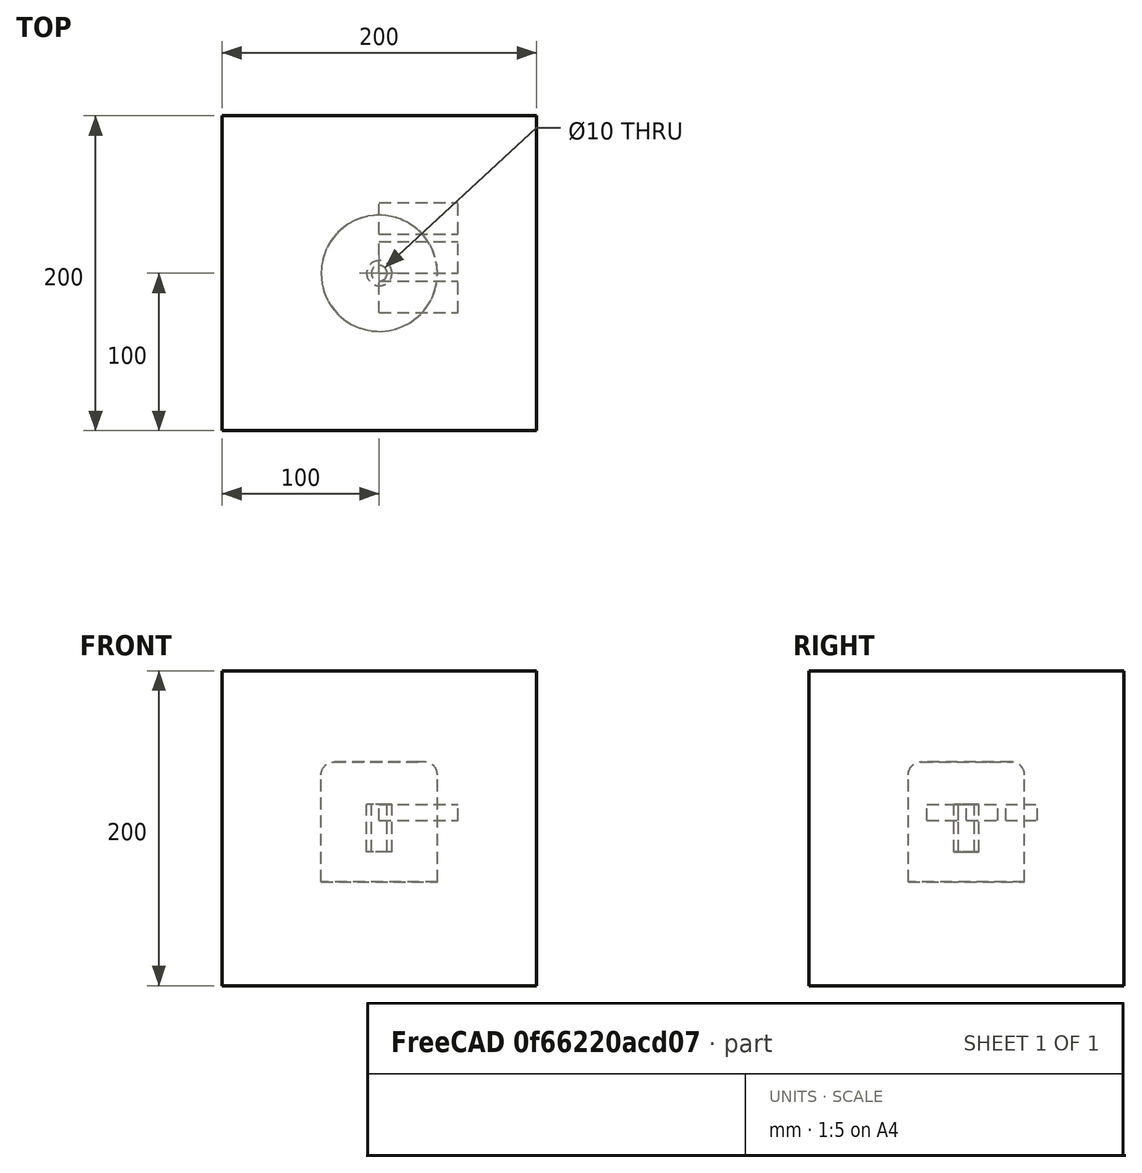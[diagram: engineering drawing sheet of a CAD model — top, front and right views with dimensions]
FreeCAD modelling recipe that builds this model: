
FCSTD DOCUMENT  (FreeCAD 1.0R39109 (Git))
Label: assemblyTest-A
License: All rights reserved
LicenseURL: http://en.wikipedia.org/wiki/All_rights_reserved
objects: App::DocumentObjectGroupPython×1254, Part::FeaturePython×5, App::Part×5, Part::Box×3, Part::Fuse×2
note: 10 computed .brp shape members not serialized (recipe doc carries the construction recipe); baked Part::Feature solids carry a one-line shape summary decoded from their .brp

FEATURE [App::DocumentObjectGroupPython] HALFPI  # scripted group (container) (typed FeaturePython)
  name = HALFPI
  value = pi/2.
FEATURE [App::DocumentObjectGroupPython] PI  # scripted group (container) (typed FeaturePython)
  name = PI
  value = 1.*pi
FEATURE [App::DocumentObjectGroupPython] TWOPI  # scripted group (container) (typed FeaturePython)
  name = TWOPI
  value = 2.*pi
FEATURE [App::DocumentObjectGroupPython] Variables  # scripted group (container) (typed FeaturePython)
FEATURE [App::DocumentObjectGroupPython] Quantities  # scripted group (container) (typed FeaturePython)
FEATURE [App::DocumentObjectGroupPython] Isotopes  # scripted group (container) (typed FeaturePython)
FEATURE [App::DocumentObjectGroupPython] Elements  # scripted group (container) (typed FeaturePython)
FEATURE [App::DocumentObjectGroupPython] G4Isotopes  # scripted group (container) (typed FeaturePython)
FEATURE [App::DocumentObjectGroupPython] H_element  # scripted group (container) (typed FeaturePython)
  Z = 1
  atom_value = 1.008
  formula = H
  name = H_element
FEATURE [App::DocumentObjectGroupPython] He_element  # scripted group (container) (typed FeaturePython)
  Z = 2
  atom_value = 4.0026
  formula = He
  name = He_element
FEATURE [App::DocumentObjectGroupPython] Li_element  # scripted group (container) (typed FeaturePython)
  Z = 3
  atom_value = 6.94
  formula = Li
  name = Li_element
FEATURE [App::DocumentObjectGroupPython] Be_element  # scripted group (container) (typed FeaturePython)
  Z = 4
  atom_value = 9.01218
  formula = Be
  name = Be_element
FEATURE [App::DocumentObjectGroupPython] B_element  # scripted group (container) (typed FeaturePython)
  Z = 5
  atom_value = 10.81
  formula = B
  name = B_element
FEATURE [App::DocumentObjectGroupPython] C_element  # scripted group (container) (typed FeaturePython)
  Z = 6
  atom_value = 12.011
  formula = C
  name = C_element
FEATURE [App::DocumentObjectGroupPython] N_element  # scripted group (container) (typed FeaturePython)
  Z = 7
  atom_value = 14.007
  formula = N
  name = N_element
FEATURE [App::DocumentObjectGroupPython] O_element  # scripted group (container) (typed FeaturePython)
  Z = 8
  atom_value = 15.999
  formula = O
  name = O_element
FEATURE [App::DocumentObjectGroupPython] F_element  # scripted group (container) (typed FeaturePython)
  Z = 9
  atom_value = 18.9984
  formula = F
  name = F_element
FEATURE [App::DocumentObjectGroupPython] Ne_element  # scripted group (container) (typed FeaturePython)
  Z = 10
  atom_value = 20.1797
  formula = Ne
  name = Ne_element
FEATURE [App::DocumentObjectGroupPython] Na_element  # scripted group (container) (typed FeaturePython)
  Z = 11
  atom_value = 22.9898
  formula = Na
  name = Na_element
FEATURE [App::DocumentObjectGroupPython] Mg_element  # scripted group (container) (typed FeaturePython)
  Z = 12
  atom_value = 24.305
  formula = Mg
  name = Mg_element
FEATURE [App::DocumentObjectGroupPython] Al_element  # scripted group (container) (typed FeaturePython)
  Z = 13
  atom_value = 26.9815
  formula = Al
  name = Al_element
FEATURE [App::DocumentObjectGroupPython] Si_element  # scripted group (container) (typed FeaturePython)
  Z = 14
  atom_value = 28.085
  formula = Si
  name = Si_element
FEATURE [App::DocumentObjectGroupPython] P_element  # scripted group (container) (typed FeaturePython)
  Z = 15
  atom_value = 30.9738
  formula = P
  name = P_element
FEATURE [App::DocumentObjectGroupPython] S_element  # scripted group (container) (typed FeaturePython)
  Z = 16
  atom_value = 32.06
  formula = S
  name = S_element
FEATURE [App::DocumentObjectGroupPython] Cl_element  # scripted group (container) (typed FeaturePython)
  Z = 17
  atom_value = 35.45
  formula = Cl
  name = Cl_element
FEATURE [App::DocumentObjectGroupPython] Ar_element  # scripted group (container) (typed FeaturePython)
  Z = 18
  atom_value = 39.95
  formula = Ar
  name = Ar_element
FEATURE [App::DocumentObjectGroupPython] K_element  # scripted group (container) (typed FeaturePython)
  Z = 19
  atom_value = 39.0983
  formula = K
  name = K_element
FEATURE [App::DocumentObjectGroupPython] Ca_element  # scripted group (container) (typed FeaturePython)
  Z = 20
  atom_value = 40.078
  formula = Ca
  name = Ca_element
FEATURE [App::DocumentObjectGroupPython] Sc_element  # scripted group (container) (typed FeaturePython)
  Z = 21
  atom_value = 44.9559
  formula = Sc
  name = Sc_element
FEATURE [App::DocumentObjectGroupPython] Ti_element  # scripted group (container) (typed FeaturePython)
  Z = 22
  atom_value = 47.867
  formula = Ti
  name = Ti_element
FEATURE [App::DocumentObjectGroupPython] V_element  # scripted group (container) (typed FeaturePython)
  Z = 23
  atom_value = 50.9415
  formula = V
  name = V_element
FEATURE [App::DocumentObjectGroupPython] Cr_element  # scripted group (container) (typed FeaturePython)
  Z = 24
  atom_value = 51.9961
  formula = Cr
  name = Cr_element
FEATURE [App::DocumentObjectGroupPython] Mn_element  # scripted group (container) (typed FeaturePython)
  Z = 25
  atom_value = 54.938
  formula = Mn
  name = Mn_element
FEATURE [App::DocumentObjectGroupPython] Fe_element  # scripted group (container) (typed FeaturePython)
  Z = 26
  atom_value = 55.845
  formula = Fe
  name = Fe_element
FEATURE [App::DocumentObjectGroupPython] Co_element  # scripted group (container) (typed FeaturePython)
  Z = 27
  atom_value = 58.9332
  formula = Co
  name = Co_element
FEATURE [App::DocumentObjectGroupPython] Ni_element  # scripted group (container) (typed FeaturePython)
  Z = 28
  atom_value = 58.6934
  formula = Ni
  name = Ni_element
FEATURE [App::DocumentObjectGroupPython] Cu_element  # scripted group (container) (typed FeaturePython)
  Z = 29
  atom_value = 63.546
  formula = Cu
  name = Cu_element
FEATURE [App::DocumentObjectGroupPython] Zn_element  # scripted group (container) (typed FeaturePython)
  Z = 30
  atom_value = 65.38
  formula = Zn
  name = Zn_element
FEATURE [App::DocumentObjectGroupPython] Ga_element  # scripted group (container) (typed FeaturePython)
  Z = 31
  atom_value = 69.723
  formula = Ga
  name = Ga_element
FEATURE [App::DocumentObjectGroupPython] Ge_element  # scripted group (container) (typed FeaturePython)
  Z = 32
  atom_value = 72.63
  formula = Ge
  name = Ge_element
FEATURE [App::DocumentObjectGroupPython] As_element  # scripted group (container) (typed FeaturePython)
  Z = 33
  atom_value = 74.9216
  formula = As
  name = As_element
FEATURE [App::DocumentObjectGroupPython] Se_element  # scripted group (container) (typed FeaturePython)
  Z = 34
  atom_value = 78.971
  formula = Se
  name = Se_element
FEATURE [App::DocumentObjectGroupPython] Br_element  # scripted group (container) (typed FeaturePython)
  Z = 35
  atom_value = 79.904
  formula = Br
  name = Br_element
FEATURE [App::DocumentObjectGroupPython] Kr_element  # scripted group (container) (typed FeaturePython)
  Z = 36
  atom_value = 83.798
  formula = Kr
  name = Kr_element
FEATURE [App::DocumentObjectGroupPython] Rb_element  # scripted group (container) (typed FeaturePython)
  Z = 37
  atom_value = 85.4678
  formula = Rb
  name = Rb_element
FEATURE [App::DocumentObjectGroupPython] Sr_element  # scripted group (container) (typed FeaturePython)
  Z = 38
  atom_value = 87.62
  formula = Sr
  name = Sr_element
FEATURE [App::DocumentObjectGroupPython] Y_element  # scripted group (container) (typed FeaturePython)
  Z = 39
  atom_value = 88.9058
  formula = Y
  name = Y_element
FEATURE [App::DocumentObjectGroupPython] Zr_element  # scripted group (container) (typed FeaturePython)
  Z = 40
  atom_value = 91.224
  formula = Zr
  name = Zr_element
FEATURE [App::DocumentObjectGroupPython] Nb_element  # scripted group (container) (typed FeaturePython)
  Z = 41
  atom_value = 92.9064
  formula = Nb
  name = Nb_element
FEATURE [App::DocumentObjectGroupPython] Mo_element  # scripted group (container) (typed FeaturePython)
  Z = 42
  atom_value = 95.95
  formula = Mo
  name = Mo_element
FEATURE [App::DocumentObjectGroupPython] Tc_element  # scripted group (container) (typed FeaturePython)
  Z = 43
  atom_value = 97
  formula = Tc
  name = Tc_element
FEATURE [App::DocumentObjectGroupPython] Ru_element  # scripted group (container) (typed FeaturePython)
  Z = 44
  atom_value = 101.07
  formula = Ru
  name = Ru_element
FEATURE [App::DocumentObjectGroupPython] Rh_element  # scripted group (container) (typed FeaturePython)
  Z = 45
  atom_value = 102.905
  formula = Rh
  name = Rh_element
FEATURE [App::DocumentObjectGroupPython] Pd_element  # scripted group (container) (typed FeaturePython)
  Z = 46
  atom_value = 106.42
  formula = Pd
  name = Pd_element
FEATURE [App::DocumentObjectGroupPython] Ag_element  # scripted group (container) (typed FeaturePython)
  Z = 47
  atom_value = 107.868
  formula = Ag
  name = Ag_element
FEATURE [App::DocumentObjectGroupPython] Cd_element  # scripted group (container) (typed FeaturePython)
  Z = 48
  atom_value = 112.414
  formula = Cd
  name = Cd_element
FEATURE [App::DocumentObjectGroupPython] In_element  # scripted group (container) (typed FeaturePython)
  Z = 49
  atom_value = 114.818
  formula = In
  name = In_element
FEATURE [App::DocumentObjectGroupPython] Sn_element  # scripted group (container) (typed FeaturePython)
  Z = 50
  atom_value = 118.71
  formula = Sn
  name = Sn_element
FEATURE [App::DocumentObjectGroupPython] Sb_element  # scripted group (container) (typed FeaturePython)
  Z = 51
  atom_value = 121.76
  formula = Sb
  name = Sb_element
FEATURE [App::DocumentObjectGroupPython] Te_element  # scripted group (container) (typed FeaturePython)
  Z = 52
  atom_value = 127.6
  formula = Te
  name = Te_element
FEATURE [App::DocumentObjectGroupPython] I_element  # scripted group (container) (typed FeaturePython)
  Z = 53
  atom_value = 126.904
  formula = I
  name = I_element
FEATURE [App::DocumentObjectGroupPython] Xe_element  # scripted group (container) (typed FeaturePython)
  Z = 54
  atom_value = 131.293
  formula = Xe
  name = Xe_element
FEATURE [App::DocumentObjectGroupPython] Cs_element  # scripted group (container) (typed FeaturePython)
  Z = 55
  atom_value = 132.905
  formula = Cs
  name = Cs_element
FEATURE [App::DocumentObjectGroupPython] Ba_element  # scripted group (container) (typed FeaturePython)
  Z = 56
  atom_value = 137.327
  formula = Ba
  name = Ba_element
FEATURE [App::DocumentObjectGroupPython] La_element  # scripted group (container) (typed FeaturePython)
  Z = 57
  atom_value = 138.905
  formula = La
  name = La_element
FEATURE [App::DocumentObjectGroupPython] Ce_element  # scripted group (container) (typed FeaturePython)
  Z = 58
  atom_value = 140.116
  formula = Ce
  name = Ce_element
FEATURE [App::DocumentObjectGroupPython] Pr_element  # scripted group (container) (typed FeaturePython)
  Z = 59
  atom_value = 140.908
  formula = Pr
  name = Pr_element
FEATURE [App::DocumentObjectGroupPython] Nd_element  # scripted group (container) (typed FeaturePython)
  Z = 60
  atom_value = 144.242
  formula = Nd
  name = Nd_element
FEATURE [App::DocumentObjectGroupPython] Pm_element  # scripted group (container) (typed FeaturePython)
  Z = 61
  atom_value = 145
  formula = Pm
  name = Pm_element
FEATURE [App::DocumentObjectGroupPython] Sm_element  # scripted group (container) (typed FeaturePython)
  Z = 62
  atom_value = 150.36
  formula = Sm
  name = Sm_element
FEATURE [App::DocumentObjectGroupPython] Eu_element  # scripted group (container) (typed FeaturePython)
  Z = 63
  atom_value = 151.964
  formula = Eu
  name = Eu_element
FEATURE [App::DocumentObjectGroupPython] Gd_element  # scripted group (container) (typed FeaturePython)
  Z = 64
  atom_value = 157.25
  formula = Gd
  name = Gd_element
FEATURE [App::DocumentObjectGroupPython] Tb_element  # scripted group (container) (typed FeaturePython)
  Z = 65
  atom_value = 158.925
  formula = Tb
  name = Tb_element
FEATURE [App::DocumentObjectGroupPython] Dy_element  # scripted group (container) (typed FeaturePython)
  Z = 66
  atom_value = 162.5
  formula = Dy
  name = Dy_element
FEATURE [App::DocumentObjectGroupPython] Ho_element  # scripted group (container) (typed FeaturePython)
  Z = 67
  atom_value = 164.93
  formula = Ho
  name = Ho_element
FEATURE [App::DocumentObjectGroupPython] Er_element  # scripted group (container) (typed FeaturePython)
  Z = 68
  atom_value = 167.259
  formula = Er
  name = Er_element
FEATURE [App::DocumentObjectGroupPython] Tm_element  # scripted group (container) (typed FeaturePython)
  Z = 69
  atom_value = 168.934
  formula = Tm
  name = Tm_element
FEATURE [App::DocumentObjectGroupPython] Yb_element  # scripted group (container) (typed FeaturePython)
  Z = 70
  atom_value = 173.045
  formula = Yb
  name = Yb_element
FEATURE [App::DocumentObjectGroupPython] Lu_element  # scripted group (container) (typed FeaturePython)
  Z = 71
  atom_value = 174.967
  formula = Lu
  name = Lu_element
FEATURE [App::DocumentObjectGroupPython] Hf_element  # scripted group (container) (typed FeaturePython)
  Z = 72
  atom_value = 178.49
  formula = Hf
  name = Hf_element
FEATURE [App::DocumentObjectGroupPython] Ta_element  # scripted group (container) (typed FeaturePython)
  Z = 73
  atom_value = 180.948
  formula = Ta
  name = Ta_element
FEATURE [App::DocumentObjectGroupPython] W_element  # scripted group (container) (typed FeaturePython)
  Z = 74
  atom_value = 183.84
  formula = W
  name = W_element
FEATURE [App::DocumentObjectGroupPython] Re_element  # scripted group (container) (typed FeaturePython)
  Z = 75
  atom_value = 186.207
  formula = Re
  name = Re_element
FEATURE [App::DocumentObjectGroupPython] Os_element  # scripted group (container) (typed FeaturePython)
  Z = 76
  atom_value = 190.23
  formula = Os
  name = Os_element
FEATURE [App::DocumentObjectGroupPython] Ir_element  # scripted group (container) (typed FeaturePython)
  Z = 77
  atom_value = 192.217
  formula = Ir
  name = Ir_element
FEATURE [App::DocumentObjectGroupPython] Pt_element  # scripted group (container) (typed FeaturePython)
  Z = 78
  atom_value = 195.084
  formula = Pt
  name = Pt_element
FEATURE [App::DocumentObjectGroupPython] Au_element  # scripted group (container) (typed FeaturePython)
  Z = 79
  atom_value = 196.967
  formula = Au
  name = Au_element
FEATURE [App::DocumentObjectGroupPython] Hg_element  # scripted group (container) (typed FeaturePython)
  Z = 80
  atom_value = 200.592
  formula = Hg
  name = Hg_element
FEATURE [App::DocumentObjectGroupPython] Tl_element  # scripted group (container) (typed FeaturePython)
  Z = 81
  atom_value = 204.38
  formula = Tl
  name = Tl_element
FEATURE [App::DocumentObjectGroupPython] Pb_element  # scripted group (container) (typed FeaturePython)
  Z = 82
  atom_value = 207.2
  formula = Pb
  name = Pb_element
FEATURE [App::DocumentObjectGroupPython] Bi_element  # scripted group (container) (typed FeaturePython)
  Z = 83
  atom_value = 208.98
  formula = Bi
  name = Bi_element
FEATURE [App::DocumentObjectGroupPython] Po_element  # scripted group (container) (typed FeaturePython)
  Z = 84
  atom_value = 209
  formula = Po
  name = Po_element
FEATURE [App::DocumentObjectGroupPython] At_element  # scripted group (container) (typed FeaturePython)
  Z = 85
  atom_value = 210
  formula = At
  name = At_element
FEATURE [App::DocumentObjectGroupPython] Rn_element  # scripted group (container) (typed FeaturePython)
  Z = 86
  atom_value = 222
  formula = Rn
  name = Rn_element
FEATURE [App::DocumentObjectGroupPython] Fr_element  # scripted group (container) (typed FeaturePython)
  Z = 87
  atom_value = 223
  formula = Fr
  name = Fr_element
FEATURE [App::DocumentObjectGroupPython] Ra_element  # scripted group (container) (typed FeaturePython)
  Z = 88
  atom_value = 226
  formula = Ra
  name = Ra_element
FEATURE [App::DocumentObjectGroupPython] Ac_element  # scripted group (container) (typed FeaturePython)
  Z = 89
  atom_value = 227
  formula = Ac
  name = Ac_element
FEATURE [App::DocumentObjectGroupPython] Th_element  # scripted group (container) (typed FeaturePython)
  Z = 90
  atom_value = 232.038
  formula = Th
  name = Th_element
FEATURE [App::DocumentObjectGroupPython] Pa_element  # scripted group (container) (typed FeaturePython)
  Z = 91
  atom_value = 231.036
  formula = Pa
  name = Pa_element
FEATURE [App::DocumentObjectGroupPython] U_element  # scripted group (container) (typed FeaturePython)
  Z = 92
  atom_value = 238.029
  formula = U
  name = U_element
FEATURE [App::DocumentObjectGroupPython] Np_element  # scripted group (container) (typed FeaturePython)
  Z = 93
  atom_value = 237
  formula = Np
  name = Np_element
FEATURE [App::DocumentObjectGroupPython] Pu_element  # scripted group (container) (typed FeaturePython)
  Z = 94
  atom_value = 244
  formula = Pu
  name = Pu_element
FEATURE [App::DocumentObjectGroupPython] Am_element  # scripted group (container) (typed FeaturePython)
  Z = 95
  atom_value = 243
  formula = Am
  name = Am_element
FEATURE [App::DocumentObjectGroupPython] Cm_element  # scripted group (container) (typed FeaturePython)
  Z = 96
  atom_value = 247
  formula = Cm
  name = Cm_element
FEATURE [App::DocumentObjectGroupPython] Bk_element  # scripted group (container) (typed FeaturePython)
  Z = 97
  atom_value = 247
  formula = Bk
  name = Bk_element
FEATURE [App::DocumentObjectGroupPython] Cf_element  # scripted group (container) (typed FeaturePython)
  Z = 98
  atom_value = 251
  formula = Cf
  name = Cf_element
FEATURE [App::DocumentObjectGroupPython] G4Elements  # scripted group (container) (typed FeaturePython)
  Group = -> [H_element,He_element,Li_element,Be_element,B_element,C_element,N_element,O_element,F_element,Ne_element,Na_element,Mg_element,Al_element,Si_element,P_element,S_element,Cl_element,Ar_element,K_element,Ca_element,Sc_element,Ti_element,V_element,Cr_element,Mn_element,Fe_element,Co_element,Ni_element,Cu_element,Zn_element,Ga_element,Ge_element,As_element,Se_element,Br_element,Kr_element,Rb_element,+61 more]
FEATURE [Part::FeaturePython] GDMLBox_WorldBox  # WARN: FeaturePython — macro-defined, semantics opaque (R4)
  lunit = 2
  material = 5
  x = 200
  y = 200
  z = 200
FEATURE [App::DocumentObjectGroupPython] HALFPI001  # scripted group (container) (typed FeaturePython)
  name = HALFPI
  value = pi/2.
FEATURE [App::DocumentObjectGroupPython] PI001  # scripted group (container) (typed FeaturePython)
  name = PI
  value = 1.*pi
FEATURE [App::DocumentObjectGroupPython] TWOPI001  # scripted group (container) (typed FeaturePython)
  name = TWOPI
  value = 2.*pi
FEATURE [App::DocumentObjectGroupPython] HALFPI001001  # scripted group (container) (typed FeaturePython)
  name = HALFPI001
  value = pi/2.
FEATURE [App::DocumentObjectGroupPython] PI001001  # scripted group (container) (typed FeaturePython)
  name = PI001
  value = 1.*pi
FEATURE [App::DocumentObjectGroupPython] TWOPI001001  # scripted group (container) (typed FeaturePython)
  name = TWOPI001
  value = 2.*pi
FEATURE [App::DocumentObjectGroupPython] Constants  # scripted group (container) (typed FeaturePython)
  Group = -> [HALFPI,PI,TWOPI,HALFPI001,PI001,TWOPI001,HALFPI001001,PI001001,TWOPI001001]
FEATURE [Part::FeaturePython] GDMLTorus_Torus  # WARN: FeaturePython — macro-defined, semantics opaque (R4)
  aunit = deg
  deltaphi = 360
  lunit = 2
  material = 0
  rmax = 8
  rmin = 0
  rtor = 28.9
  startphi = 0
FEATURE [Part::FeaturePython] GDMLTube_Tube  # WARN: FeaturePython — macro-defined, semantics opaque (R4)
  aunit = 1
  deltaphi = 360
  lunit = 2
  material = 0
  rmax = 28.9
  rmin = 0
  startphi = 0
  z = 16
FEATURE [Part::FeaturePython] GDMLTube_Tube001  label="GDMLTube_T_1"  # WARN: FeaturePython — macro-defined, semantics opaque (R4)
  Placement = pos=(0,0,-34) rot=(0,0,-1;0.349066rad)
  aunit = 1
  deltaphi = 360
  lunit = 2
  material = 0
  rmax = 36.9
  rmin = 0
  startphi = 0
  z = 68
FEATURE [Part::Fuse] Union
  Base = -> GDMLTorus_Torus
  Placement = pos=(0,0,0) rot=(0,0,1;0.523599rad)
  Tool = -> GDMLTube_Tube
FEATURE [Part::Fuse] Union001  label="U1"
  Base = -> Union
  Placement = pos=(0,0,34) rot=(0,0,1;0rad)
  Tool = -> GDMLTube_Tube001
  material = 211
FEATURE [App::Part] Bool_Union001  label="Detector"
  Group = -> [GDMLTorus_Torus,GDMLTube_Tube,Union,GDMLTube_Tube001,Union001]
  Origin = -> Origin005
FEATURE [Part::FeaturePython] GDMLTube_Tube002  # WARN: FeaturePython — macro-defined, semantics opaque (R4)
  aunit = 1
  deltaphi = 360
  lunit = 2
  material = 109
  rmax = 8
  rmin = 5
  startphi = 0
  z = 30
FEATURE [App::Part] LV_Tube  label="Tube"
  Group = -> [GDMLTube_Tube002]
  Origin = -> Origin006
  Placement = pos=(57,0,0) rot=(0,1,0;1.5708rad)
FEATURE [App::Part] Part  label="DetectorAssembly"
  Group = -> [Bool_Union001,LV_Tube]
  Origin = -> Origin007
FEATURE [Part::Box] Box  label="Cube"
  AttacherType = Attacher::AttachEngine3D
  Height = 10
  Length = 50
  Placement = pos=(0,0,5) rot=(0,0,1;0rad)
  Width = 20
  material = 441
FEATURE [Part::Box] Box001  label="Cube001"
  AttacherType = Attacher::AttachEngine3D
  Height = 10
  Length = 50
  Placement = pos=(0,25,5) rot=(0,0,1;0rad)
  Width = 20
  material = 441
FEATURE [Part::Box] Box002  label="Cube002"
  AttacherType = Attacher::AttachEngine3D
  Height = 10
  Length = 50
  Placement = pos=(0,-25,5) rot=(0,0,1;0rad)
  Width = 20
  material = 261
FEATURE [App::Part] Part001  label="shieldAssembly"
  Group = -> [Box,Box001,Box002]
  Origin = -> Origin008
  Placement = pos=(0,0,58) rot=(0,0,1;0rad)
FEATURE [App::Part] worldVOL
  Group = -> [GDMLBox_WorldBox,Part,Part001]
  Origin = -> Origin
FEATURE [App::DocumentObjectGroupPython] H_element553  label="H_element : 0.246"  # scripted group (container) (typed FeaturePython)
  n = 0.101327
FEATURE [App::DocumentObjectGroupPython] C_element593  label="C_element : 0.974"  # scripted group (container) (typed FeaturePython)
  n = 0.7755
FEATURE [App::DocumentObjectGroupPython] N_element273  label="N_element : 0.828"  # scripted group (container) (typed FeaturePython)
  n = 0.035057
FEATURE [App::DocumentObjectGroupPython] O_element521  label="O_element : 0.966"  # scripted group (container) (typed FeaturePython)
  n = 0.0523159
FEATURE [App::DocumentObjectGroupPython] F_element077  label="F_element : 0.727"  # scripted group (container) (typed FeaturePython)
  n = 0.017422
FEATURE [App::DocumentObjectGroupPython] Ca_element057  label="Ca_element : 0.240"  # scripted group (container) (typed FeaturePython)
  n = 0.018378
FEATURE [App::DocumentObjectGroupPython] G4_A_150_TISSUE  label="G4_A-150_TISSUE"  # scripted group (container) (typed FeaturePython)
  Dunit = g/cm3
  Dvalue = 1.127
  Group = -> [H_element553,C_element593,N_element273,O_element521,F_element077,Ca_element057]
  conduct = 2
  density = 1
  expand = 3
  formula = G4_A-150_TISSUE
  name = G4_A-150_TISSUE
  specific = 4
FEATURE [App::DocumentObjectGroupPython] C_element594  label="C_element : 390"  # scripted group (container) (typed FeaturePython)
  n = 3
  ref = C_element
FEATURE [App::DocumentObjectGroupPython] H_element554  label="H_element : 358"  # scripted group (container) (typed FeaturePython)
  n = 6
  ref = H_element
FEATURE [App::DocumentObjectGroupPython] O_element522  label="O_element : 335"  # scripted group (container) (typed FeaturePython)
  n = 1
  ref = O_element
FEATURE [App::DocumentObjectGroupPython] G4_ACETONE  # scripted group (container) (typed FeaturePython)
  Dunit = g/cm3
  Dvalue = 0.7899
  Group = -> [C_element594,H_element554,O_element522]
  conduct = 2
  density = 1
  expand = 3
  formula = G4_ACETONE
  name = G4_ACETONE
  specific = 4
FEATURE [App::DocumentObjectGroupPython] C_element595  label="C_element : 391"  # scripted group (container) (typed FeaturePython)
  n = 2
  ref = C_element
FEATURE [App::DocumentObjectGroupPython] H_element555  label="H_element : 359"  # scripted group (container) (typed FeaturePython)
  n = 2
  ref = H_element
FEATURE [App::DocumentObjectGroupPython] G4_ACETYLENE  # scripted group (container) (typed FeaturePython)
  Dunit = g/cm3
  Dvalue = 0.0010967
  Group = -> [C_element595,H_element555]
  conduct = 2
  density = 1
  expand = 3
  formula = G4_ACETYLENE
  name = G4_ACETYLENE
  specific = 4
FEATURE [App::DocumentObjectGroupPython] C_element596  label="C_element : 392"  # scripted group (container) (typed FeaturePython)
  n = 5
  ref = C_element
FEATURE [App::DocumentObjectGroupPython] H_element556  label="H_element : 360"  # scripted group (container) (typed FeaturePython)
  n = 5
  ref = H_element
FEATURE [App::DocumentObjectGroupPython] N_element274  label="N_element : 154"  # scripted group (container) (typed FeaturePython)
  n = 5
  ref = N_element
FEATURE [App::DocumentObjectGroupPython] G4_ADENINE  # scripted group (container) (typed FeaturePython)
  Dunit = g/cm3
  Dvalue = 1.6
  Group = -> [C_element596,H_element556,N_element274]
  conduct = 2
  density = 1
  expand = 3
  formula = G4_ADENINE
  name = G4_ADENINE
  specific = 4
FEATURE [App::DocumentObjectGroupPython] H_element557  label="H_element : 0.247"  # scripted group (container) (typed FeaturePython)
  n = 0.114
FEATURE [App::DocumentObjectGroupPython] C_element597  label="C_element : 0.975"  # scripted group (container) (typed FeaturePython)
  n = 0.598
FEATURE [App::DocumentObjectGroupPython] N_element275  label="N_element : 0.829"  # scripted group (container) (typed FeaturePython)
  n = 0.007
FEATURE [App::DocumentObjectGroupPython] O_element523  label="O_element : 0.967"  # scripted group (container) (typed FeaturePython)
  n = 0.278
FEATURE [App::DocumentObjectGroupPython] Na_element081  label="Na_element : 0.142"  # scripted group (container) (typed FeaturePython)
  n = 0.001
FEATURE [App::DocumentObjectGroupPython] S_element093  label="S_element : 0.065"  # scripted group (container) (typed FeaturePython)
  n = 0.001
FEATURE [App::DocumentObjectGroupPython] Cl_element121  label="Cl_element : 0.627"  # scripted group (container) (typed FeaturePython)
  n = 0.001
FEATURE [App::DocumentObjectGroupPython] G4_ADIPOSE_TISSUE_ICRP  # scripted group (container) (typed FeaturePython)
  Dunit = g/cm3
  Dvalue = 0.95
  Group = -> [H_element557,C_element597,N_element275,O_element523,Na_element081,S_element093,Cl_element121]
  conduct = 2
  density = 1
  expand = 3
  formula = G4_ADIPOSE_TISSUE_ICRP
  name = G4_ADIPOSE_TISSUE_ICRP
  specific = 4
FEATURE [App::DocumentObjectGroupPython] C_element598  label="C_element : 0.976"  # scripted group (container) (typed FeaturePython)
  n = 0.000124
FEATURE [App::DocumentObjectGroupPython] N_element276  label="N_element : 0.830"  # scripted group (container) (typed FeaturePython)
  n = 0.755268
FEATURE [App::DocumentObjectGroupPython] O_element524  label="O_element : 0.968"  # scripted group (container) (typed FeaturePython)
  n = 0.231781
FEATURE [App::DocumentObjectGroupPython] Ar_element009  label="Ar_element : 0.016"  # scripted group (container) (typed FeaturePython)
  n = 0.012827
FEATURE [App::DocumentObjectGroupPython] G4_AIR  # scripted group (container) (typed FeaturePython)
  Dunit = g/cm3
  Dvalue = 0.00120479
  Group = -> [C_element598,N_element276,O_element524,Ar_element009]
  conduct = 2
  density = 1
  expand = 3
  formula = G4_AIR
  name = G4_AIR
  specific = 4
FEATURE [App::DocumentObjectGroupPython] C_element599  label="C_element : 393"  # scripted group (container) (typed FeaturePython)
  n = 3
  ref = C_element
FEATURE [App::DocumentObjectGroupPython] H_element558  label="H_element : 361"  # scripted group (container) (typed FeaturePython)
  n = 7
  ref = H_element
FEATURE [App::DocumentObjectGroupPython] N_element277  label="N_element : 155"  # scripted group (container) (typed FeaturePython)
  n = 1
  ref = N_element
FEATURE [App::DocumentObjectGroupPython] O_element525  label="O_element : 336"  # scripted group (container) (typed FeaturePython)
  n = 2
  ref = O_element
FEATURE [App::DocumentObjectGroupPython] G4_ALANINE  # scripted group (container) (typed FeaturePython)
  Dunit = g/cm3
  Dvalue = 1.42
  Group = -> [C_element599,H_element558,N_element277,O_element525]
  conduct = 2
  density = 1
  expand = 3
  formula = G4_ALANINE
  name = G4_ALANINE
  specific = 4
FEATURE [App::DocumentObjectGroupPython] Al_element017  label="Al_element : 007"  # scripted group (container) (typed FeaturePython)
  n = 2
  ref = Al_element
FEATURE [App::DocumentObjectGroupPython] O_element526  label="O_element : 337"  # scripted group (container) (typed FeaturePython)
  n = 3
  ref = O_element
FEATURE [App::DocumentObjectGroupPython] G4_ALUMINUM_OXIDE  # scripted group (container) (typed FeaturePython)
  Dunit = g/cm3
  Dvalue = 3.97
  Group = -> [Al_element017,O_element526]
  conduct = 2
  density = 1
  expand = 3
  formula = G4_ALUMINUM_OXIDE
  name = G4_ALUMINUM_OXIDE
  specific = 4
FEATURE [App::DocumentObjectGroupPython] H_element559  label="H_element : 0.248"  # scripted group (container) (typed FeaturePython)
  n = 0.10593
FEATURE [App::DocumentObjectGroupPython] C_element600  label="C_element : 0.977"  # scripted group (container) (typed FeaturePython)
  n = 0.788974
FEATURE [App::DocumentObjectGroupPython] O_element527  label="O_element : 0.969"  # scripted group (container) (typed FeaturePython)
  n = 0.105096
FEATURE [App::DocumentObjectGroupPython] G4_AMBER  # scripted group (container) (typed FeaturePython)
  Dunit = g/cm3
  Dvalue = 1.1
  Group = -> [H_element559,C_element600,O_element527]
  conduct = 2
  density = 1
  expand = 3
  formula = G4_AMBER
  name = G4_AMBER
  specific = 4
FEATURE [App::DocumentObjectGroupPython] N_element278  label="N_element : 156"  # scripted group (container) (typed FeaturePython)
  n = 1
  ref = N_element
FEATURE [App::DocumentObjectGroupPython] H_element560  label="H_element : 362"  # scripted group (container) (typed FeaturePython)
  n = 3
  ref = H_element
FEATURE [App::DocumentObjectGroupPython] G4_AMMONIA  # scripted group (container) (typed FeaturePython)
  Dunit = g/cm3
  Dvalue = 0.000826019
  Group = -> [N_element278,H_element560]
  conduct = 2
  density = 1
  expand = 3
  formula = G4_AMMONIA
  name = G4_AMMONIA
  specific = 4
FEATURE [App::DocumentObjectGroupPython] C_element601  label="C_element : 394"  # scripted group (container) (typed FeaturePython)
  n = 6
  ref = C_element
FEATURE [App::DocumentObjectGroupPython] H_element561  label="H_element : 363"  # scripted group (container) (typed FeaturePython)
  n = 7
  ref = H_element
FEATURE [App::DocumentObjectGroupPython] N_element279  label="N_element : 157"  # scripted group (container) (typed FeaturePython)
  n = 1
  ref = N_element
FEATURE [App::DocumentObjectGroupPython] G4_ANILINE  # scripted group (container) (typed FeaturePython)
  Dunit = g/cm3
  Dvalue = 1.0235
  Group = -> [C_element601,H_element561,N_element279]
  conduct = 2
  density = 1
  expand = 3
  formula = G4_ANILINE
  name = G4_ANILINE
  specific = 4
FEATURE [App::DocumentObjectGroupPython] C_element602  label="C_element : 395"  # scripted group (container) (typed FeaturePython)
  n = 14
  ref = C_element
FEATURE [App::DocumentObjectGroupPython] H_element562  label="H_element : 364"  # scripted group (container) (typed FeaturePython)
  n = 10
  ref = H_element
FEATURE [App::DocumentObjectGroupPython] G4_ANTHRACENE  # scripted group (container) (typed FeaturePython)
  Dunit = g/cm3
  Dvalue = 1.283
  Group = -> [C_element602,H_element562]
  conduct = 2
  density = 1
  expand = 3
  formula = G4_ANTHRACENE
  name = G4_ANTHRACENE
  specific = 4
FEATURE [App::DocumentObjectGroupPython] H_element563  label="H_element : 0.249"  # scripted group (container) (typed FeaturePython)
  n = 0.0654709
FEATURE [App::DocumentObjectGroupPython] C_element603  label="C_element : 0.978"  # scripted group (container) (typed FeaturePython)
  n = 0.536944
FEATURE [App::DocumentObjectGroupPython] N_element280  label="N_element : 0.831"  # scripted group (container) (typed FeaturePython)
  n = 0.0215
FEATURE [App::DocumentObjectGroupPython] O_element528  label="O_element : 0.970"  # scripted group (container) (typed FeaturePython)
  n = 0.032085
FEATURE [App::DocumentObjectGroupPython] F_element078  label="F_element : 0.728"  # scripted group (container) (typed FeaturePython)
  n = 0.167411
FEATURE [App::DocumentObjectGroupPython] Ca_element058  label="Ca_element : 0.241"  # scripted group (container) (typed FeaturePython)
  n = 0.176589
FEATURE [App::DocumentObjectGroupPython] G4_B_100_BONE  label="G4_B-100_BONE"  # scripted group (container) (typed FeaturePython)
  Dunit = g/cm3
  Dvalue = 1.45
  Group = -> [H_element563,C_element603,N_element280,O_element528,F_element078,Ca_element058]
  conduct = 2
  density = 1
  expand = 3
  formula = G4_B-100_BONE
  name = G4_B-100_BONE
  specific = 4
FEATURE [App::DocumentObjectGroupPython] H_element564  label="H_element : 0.250"  # scripted group (container) (typed FeaturePython)
  n = 0.057441
FEATURE [App::DocumentObjectGroupPython] C_element604  label="C_element : 0.979"  # scripted group (container) (typed FeaturePython)
  n = 0.774591
FEATURE [App::DocumentObjectGroupPython] O_element529  label="O_element : 0.971"  # scripted group (container) (typed FeaturePython)
  n = 0.167968
FEATURE [App::DocumentObjectGroupPython] G4_BAKELITE  # scripted group (container) (typed FeaturePython)
  Dunit = g/cm3
  Dvalue = 1.25
  Group = -> [H_element564,C_element604,O_element529]
  conduct = 2
  density = 1
  expand = 3
  formula = G4_BAKELITE
  name = G4_BAKELITE
  specific = 4
FEATURE [App::DocumentObjectGroupPython] Ba_element013  label="Ba_element : 012"  # scripted group (container) (typed FeaturePython)
  n = 1
  ref = Ba_element
FEATURE [App::DocumentObjectGroupPython] F_element079  label="F_element : 037"  # scripted group (container) (typed FeaturePython)
  n = 2
  ref = F_element
FEATURE [App::DocumentObjectGroupPython] G4_BARIUM_FLUORIDE  # scripted group (container) (typed FeaturePython)
  Dunit = g/cm3
  Dvalue = 4.89
  Group = -> [Ba_element013,F_element079]
  conduct = 2
  density = 1
  expand = 3
  formula = G4_BARIUM_FLUORIDE
  name = G4_BARIUM_FLUORIDE
  specific = 4
FEATURE [App::DocumentObjectGroupPython] Ba_element014  label="Ba_element : 013"  # scripted group (container) (typed FeaturePython)
  n = 1
  ref = Ba_element
FEATURE [App::DocumentObjectGroupPython] S_element094  label="S_element : 028"  # scripted group (container) (typed FeaturePython)
  n = 1
  ref = S_element
FEATURE [App::DocumentObjectGroupPython] O_element530  label="O_element : 338"  # scripted group (container) (typed FeaturePython)
  n = 4
  ref = O_element
FEATURE [App::DocumentObjectGroupPython] G4_BARIUM_SULFATE  # scripted group (container) (typed FeaturePython)
  Dunit = g/cm3
  Dvalue = 4.5
  Group = -> [Ba_element014,S_element094,O_element530]
  conduct = 2
  density = 1
  expand = 3
  formula = G4_BARIUM_SULFATE
  name = G4_BARIUM_SULFATE
  specific = 4
FEATURE [App::DocumentObjectGroupPython] C_element605  label="C_element : 396"  # scripted group (container) (typed FeaturePython)
  n = 6
  ref = C_element
FEATURE [App::DocumentObjectGroupPython] H_element565  label="H_element : 365"  # scripted group (container) (typed FeaturePython)
  n = 6
  ref = H_element
FEATURE [App::DocumentObjectGroupPython] G4_BENZENE  # scripted group (container) (typed FeaturePython)
  Dunit = g/cm3
  Dvalue = 0.87865
  Group = -> [C_element605,H_element565]
  conduct = 2
  density = 1
  expand = 3
  formula = G4_BENZENE
  name = G4_BENZENE
  specific = 4
FEATURE [App::DocumentObjectGroupPython] Be_element009  label="Be_element : 008"  # scripted group (container) (typed FeaturePython)
  n = 1
  ref = Be_element
FEATURE [App::DocumentObjectGroupPython] O_element531  label="O_element : 339"  # scripted group (container) (typed FeaturePython)
  n = 1
  ref = O_element
FEATURE [App::DocumentObjectGroupPython] G4_BERYLLIUM_OXIDE  # scripted group (container) (typed FeaturePython)
  Dunit = g/cm3
  Dvalue = 3.01
  Group = -> [Be_element009,O_element531]
  conduct = 2
  density = 1
  expand = 3
  formula = G4_BERYLLIUM_OXIDE
  name = G4_BERYLLIUM_OXIDE
  specific = 4
FEATURE [App::DocumentObjectGroupPython] Bi_element009  label="Bi_element : 009"  # scripted group (container) (typed FeaturePython)
  n = 4
  ref = Bi_element
FEATURE [App::DocumentObjectGroupPython] Ge_element009  label="Ge_element : 008"  # scripted group (container) (typed FeaturePython)
  n = 3
  ref = Ge_element
FEATURE [App::DocumentObjectGroupPython] O_element532  label="O_element : 340"  # scripted group (container) (typed FeaturePython)
  n = 12
  ref = O_element
FEATURE [App::DocumentObjectGroupPython] G4_BGO  # scripted group (container) (typed FeaturePython)
  Dunit = g/cm3
  Dvalue = 7.13
  Group = -> [Bi_element009,Ge_element009,O_element532]
  conduct = 2
  density = 1
  expand = 3
  formula = G4_BGO
  name = G4_BGO
  specific = 4
FEATURE [App::DocumentObjectGroupPython] H_element566  label="H_element : 0.251"  # scripted group (container) (typed FeaturePython)
  n = 0.102
FEATURE [App::DocumentObjectGroupPython] C_element606  label="C_element : 0.980"  # scripted group (container) (typed FeaturePython)
  n = 0.11
FEATURE [App::DocumentObjectGroupPython] N_element281  label="N_element : 0.832"  # scripted group (container) (typed FeaturePython)
  n = 0.033
FEATURE [App::DocumentObjectGroupPython] O_element533  label="O_element : 0.972"  # scripted group (container) (typed FeaturePython)
  n = 0.745
FEATURE [App::DocumentObjectGroupPython] Na_element082  label="Na_element : 0.143"  # scripted group (container) (typed FeaturePython)
  n = 0.001
FEATURE [App::DocumentObjectGroupPython] P_element077  label="P_element : 0.138"  # scripted group (container) (typed FeaturePython)
  n = 0.001
FEATURE [App::DocumentObjectGroupPython] S_element095  label="S_element : 0.066"  # scripted group (container) (typed FeaturePython)
  n = 0.002
FEATURE [App::DocumentObjectGroupPython] Cl_element122  label="Cl_element : 0.628"  # scripted group (container) (typed FeaturePython)
  n = 0.003
FEATURE [App::DocumentObjectGroupPython] K_element053  label="K_element : 0.044"  # scripted group (container) (typed FeaturePython)
  n = 0.002
FEATURE [App::DocumentObjectGroupPython] Fe_element033  label="Fe_element : 0.021"  # scripted group (container) (typed FeaturePython)
  n = 0.001
FEATURE [App::DocumentObjectGroupPython] G4_BLOOD_ICRP  # scripted group (container) (typed FeaturePython)
  Dunit = g/cm3
  Dvalue = 1.06
  Group = -> [H_element566,C_element606,N_element281,O_element533,Na_element082,P_element077,S_element095,Cl_element122,K_element053,Fe_element033]
  conduct = 2
  density = 1
  expand = 3
  formula = G4_BLOOD_ICRP
  name = G4_BLOOD_ICRP
  specific = 4
FEATURE [App::DocumentObjectGroupPython] H_element567  label="H_element : 0.252"  # scripted group (container) (typed FeaturePython)
  n = 0.064
FEATURE [App::DocumentObjectGroupPython] C_element607  label="C_element : 0.981"  # scripted group (container) (typed FeaturePython)
  n = 0.278
FEATURE [App::DocumentObjectGroupPython] N_element282  label="N_element : 0.833"  # scripted group (container) (typed FeaturePython)
  n = 0.027
FEATURE [App::DocumentObjectGroupPython] O_element534  label="O_element : 0.973"  # scripted group (container) (typed FeaturePython)
  n = 0.41
FEATURE [App::DocumentObjectGroupPython] Mg_element045  label="Mg_element : 0.150"  # scripted group (container) (typed FeaturePython)
  n = 0.002
FEATURE [App::DocumentObjectGroupPython] P_element078  label="P_element : 0.139"  # scripted group (container) (typed FeaturePython)
  n = 0.07
FEATURE [App::DocumentObjectGroupPython] S_element096  label="S_element : 0.067"  # scripted group (container) (typed FeaturePython)
  n = 0.002
FEATURE [App::DocumentObjectGroupPython] Ca_element059  label="Ca_element : 0.242"  # scripted group (container) (typed FeaturePython)
  n = 0.147
FEATURE [App::DocumentObjectGroupPython] G4_BONE_COMPACT_ICRU  # scripted group (container) (typed FeaturePython)
  Dunit = g/cm3
  Dvalue = 1.85
  Group = -> [H_element567,C_element607,N_element282,O_element534,Mg_element045,P_element078,S_element096,Ca_element059]
  conduct = 2
  density = 1
  expand = 3
  formula = G4_BONE_COMPACT_ICRU
  name = G4_BONE_COMPACT_ICRU
  specific = 4
FEATURE [App::DocumentObjectGroupPython] H_element568  label="H_element : 0.253"  # scripted group (container) (typed FeaturePython)
  n = 0.034
FEATURE [App::DocumentObjectGroupPython] C_element608  label="C_element : 0.982"  # scripted group (container) (typed FeaturePython)
  n = 0.155
FEATURE [App::DocumentObjectGroupPython] N_element283  label="N_element : 0.834"  # scripted group (container) (typed FeaturePython)
  n = 0.042
FEATURE [App::DocumentObjectGroupPython] O_element535  label="O_element : 0.974"  # scripted group (container) (typed FeaturePython)
  n = 0.435
FEATURE [App::DocumentObjectGroupPython] Na_element083  label="Na_element : 0.144"  # scripted group (container) (typed FeaturePython)
  n = 0.001
FEATURE [App::DocumentObjectGroupPython] Mg_element046  label="Mg_element : 0.151"  # scripted group (container) (typed FeaturePython)
  n = 0.002
FEATURE [App::DocumentObjectGroupPython] P_element079  label="P_element : 0.140"  # scripted group (container) (typed FeaturePython)
  n = 0.103
FEATURE [App::DocumentObjectGroupPython] S_element097  label="S_element : 0.068"  # scripted group (container) (typed FeaturePython)
  n = 0.003
FEATURE [App::DocumentObjectGroupPython] Ca_element060  label="Ca_element : 0.243"  # scripted group (container) (typed FeaturePython)
  n = 0.225
FEATURE [App::DocumentObjectGroupPython] G4_BONE_CORTICAL_ICRP  # scripted group (container) (typed FeaturePython)
  Dunit = g/cm3
  Dvalue = 1.92
  Group = -> [H_element568,C_element608,N_element283,O_element535,Na_element083,Mg_element046,P_element079,S_element097,Ca_element060]
  conduct = 2
  density = 1
  expand = 3
  formula = G4_BONE_CORTICAL_ICRP
  name = G4_BONE_CORTICAL_ICRP
  specific = 4
FEATURE [App::DocumentObjectGroupPython] B_element029  label="B_element : 023"  # scripted group (container) (typed FeaturePython)
  n = 4
  ref = B_element
FEATURE [App::DocumentObjectGroupPython] C_element609  label="C_element : 397"  # scripted group (container) (typed FeaturePython)
  n = 1
  ref = C_element
FEATURE [App::DocumentObjectGroupPython] G4_BORON_CARBIDE  # scripted group (container) (typed FeaturePython)
  Dunit = g/cm3
  Dvalue = 2.52
  Group = -> [B_element029,C_element609]
  conduct = 2
  density = 1
  expand = 3
  formula = G4_BORON_CARBIDE
  name = G4_BORON_CARBIDE
  specific = 4
FEATURE [App::DocumentObjectGroupPython] B_element030  label="B_element : 024"  # scripted group (container) (typed FeaturePython)
  n = 2
  ref = B_element
FEATURE [App::DocumentObjectGroupPython] O_element536  label="O_element : 341"  # scripted group (container) (typed FeaturePython)
  n = 3
  ref = O_element
FEATURE [App::DocumentObjectGroupPython] G4_BORON_OXIDE  # scripted group (container) (typed FeaturePython)
  Dunit = g/cm3
  Dvalue = 1.812
  Group = -> [B_element030,O_element536]
  conduct = 2
  density = 1
  expand = 3
  formula = G4_BORON_OXIDE
  name = G4_BORON_OXIDE
  specific = 4
FEATURE [App::DocumentObjectGroupPython] H_element569  label="H_element : 0.254"  # scripted group (container) (typed FeaturePython)
  n = 0.107
FEATURE [App::DocumentObjectGroupPython] C_element610  label="C_element : 0.983"  # scripted group (container) (typed FeaturePython)
  n = 0.145
FEATURE [App::DocumentObjectGroupPython] N_element284  label="N_element : 0.835"  # scripted group (container) (typed FeaturePython)
  n = 0.022
FEATURE [App::DocumentObjectGroupPython] O_element537  label="O_element : 0.975"  # scripted group (container) (typed FeaturePython)
  n = 0.712
FEATURE [App::DocumentObjectGroupPython] Na_element084  label="Na_element : 0.145"  # scripted group (container) (typed FeaturePython)
  n = 0.002
FEATURE [App::DocumentObjectGroupPython] P_element080  label="P_element : 0.141"  # scripted group (container) (typed FeaturePython)
  n = 0.004
FEATURE [App::DocumentObjectGroupPython] S_element098  label="S_element : 0.069"  # scripted group (container) (typed FeaturePython)
  n = 0.002
FEATURE [App::DocumentObjectGroupPython] Cl_element123  label="Cl_element : 0.629"  # scripted group (container) (typed FeaturePython)
  n = 0.003
FEATURE [App::DocumentObjectGroupPython] K_element054  label="K_element : 0.045"  # scripted group (container) (typed FeaturePython)
  n = 0.003
FEATURE [App::DocumentObjectGroupPython] G4_BRAIN_ICRP  # scripted group (container) (typed FeaturePython)
  Dunit = g/cm3
  Dvalue = 1.04
  Group = -> [H_element569,C_element610,N_element284,O_element537,Na_element084,P_element080,S_element098,Cl_element123,K_element054]
  conduct = 2
  density = 1
  expand = 3
  formula = G4_BRAIN_ICRP
  name = G4_BRAIN_ICRP
  specific = 4
FEATURE [App::DocumentObjectGroupPython] C_element611  label="C_element : 398"  # scripted group (container) (typed FeaturePython)
  n = 4
  ref = C_element
FEATURE [App::DocumentObjectGroupPython] H_element570  label="H_element : 366"  # scripted group (container) (typed FeaturePython)
  n = 10
  ref = H_element
FEATURE [App::DocumentObjectGroupPython] G4_BUTANE  # scripted group (container) (typed FeaturePython)
  Dunit = g/cm3
  Dvalue = 0.00249343
  Group = -> [C_element611,H_element570]
  conduct = 2
  density = 1
  expand = 3
  formula = G4_BUTANE
  name = G4_BUTANE
  specific = 4
FEATURE [App::DocumentObjectGroupPython] C_element612  label="C_element : 399"  # scripted group (container) (typed FeaturePython)
  n = 4
  ref = C_element
FEATURE [App::DocumentObjectGroupPython] H_element571  label="H_element : 367"  # scripted group (container) (typed FeaturePython)
  n = 10
  ref = H_element
FEATURE [App::DocumentObjectGroupPython] O_element538  label="O_element : 342"  # scripted group (container) (typed FeaturePython)
  n = 1
  ref = O_element
FEATURE [App::DocumentObjectGroupPython] G4_N_BUTYL_ALCOHOL  label="G4_N-BUTYL_ALCOHOL"  # scripted group (container) (typed FeaturePython)
  Dunit = g/cm3
  Dvalue = 0.8098
  Group = -> [C_element612,H_element571,O_element538]
  conduct = 2
  density = 1
  expand = 3
  formula = G4_N-BUTYL_ALCOHOL
  name = G4_N-BUTYL_ALCOHOL
  specific = 4
FEATURE [App::DocumentObjectGroupPython] H_element572  label="H_element : 0.255"  # scripted group (container) (typed FeaturePython)
  n = 0.02468
FEATURE [App::DocumentObjectGroupPython] C_element613  label="C_element : 0.984"  # scripted group (container) (typed FeaturePython)
  n = 0.501611
FEATURE [App::DocumentObjectGroupPython] O_element539  label="O_element : 0.976"  # scripted group (container) (typed FeaturePython)
  n = 0.004527
FEATURE [App::DocumentObjectGroupPython] F_element080  label="F_element : 0.729"  # scripted group (container) (typed FeaturePython)
  n = 0.465209
FEATURE [App::DocumentObjectGroupPython] Si_element029  label="Si_element : 0.390"  # scripted group (container) (typed FeaturePython)
  n = 0.003973
FEATURE [App::DocumentObjectGroupPython] G4_C_552  label="G4_C-552"  # scripted group (container) (typed FeaturePython)
  Dunit = g/cm3
  Dvalue = 1.76
  Group = -> [H_element572,C_element613,O_element539,F_element080,Si_element029]
  conduct = 2
  density = 1
  expand = 3
  formula = G4_C-552
  name = G4_C-552
  specific = 4
FEATURE [App::DocumentObjectGroupPython] Cd_element013  label="Cd_element : 012"  # scripted group (container) (typed FeaturePython)
  n = 1
  ref = Cd_element
FEATURE [App::DocumentObjectGroupPython] Te_element009  label="Te_element : 008"  # scripted group (container) (typed FeaturePython)
  n = 1
  ref = Te_element
FEATURE [App::DocumentObjectGroupPython] G4_CADMIUM_TELLURIDE  # scripted group (container) (typed FeaturePython)
  Dunit = g/cm3
  Dvalue = 6.2
  Group = -> [Cd_element013,Te_element009]
  conduct = 2
  density = 1
  expand = 3
  formula = G4_CADMIUM_TELLURIDE
  name = G4_CADMIUM_TELLURIDE
  specific = 4
FEATURE [App::DocumentObjectGroupPython] Cd_element014  label="Cd_element : 013"  # scripted group (container) (typed FeaturePython)
  n = 1
  ref = Cd_element
FEATURE [App::DocumentObjectGroupPython] W_element021  label="W_element : 020"  # scripted group (container) (typed FeaturePython)
  n = 1
  ref = W_element
FEATURE [App::DocumentObjectGroupPython] O_element540  label="O_element : 343"  # scripted group (container) (typed FeaturePython)
  n = 4
  ref = O_element
FEATURE [App::DocumentObjectGroupPython] G4_CADMIUM_TUNGSTATE  # scripted group (container) (typed FeaturePython)
  Dunit = g/cm3
  Dvalue = 7.9
  Group = -> [Cd_element014,W_element021,O_element540]
  conduct = 2
  density = 1
  expand = 3
  formula = G4_CADMIUM_TUNGSTATE
  name = G4_CADMIUM_TUNGSTATE
  specific = 4
FEATURE [App::DocumentObjectGroupPython] Ca_element061  label="Ca_element : 028"  # scripted group (container) (typed FeaturePython)
  n = 1
  ref = Ca_element
FEATURE [App::DocumentObjectGroupPython] C_element614  label="C_element : 400"  # scripted group (container) (typed FeaturePython)
  n = 1
  ref = C_element
FEATURE [App::DocumentObjectGroupPython] O_element541  label="O_element : 344"  # scripted group (container) (typed FeaturePython)
  n = 3
  ref = O_element
FEATURE [App::DocumentObjectGroupPython] G4_CALCIUM_CARBONATE  # scripted group (container) (typed FeaturePython)
  Dunit = g/cm3
  Dvalue = 2.8
  Group = -> [Ca_element061,C_element614,O_element541]
  conduct = 2
  density = 1
  expand = 3
  formula = G4_CALCIUM_CARBONATE
  name = G4_CALCIUM_CARBONATE
  specific = 4
FEATURE [App::DocumentObjectGroupPython] Ca_element062  label="Ca_element : 029"  # scripted group (container) (typed FeaturePython)
  n = 1
  ref = Ca_element
FEATURE [App::DocumentObjectGroupPython] F_element081  label="F_element : 038"  # scripted group (container) (typed FeaturePython)
  n = 2
  ref = F_element
FEATURE [App::DocumentObjectGroupPython] G4_CALCIUM_FLUORIDE  # scripted group (container) (typed FeaturePython)
  Dunit = g/cm3
  Dvalue = 3.18
  Group = -> [Ca_element062,F_element081]
  conduct = 2
  density = 1
  expand = 3
  formula = G4_CALCIUM_FLUORIDE
  name = G4_CALCIUM_FLUORIDE
  specific = 4
FEATURE [App::DocumentObjectGroupPython] Ca_element063  label="Ca_element : 030"  # scripted group (container) (typed FeaturePython)
  n = 1
  ref = Ca_element
FEATURE [App::DocumentObjectGroupPython] O_element542  label="O_element : 345"  # scripted group (container) (typed FeaturePython)
  n = 1
  ref = O_element
FEATURE [App::DocumentObjectGroupPython] G4_CALCIUM_OXIDE  # scripted group (container) (typed FeaturePython)
  Dunit = g/cm3
  Dvalue = 3.3
  Group = -> [Ca_element063,O_element542]
  conduct = 2
  density = 1
  expand = 3
  formula = G4_CALCIUM_OXIDE
  name = G4_CALCIUM_OXIDE
  specific = 4
FEATURE [App::DocumentObjectGroupPython] Ca_element064  label="Ca_element : 031"  # scripted group (container) (typed FeaturePython)
  n = 1
  ref = Ca_element
FEATURE [App::DocumentObjectGroupPython] S_element099  label="S_element : 029"  # scripted group (container) (typed FeaturePython)
  n = 1
  ref = S_element
FEATURE [App::DocumentObjectGroupPython] O_element543  label="O_element : 346"  # scripted group (container) (typed FeaturePython)
  n = 4
  ref = O_element
FEATURE [App::DocumentObjectGroupPython] G4_CALCIUM_SULFATE  # scripted group (container) (typed FeaturePython)
  Dunit = g/cm3
  Dvalue = 2.96
  Group = -> [Ca_element064,S_element099,O_element543]
  conduct = 2
  density = 1
  expand = 3
  formula = G4_CALCIUM_SULFATE
  name = G4_CALCIUM_SULFATE
  specific = 4
FEATURE [App::DocumentObjectGroupPython] Ca_element065  label="Ca_element : 032"  # scripted group (container) (typed FeaturePython)
  n = 1
  ref = Ca_element
FEATURE [App::DocumentObjectGroupPython] W_element022  label="W_element : 021"  # scripted group (container) (typed FeaturePython)
  n = 1
  ref = W_element
FEATURE [App::DocumentObjectGroupPython] O_element544  label="O_element : 347"  # scripted group (container) (typed FeaturePython)
  n = 4
  ref = O_element
FEATURE [App::DocumentObjectGroupPython] G4_CALCIUM_TUNGSTATE  # scripted group (container) (typed FeaturePython)
  Dunit = g/cm3
  Dvalue = 6.062
  Group = -> [Ca_element065,W_element022,O_element544]
  conduct = 2
  density = 1
  expand = 3
  formula = G4_CALCIUM_TUNGSTATE
  name = G4_CALCIUM_TUNGSTATE
  specific = 4
FEATURE [App::DocumentObjectGroupPython] C_element615  label="C_element : 401"  # scripted group (container) (typed FeaturePython)
  n = 1
  ref = C_element
FEATURE [App::DocumentObjectGroupPython] O_element545  label="O_element : 348"  # scripted group (container) (typed FeaturePython)
  n = 2
  ref = O_element
FEATURE [App::DocumentObjectGroupPython] G4_CARBON_DIOXIDE  # scripted group (container) (typed FeaturePython)
  Dunit = g/cm3
  Dvalue = 0.00184212
  Group = -> [C_element615,O_element545]
  conduct = 2
  density = 1
  expand = 3
  formula = G4_CARBON_DIOXIDE
  name = G4_CARBON_DIOXIDE
  specific = 4
FEATURE [App::DocumentObjectGroupPython] C_element616  label="C_element : 402"  # scripted group (container) (typed FeaturePython)
  n = 1
  ref = C_element
FEATURE [App::DocumentObjectGroupPython] Cl_element124  label="Cl_element : 061"  # scripted group (container) (typed FeaturePython)
  n = 4
  ref = Cl_element
FEATURE [App::DocumentObjectGroupPython] G4_CARBON_TETRACHLORIDE  # scripted group (container) (typed FeaturePython)
  Dunit = g/cm3
  Dvalue = 1.594
  Group = -> [C_element616,Cl_element124]
  conduct = 2
  density = 1
  expand = 3
  formula = G4_CARBON_TETRACHLORIDE
  name = G4_CARBON_TETRACHLORIDE
  specific = 4
FEATURE [App::DocumentObjectGroupPython] C_element617  label="C_element : 403"  # scripted group (container) (typed FeaturePython)
  n = 6
  ref = C_element
FEATURE [App::DocumentObjectGroupPython] H_element573  label="H_element : 368"  # scripted group (container) (typed FeaturePython)
  n = 10
  ref = H_element
FEATURE [App::DocumentObjectGroupPython] O_element546  label="O_element : 349"  # scripted group (container) (typed FeaturePython)
  n = 5
  ref = O_element
FEATURE [App::DocumentObjectGroupPython] G4_CELLULOSE_CELLOPHANE  # scripted group (container) (typed FeaturePython)
  Dunit = g/cm3
  Dvalue = 1.42
  Group = -> [C_element617,H_element573,O_element546]
  conduct = 2
  density = 1
  expand = 3
  formula = G4_CELLULOSE_CELLOPHANE
  name = G4_CELLULOSE_CELLOPHANE
  specific = 4
FEATURE [App::DocumentObjectGroupPython] H_element574  label="H_element : 0.256"  # scripted group (container) (typed FeaturePython)
  n = 0.067125
FEATURE [App::DocumentObjectGroupPython] C_element618  label="C_element : 0.985"  # scripted group (container) (typed FeaturePython)
  n = 0.545403
FEATURE [App::DocumentObjectGroupPython] O_element547  label="O_element : 0.977"  # scripted group (container) (typed FeaturePython)
  n = 0.387472
FEATURE [App::DocumentObjectGroupPython] G4_CELLULOSE_BUTYRATE  # scripted group (container) (typed FeaturePython)
  Dunit = g/cm3
  Dvalue = 1.2
  Group = -> [H_element574,C_element618,O_element547]
  conduct = 2
  density = 1
  expand = 3
  formula = G4_CELLULOSE_BUTYRATE
  name = G4_CELLULOSE_BUTYRATE
  specific = 4
FEATURE [App::DocumentObjectGroupPython] H_element575  label="H_element : 0.257"  # scripted group (container) (typed FeaturePython)
  n = 0.029216
FEATURE [App::DocumentObjectGroupPython] C_element619  label="C_element : 0.986"  # scripted group (container) (typed FeaturePython)
  n = 0.271296
FEATURE [App::DocumentObjectGroupPython] N_element285  label="N_element : 0.836"  # scripted group (container) (typed FeaturePython)
  n = 0.121276
FEATURE [App::DocumentObjectGroupPython] O_element548  label="O_element : 0.978"  # scripted group (container) (typed FeaturePython)
  n = 0.578212
FEATURE [App::DocumentObjectGroupPython] G4_CELLULOSE_NITRATE  # scripted group (container) (typed FeaturePython)
  Dunit = g/cm3
  Dvalue = 1.49
  Group = -> [H_element575,C_element619,N_element285,O_element548]
  conduct = 2
  density = 1
  expand = 3
  formula = G4_CELLULOSE_NITRATE
  name = G4_CELLULOSE_NITRATE
  specific = 4
FEATURE [App::DocumentObjectGroupPython] H_element576  label="H_element : 0.258"  # scripted group (container) (typed FeaturePython)
  n = 0.107596
FEATURE [App::DocumentObjectGroupPython] N_element286  label="N_element : 0.837"  # scripted group (container) (typed FeaturePython)
  n = 0.0008
FEATURE [App::DocumentObjectGroupPython] O_element549  label="O_element : 0.979"  # scripted group (container) (typed FeaturePython)
  n = 0.874976
FEATURE [App::DocumentObjectGroupPython] S_element100  label="S_element : 0.070"  # scripted group (container) (typed FeaturePython)
  n = 0.014627
FEATURE [App::DocumentObjectGroupPython] Ce_element009  label="Ce_element : 0.005"  # scripted group (container) (typed FeaturePython)
  n = 0.002001
FEATURE [App::DocumentObjectGroupPython] G4_CERIC_SULFATE  # scripted group (container) (typed FeaturePython)
  Dunit = g/cm3
  Dvalue = 1.03
  Group = -> [H_element576,N_element286,O_element549,S_element100,Ce_element009]
  conduct = 2
  density = 1
  expand = 3
  formula = G4_CERIC_SULFATE
  name = G4_CERIC_SULFATE
  specific = 4
FEATURE [App::DocumentObjectGroupPython] Cs_element013  label="Cs_element : 012"  # scripted group (container) (typed FeaturePython)
  n = 1
  ref = Cs_element
FEATURE [App::DocumentObjectGroupPython] F_element082  label="F_element : 039"  # scripted group (container) (typed FeaturePython)
  n = 1
  ref = F_element
FEATURE [App::DocumentObjectGroupPython] G4_CESIUM_FLUORIDE  # scripted group (container) (typed FeaturePython)
  Dunit = g/cm3
  Dvalue = 4.115
  Group = -> [Cs_element013,F_element082]
  conduct = 2
  density = 1
  expand = 3
  formula = G4_CESIUM_FLUORIDE
  name = G4_CESIUM_FLUORIDE
  specific = 4
FEATURE [App::DocumentObjectGroupPython] Cs_element014  label="Cs_element : 013"  # scripted group (container) (typed FeaturePython)
  n = 1
  ref = Cs_element
FEATURE [App::DocumentObjectGroupPython] I_element041  label="I_element : 026"  # scripted group (container) (typed FeaturePython)
  n = 1
  ref = I_element
FEATURE [App::DocumentObjectGroupPython] G4_CESIUM_IODIDE  # scripted group (container) (typed FeaturePython)
  Dunit = g/cm3
  Dvalue = 4.51
  Group = -> [Cs_element014,I_element041]
  conduct = 2
  density = 1
  expand = 3
  formula = G4_CESIUM_IODIDE
  name = G4_CESIUM_IODIDE
  specific = 4
FEATURE [App::DocumentObjectGroupPython] C_element620  label="C_element : 404"  # scripted group (container) (typed FeaturePython)
  n = 6
  ref = C_element
FEATURE [App::DocumentObjectGroupPython] H_element577  label="H_element : 369"  # scripted group (container) (typed FeaturePython)
  n = 5
  ref = H_element
FEATURE [App::DocumentObjectGroupPython] Cl_element125  label="Cl_element : 062"  # scripted group (container) (typed FeaturePython)
  n = 1
  ref = Cl_element
FEATURE [App::DocumentObjectGroupPython] G4_CHLOROBENZENE  # scripted group (container) (typed FeaturePython)
  Dunit = g/cm3
  Dvalue = 1.1058
  Group = -> [C_element620,H_element577,Cl_element125]
  conduct = 2
  density = 1
  expand = 3
  formula = G4_CHLOROBENZENE
  name = G4_CHLOROBENZENE
  specific = 4
FEATURE [App::DocumentObjectGroupPython] C_element621  label="C_element : 405"  # scripted group (container) (typed FeaturePython)
  n = 1
  ref = C_element
FEATURE [App::DocumentObjectGroupPython] H_element578  label="H_element : 370"  # scripted group (container) (typed FeaturePython)
  n = 1
  ref = H_element
FEATURE [App::DocumentObjectGroupPython] Cl_element126  label="Cl_element : 063"  # scripted group (container) (typed FeaturePython)
  n = 3
  ref = Cl_element
FEATURE [App::DocumentObjectGroupPython] G4_CHLOROFORM  # scripted group (container) (typed FeaturePython)
  Dunit = g/cm3
  Dvalue = 1.4832
  Group = -> [C_element621,H_element578,Cl_element126]
  conduct = 2
  density = 1
  expand = 3
  formula = G4_CHLOROFORM
  name = G4_CHLOROFORM
  specific = 4
FEATURE [App::DocumentObjectGroupPython] H_element579  label="H_element : 0.259"  # scripted group (container) (typed FeaturePython)
  n = 0.01
FEATURE [App::DocumentObjectGroupPython] C_element622  label="C_element : 0.987"  # scripted group (container) (typed FeaturePython)
  n = 0.001
FEATURE [App::DocumentObjectGroupPython] O_element550  label="O_element : 0.980"  # scripted group (container) (typed FeaturePython)
  n = 0.529107
FEATURE [App::DocumentObjectGroupPython] Na_element085  label="Na_element : 0.146"  # scripted group (container) (typed FeaturePython)
  n = 0.016
FEATURE [App::DocumentObjectGroupPython] Mg_element047  label="Mg_element : 0.152"  # scripted group (container) (typed FeaturePython)
  n = 0.002
FEATURE [App::DocumentObjectGroupPython] Al_element018  label="Al_element : 0.039"  # scripted group (container) (typed FeaturePython)
  n = 0.033872
FEATURE [App::DocumentObjectGroupPython] Si_element030  label="Si_element : 0.391"  # scripted group (container) (typed FeaturePython)
  n = 0.337021
FEATURE [App::DocumentObjectGroupPython] K_element055  label="K_element : 0.046"  # scripted group (container) (typed FeaturePython)
  n = 0.013
FEATURE [App::DocumentObjectGroupPython] Ca_element066  label="Ca_element : 0.244"  # scripted group (container) (typed FeaturePython)
  n = 0.044
FEATURE [App::DocumentObjectGroupPython] Fe_element034  label="Fe_element : 0.022"  # scripted group (container) (typed FeaturePython)
  n = 0.014
FEATURE [App::DocumentObjectGroupPython] G4_CONCRETE  # scripted group (container) (typed FeaturePython)
  Dunit = g/cm3
  Dvalue = 2.3
  Group = -> [H_element579,C_element622,O_element550,Na_element085,Mg_element047,Al_element018,Si_element030,K_element055,Ca_element066,Fe_element034]
  conduct = 2
  density = 1
  expand = 3
  formula = G4_CONCRETE
  name = G4_CONCRETE
  specific = 4
FEATURE [App::DocumentObjectGroupPython] C_element623  label="C_element : 406"  # scripted group (container) (typed FeaturePython)
  n = 6
  ref = C_element
FEATURE [App::DocumentObjectGroupPython] H_element580  label="H_element : 371"  # scripted group (container) (typed FeaturePython)
  n = 12
  ref = H_element
FEATURE [App::DocumentObjectGroupPython] G4_CYCLOHEXANE  # scripted group (container) (typed FeaturePython)
  Dunit = g/cm3
  Dvalue = 0.779
  Group = -> [C_element623,H_element580]
  conduct = 2
  density = 1
  expand = 3
  formula = G4_CYCLOHEXANE
  name = G4_CYCLOHEXANE
  specific = 4
FEATURE [App::DocumentObjectGroupPython] C_element624  label="C_element : 407"  # scripted group (container) (typed FeaturePython)
  n = 6
  ref = C_element
FEATURE [App::DocumentObjectGroupPython] H_element581  label="H_element : 372"  # scripted group (container) (typed FeaturePython)
  n = 4
  ref = H_element
FEATURE [App::DocumentObjectGroupPython] Cl_element127  label="Cl_element : 064"  # scripted group (container) (typed FeaturePython)
  n = 2
  ref = Cl_element
FEATURE [App::DocumentObjectGroupPython] G4_1_2_DICHLOROBENZENE  label="G4_1.2-DICHLOROBENZENE"  # scripted group (container) (typed FeaturePython)
  Dunit = g/cm3
  Dvalue = 1.3048
  Group = -> [C_element624,H_element581,Cl_element127]
  conduct = 2
  density = 1
  expand = 3
  formula = G4_1.2-DICHLOROBENZENE
  name = G4_1.2-DICHLOROBENZENE
  specific = 4
FEATURE [App::DocumentObjectGroupPython] C_element625  label="C_element : 408"  # scripted group (container) (typed FeaturePython)
  n = 4
  ref = C_element
FEATURE [App::DocumentObjectGroupPython] H_element582  label="H_element : 373"  # scripted group (container) (typed FeaturePython)
  n = 8
  ref = H_element
FEATURE [App::DocumentObjectGroupPython] O_element551  label="O_element : 350"  # scripted group (container) (typed FeaturePython)
  n = 1
  ref = O_element
FEATURE [App::DocumentObjectGroupPython] Cl_element128  label="Cl_element : 065"  # scripted group (container) (typed FeaturePython)
  n = 2
  ref = Cl_element
FEATURE [App::DocumentObjectGroupPython] G4_DICHLORODIETHYL_ETHER  # scripted group (container) (typed FeaturePython)
  Dunit = g/cm3
  Dvalue = 1.2199
  Group = -> [C_element625,H_element582,O_element551,Cl_element128]
  conduct = 2
  density = 1
  expand = 3
  formula = G4_DICHLORODIETHYL_ETHER
  name = G4_DICHLORODIETHYL_ETHER
  specific = 4
FEATURE [App::DocumentObjectGroupPython] C_element626  label="C_element : 409"  # scripted group (container) (typed FeaturePython)
  n = 2
  ref = C_element
FEATURE [App::DocumentObjectGroupPython] H_element583  label="H_element : 374"  # scripted group (container) (typed FeaturePython)
  n = 4
  ref = H_element
FEATURE [App::DocumentObjectGroupPython] Cl_element129  label="Cl_element : 066"  # scripted group (container) (typed FeaturePython)
  n = 2
  ref = Cl_element
FEATURE [App::DocumentObjectGroupPython] G4_1_2_DICHLOROETHANE  label="G4_1.2-DICHLOROETHANE"  # scripted group (container) (typed FeaturePython)
  Dunit = g/cm3
  Dvalue = 1.2351
  Group = -> [C_element626,H_element583,Cl_element129]
  conduct = 2
  density = 1
  expand = 3
  formula = G4_1.2-DICHLOROETHANE
  name = G4_1.2-DICHLOROETHANE
  specific = 4
FEATURE [App::DocumentObjectGroupPython] C_element627  label="C_element : 410"  # scripted group (container) (typed FeaturePython)
  n = 4
  ref = C_element
FEATURE [App::DocumentObjectGroupPython] H_element584  label="H_element : 375"  # scripted group (container) (typed FeaturePython)
  n = 10
  ref = H_element
FEATURE [App::DocumentObjectGroupPython] O_element552  label="O_element : 351"  # scripted group (container) (typed FeaturePython)
  n = 1
  ref = O_element
FEATURE [App::DocumentObjectGroupPython] G4_DIETHYL_ETHER  # scripted group (container) (typed FeaturePython)
  Dunit = g/cm3
  Dvalue = 0.71378
  Group = -> [C_element627,H_element584,O_element552]
  conduct = 2
  density = 1
  expand = 3
  formula = G4_DIETHYL_ETHER
  name = G4_DIETHYL_ETHER
  specific = 4
FEATURE [App::DocumentObjectGroupPython] C_element628  label="C_element : 411"  # scripted group (container) (typed FeaturePython)
  n = 3
  ref = C_element
FEATURE [App::DocumentObjectGroupPython] H_element585  label="H_element : 376"  # scripted group (container) (typed FeaturePython)
  n = 7
  ref = H_element
FEATURE [App::DocumentObjectGroupPython] N_element287  label="N_element : 158"  # scripted group (container) (typed FeaturePython)
  n = 1
  ref = N_element
FEATURE [App::DocumentObjectGroupPython] O_element553  label="O_element : 352"  # scripted group (container) (typed FeaturePython)
  n = 1
  ref = O_element
FEATURE [App::DocumentObjectGroupPython] G4_N_N_DIMETHYL_FORMAMIDE  label="G4_N.N-DIMETHYL_FORMAMIDE"  # scripted group (container) (typed FeaturePython)
  Dunit = g/cm3
  Dvalue = 0.9487
  Group = -> [C_element628,H_element585,N_element287,O_element553]
  conduct = 2
  density = 1
  expand = 3
  formula = G4_N.N-DIMETHYL_FORMAMIDE
  name = G4_N.N-DIMETHYL_FORMAMIDE
  specific = 4
FEATURE [App::DocumentObjectGroupPython] C_element629  label="C_element : 412"  # scripted group (container) (typed FeaturePython)
  n = 2
  ref = C_element
FEATURE [App::DocumentObjectGroupPython] H_element586  label="H_element : 377"  # scripted group (container) (typed FeaturePython)
  n = 6
  ref = H_element
FEATURE [App::DocumentObjectGroupPython] O_element554  label="O_element : 353"  # scripted group (container) (typed FeaturePython)
  n = 1
  ref = O_element
FEATURE [App::DocumentObjectGroupPython] S_element101  label="S_element : 030"  # scripted group (container) (typed FeaturePython)
  n = 1
  ref = S_element
FEATURE [App::DocumentObjectGroupPython] G4_DIMETHYL_SULFOXIDE  # scripted group (container) (typed FeaturePython)
  Dunit = g/cm3
  Dvalue = 1.1014
  Group = -> [C_element629,H_element586,O_element554,S_element101]
  conduct = 2
  density = 1
  expand = 3
  formula = G4_DIMETHYL_SULFOXIDE
  name = G4_DIMETHYL_SULFOXIDE
  specific = 4
FEATURE [App::DocumentObjectGroupPython] C_element630  label="C_element : 413"  # scripted group (container) (typed FeaturePython)
  n = 2
  ref = C_element
FEATURE [App::DocumentObjectGroupPython] H_element587  label="H_element : 378"  # scripted group (container) (typed FeaturePython)
  n = 6
  ref = H_element
FEATURE [App::DocumentObjectGroupPython] G4_ETHANE  # scripted group (container) (typed FeaturePython)
  Dunit = g/cm3
  Dvalue = 0.00125324
  Group = -> [C_element630,H_element587]
  conduct = 2
  density = 1
  expand = 3
  formula = G4_ETHANE
  name = G4_ETHANE
  specific = 4
FEATURE [App::DocumentObjectGroupPython] C_element631  label="C_element : 414"  # scripted group (container) (typed FeaturePython)
  n = 2
  ref = C_element
FEATURE [App::DocumentObjectGroupPython] H_element588  label="H_element : 379"  # scripted group (container) (typed FeaturePython)
  n = 6
  ref = H_element
FEATURE [App::DocumentObjectGroupPython] O_element555  label="O_element : 354"  # scripted group (container) (typed FeaturePython)
  n = 1
  ref = O_element
FEATURE [App::DocumentObjectGroupPython] G4_ETHYL_ALCOHOL  # scripted group (container) (typed FeaturePython)
  Dunit = g/cm3
  Dvalue = 0.7893
  Group = -> [C_element631,H_element588,O_element555]
  conduct = 2
  density = 1
  expand = 3
  formula = G4_ETHYL_ALCOHOL
  name = G4_ETHYL_ALCOHOL
  specific = 4
FEATURE [App::DocumentObjectGroupPython] H_element589  label="H_element : 0.260"  # scripted group (container) (typed FeaturePython)
  n = 0.090027
FEATURE [App::DocumentObjectGroupPython] C_element632  label="C_element : 0.988"  # scripted group (container) (typed FeaturePython)
  n = 0.585182
FEATURE [App::DocumentObjectGroupPython] O_element556  label="O_element : 0.981"  # scripted group (container) (typed FeaturePython)
  n = 0.324791
FEATURE [App::DocumentObjectGroupPython] G4_ETHYL_CELLULOSE  # scripted group (container) (typed FeaturePython)
  Dunit = g/cm3
  Dvalue = 1.13
  Group = -> [H_element589,C_element632,O_element556]
  conduct = 2
  density = 1
  expand = 3
  formula = G4_ETHYL_CELLULOSE
  name = G4_ETHYL_CELLULOSE
  specific = 4
FEATURE [App::DocumentObjectGroupPython] C_element633  label="C_element : 415"  # scripted group (container) (typed FeaturePython)
  n = 2
  ref = C_element
FEATURE [App::DocumentObjectGroupPython] H_element590  label="H_element : 380"  # scripted group (container) (typed FeaturePython)
  n = 4
  ref = H_element
FEATURE [App::DocumentObjectGroupPython] G4_ETHYLENE  # scripted group (container) (typed FeaturePython)
  Dunit = g/cm3
  Dvalue = 0.00117497
  Group = -> [C_element633,H_element590]
  conduct = 2
  density = 1
  expand = 3
  formula = G4_ETHYLENE
  name = G4_ETHYLENE
  specific = 4
FEATURE [App::DocumentObjectGroupPython] H_element591  label="H_element : 0.261"  # scripted group (container) (typed FeaturePython)
  n = 0.096
FEATURE [App::DocumentObjectGroupPython] C_element634  label="C_element : 0.989"  # scripted group (container) (typed FeaturePython)
  n = 0.195
FEATURE [App::DocumentObjectGroupPython] N_element288  label="N_element : 0.838"  # scripted group (container) (typed FeaturePython)
  n = 0.057
FEATURE [App::DocumentObjectGroupPython] O_element557  label="O_element : 0.982"  # scripted group (container) (typed FeaturePython)
  n = 0.646
FEATURE [App::DocumentObjectGroupPython] Na_element086  label="Na_element : 0.147"  # scripted group (container) (typed FeaturePython)
  n = 0.001
FEATURE [App::DocumentObjectGroupPython] P_element081  label="P_element : 0.142"  # scripted group (container) (typed FeaturePython)
  n = 0.001
FEATURE [App::DocumentObjectGroupPython] S_element102  label="S_element : 0.071"  # scripted group (container) (typed FeaturePython)
  n = 0.003
FEATURE [App::DocumentObjectGroupPython] Cl_element130  label="Cl_element : 0.630"  # scripted group (container) (typed FeaturePython)
  n = 0.001
FEATURE [App::DocumentObjectGroupPython] G4_EYE_LENS_ICRP  # scripted group (container) (typed FeaturePython)
  Dunit = g/cm3
  Dvalue = 1.07
  Group = -> [H_element591,C_element634,N_element288,O_element557,Na_element086,P_element081,S_element102,Cl_element130]
  conduct = 2
  density = 1
  expand = 3
  formula = G4_EYE_LENS_ICRP
  name = G4_EYE_LENS_ICRP
  specific = 4
FEATURE [App::DocumentObjectGroupPython] Fe_element035  label="Fe_element : 017"  # scripted group (container) (typed FeaturePython)
  n = 2
  ref = Fe_element
FEATURE [App::DocumentObjectGroupPython] O_element558  label="O_element : 355"  # scripted group (container) (typed FeaturePython)
  n = 3
  ref = O_element
FEATURE [App::DocumentObjectGroupPython] G4_FERRIC_OXIDE  # scripted group (container) (typed FeaturePython)
  Dunit = g/cm3
  Dvalue = 5.2
  Group = -> [Fe_element035,O_element558]
  conduct = 2
  density = 1
  expand = 3
  formula = G4_FERRIC_OXIDE
  name = G4_FERRIC_OXIDE
  specific = 4
FEATURE [App::DocumentObjectGroupPython] Fe_element036  label="Fe_element : 018"  # scripted group (container) (typed FeaturePython)
  n = 1
  ref = Fe_element
FEATURE [App::DocumentObjectGroupPython] B_element031  label="B_element : 025"  # scripted group (container) (typed FeaturePython)
  n = 1
  ref = B_element
FEATURE [App::DocumentObjectGroupPython] G4_FERROBORIDE  # scripted group (container) (typed FeaturePython)
  Dunit = g/cm3
  Dvalue = 7.15
  Group = -> [Fe_element036,B_element031]
  conduct = 2
  density = 1
  expand = 3
  formula = G4_FERROBORIDE
  name = G4_FERROBORIDE
  specific = 4
FEATURE [App::DocumentObjectGroupPython] Fe_element037  label="Fe_element : 019"  # scripted group (container) (typed FeaturePython)
  n = 1
  ref = Fe_element
FEATURE [App::DocumentObjectGroupPython] O_element559  label="O_element : 356"  # scripted group (container) (typed FeaturePython)
  n = 1
  ref = O_element
FEATURE [App::DocumentObjectGroupPython] G4_FERROUS_OXIDE  # scripted group (container) (typed FeaturePython)
  Dunit = g/cm3
  Dvalue = 5.7
  Group = -> [Fe_element037,O_element559]
  conduct = 2
  density = 1
  expand = 3
  formula = G4_FERROUS_OXIDE
  name = G4_FERROUS_OXIDE
  specific = 4
FEATURE [App::DocumentObjectGroupPython] H_element592  label="H_element : 0.262"  # scripted group (container) (typed FeaturePython)
  n = 0.108259
FEATURE [App::DocumentObjectGroupPython] N_element289  label="N_element : 0.839"  # scripted group (container) (typed FeaturePython)
  n = 2.7e-05
FEATURE [App::DocumentObjectGroupPython] O_element560  label="O_element : 0.983"  # scripted group (container) (typed FeaturePython)
  n = 0.878636
FEATURE [App::DocumentObjectGroupPython] Na_element087  label="Na_element : 0.148"  # scripted group (container) (typed FeaturePython)
  n = 2.2e-05
FEATURE [App::DocumentObjectGroupPython] S_element103  label="S_element : 0.072"  # scripted group (container) (typed FeaturePython)
  n = 0.012968
FEATURE [App::DocumentObjectGroupPython] Cl_element131  label="Cl_element : 0.631"  # scripted group (container) (typed FeaturePython)
  n = 3.4e-05
FEATURE [App::DocumentObjectGroupPython] Fe_element038  label="Fe_element : 0.023"  # scripted group (container) (typed FeaturePython)
  n = 5.4e-05
FEATURE [App::DocumentObjectGroupPython] G4_FERROUS_SULFATE  # scripted group (container) (typed FeaturePython)
  Dunit = g/cm3
  Dvalue = 1.024
  Group = -> [H_element592,N_element289,O_element560,Na_element087,S_element103,Cl_element131,Fe_element038]
  conduct = 2
  density = 1
  expand = 3
  formula = G4_FERROUS_SULFATE
  name = G4_FERROUS_SULFATE
  specific = 4
FEATURE [App::DocumentObjectGroupPython] C_element635  label="C_element : 0.990"  # scripted group (container) (typed FeaturePython)
  n = 0.099335
FEATURE [App::DocumentObjectGroupPython] F_element083  label="F_element : 0.730"  # scripted group (container) (typed FeaturePython)
  n = 0.314247
FEATURE [App::DocumentObjectGroupPython] Cl_element132  label="Cl_element : 0.632"  # scripted group (container) (typed FeaturePython)
  n = 0.586418
FEATURE [App::DocumentObjectGroupPython] G4_FREON_12  label="G4_FREON-12"  # scripted group (container) (typed FeaturePython)
  Dunit = g/cm3
  Dvalue = 1.12
  Group = -> [C_element635,F_element083,Cl_element132]
  conduct = 2
  density = 1
  expand = 3
  formula = G4_FREON-12
  name = G4_FREON-12
  specific = 4
FEATURE [App::DocumentObjectGroupPython] C_element636  label="C_element : 0.991"  # scripted group (container) (typed FeaturePython)
  n = 0.057245
FEATURE [App::DocumentObjectGroupPython] F_element084  label="F_element : 0.731"  # scripted group (container) (typed FeaturePython)
  n = 0.181096
FEATURE [App::DocumentObjectGroupPython] Br_element029  label="Br_element : 0.769"  # scripted group (container) (typed FeaturePython)
  n = 0.761659
FEATURE [App::DocumentObjectGroupPython] G4_FREON_12B2  label="G4_FREON-12B2"  # scripted group (container) (typed FeaturePython)
  Dunit = g/cm3
  Dvalue = 1.8
  Group = -> [C_element636,F_element084,Br_element029]
  conduct = 2
  density = 1
  expand = 3
  formula = G4_FREON-12B2
  name = G4_FREON-12B2
  specific = 4
FEATURE [App::DocumentObjectGroupPython] C_element637  label="C_element : 0.992"  # scripted group (container) (typed FeaturePython)
  n = 0.114983
FEATURE [App::DocumentObjectGroupPython] F_element085  label="F_element : 0.732"  # scripted group (container) (typed FeaturePython)
  n = 0.545621
FEATURE [App::DocumentObjectGroupPython] Cl_element133  label="Cl_element : 0.633"  # scripted group (container) (typed FeaturePython)
  n = 0.339396
FEATURE [App::DocumentObjectGroupPython] G4_FREON_13  label="G4_FREON-13"  # scripted group (container) (typed FeaturePython)
  Dunit = g/cm3
  Dvalue = 0.95
  Group = -> [C_element637,F_element085,Cl_element133]
  conduct = 2
  density = 1
  expand = 3
  formula = G4_FREON-13
  name = G4_FREON-13
  specific = 4
FEATURE [App::DocumentObjectGroupPython] C_element638  label="C_element : 416"  # scripted group (container) (typed FeaturePython)
  n = 1
  ref = C_element
FEATURE [App::DocumentObjectGroupPython] F_element086  label="F_element : 040"  # scripted group (container) (typed FeaturePython)
  n = 3
  ref = F_element
FEATURE [App::DocumentObjectGroupPython] Br_element030  label="Br_element : 016"  # scripted group (container) (typed FeaturePython)
  n = 1
  ref = Br_element
FEATURE [App::DocumentObjectGroupPython] G4_FREON_13B1  label="G4_FREON-13B1"  # scripted group (container) (typed FeaturePython)
  Dunit = g/cm3
  Dvalue = 1.5
  Group = -> [C_element638,F_element086,Br_element030]
  conduct = 2
  density = 1
  expand = 3
  formula = G4_FREON-13B1
  name = G4_FREON-13B1
  specific = 4
FEATURE [App::DocumentObjectGroupPython] C_element639  label="C_element : 0.993"  # scripted group (container) (typed FeaturePython)
  n = 0.061309
FEATURE [App::DocumentObjectGroupPython] F_element087  label="F_element : 0.733"  # scripted group (container) (typed FeaturePython)
  n = 0.290924
FEATURE [App::DocumentObjectGroupPython] I_element042  label="I_element : 0.657"  # scripted group (container) (typed FeaturePython)
  n = 0.647767
FEATURE [App::DocumentObjectGroupPython] G4_FREON_13I1  label="G4_FREON-13I1"  # scripted group (container) (typed FeaturePython)
  Dunit = g/cm3
  Dvalue = 1.8
  Group = -> [C_element639,F_element087,I_element042]
  conduct = 2
  density = 1
  expand = 3
  formula = G4_FREON-13I1
  name = G4_FREON-13I1
  specific = 4
FEATURE [App::DocumentObjectGroupPython] Gd_element009  label="Gd_element : 007"  # scripted group (container) (typed FeaturePython)
  n = 2
  ref = Gd_element
FEATURE [App::DocumentObjectGroupPython] O_element561  label="O_element : 357"  # scripted group (container) (typed FeaturePython)
  n = 2
  ref = O_element
FEATURE [App::DocumentObjectGroupPython] S_element104  label="S_element : 031"  # scripted group (container) (typed FeaturePython)
  n = 1
  ref = S_element
FEATURE [App::DocumentObjectGroupPython] G4_GADOLINIUM_OXYSULFIDE  # scripted group (container) (typed FeaturePython)
  Dunit = g/cm3
  Dvalue = 7.44
  Group = -> [Gd_element009,O_element561,S_element104]
  conduct = 2
  density = 1
  expand = 3
  formula = G4_GADOLINIUM_OXYSULFIDE
  name = G4_GADOLINIUM_OXYSULFIDE
  specific = 4
FEATURE [App::DocumentObjectGroupPython] Ga_element009  label="Ga_element : 008"  # scripted group (container) (typed FeaturePython)
  n = 1
  ref = Ga_element
FEATURE [App::DocumentObjectGroupPython] As_element013  label="As_element : 008"  # scripted group (container) (typed FeaturePython)
  n = 1
  ref = As_element
FEATURE [App::DocumentObjectGroupPython] G4_GALLIUM_ARSENIDE  # scripted group (container) (typed FeaturePython)
  Dunit = g/cm3
  Dvalue = 5.31
  Group = -> [Ga_element009,As_element013]
  conduct = 2
  density = 1
  expand = 3
  formula = G4_GALLIUM_ARSENIDE
  name = G4_GALLIUM_ARSENIDE
  specific = 4
FEATURE [App::DocumentObjectGroupPython] H_element593  label="H_element : 0.263"  # scripted group (container) (typed FeaturePython)
  n = 0.08118
FEATURE [App::DocumentObjectGroupPython] C_element640  label="C_element : 0.994"  # scripted group (container) (typed FeaturePython)
  n = 0.41606
FEATURE [App::DocumentObjectGroupPython] N_element290  label="N_element : 0.840"  # scripted group (container) (typed FeaturePython)
  n = 0.11124
FEATURE [App::DocumentObjectGroupPython] O_element562  label="O_element : 0.984"  # scripted group (container) (typed FeaturePython)
  n = 0.38064
FEATURE [App::DocumentObjectGroupPython] S_element105  label="S_element : 0.073"  # scripted group (container) (typed FeaturePython)
  n = 0.01088
FEATURE [App::DocumentObjectGroupPython] G4_GEL_PHOTO_EMULSION  # scripted group (container) (typed FeaturePython)
  Dunit = g/cm3
  Dvalue = 1.2914
  Group = -> [H_element593,C_element640,N_element290,O_element562,S_element105]
  conduct = 2
  density = 1
  expand = 3
  formula = G4_GEL_PHOTO_EMULSION
  name = G4_GEL_PHOTO_EMULSION
  specific = 4
FEATURE [App::DocumentObjectGroupPython] B_element032  label="B_element : 0.043"  # scripted group (container) (typed FeaturePython)
  n = 0.0400639
FEATURE [App::DocumentObjectGroupPython] O_element563  label="O_element : 0.985"  # scripted group (container) (typed FeaturePython)
  n = 0.539561
FEATURE [App::DocumentObjectGroupPython] Na_element088  label="Na_element : 0.149"  # scripted group (container) (typed FeaturePython)
  n = 0.0281909
FEATURE [App::DocumentObjectGroupPython] Al_element019  label="Al_element : 0.040"  # scripted group (container) (typed FeaturePython)
  n = 0.011644
FEATURE [App::DocumentObjectGroupPython] Si_element031  label="Si_element : 0.392"  # scripted group (container) (typed FeaturePython)
  n = 0.377219
FEATURE [App::DocumentObjectGroupPython] K_element056  label="K_element : 0.047"  # scripted group (container) (typed FeaturePython)
  n = 0.00332099
FEATURE [App::DocumentObjectGroupPython] G4_Pyrex_Glass  # scripted group (container) (typed FeaturePython)
  Dunit = g/cm3
  Dvalue = 2.23
  Group = -> [B_element032,O_element563,Na_element088,Al_element019,Si_element031,K_element056]
  conduct = 2
  density = 1
  expand = 3
  formula = G4_Pyrex_Glass
  name = G4_Pyrex_Glass
  specific = 4
FEATURE [App::DocumentObjectGroupPython] O_element564  label="O_element : 0.986"  # scripted group (container) (typed FeaturePython)
  n = 0.156453
FEATURE [App::DocumentObjectGroupPython] Si_element032  label="Si_element : 0.393"  # scripted group (container) (typed FeaturePython)
  n = 0.080866
FEATURE [App::DocumentObjectGroupPython] Ti_element017  label="Ti_element : 0.019"  # scripted group (container) (typed FeaturePython)
  n = 0.008092
FEATURE [App::DocumentObjectGroupPython] As_element014  label="As_element : 0.006"  # scripted group (container) (typed FeaturePython)
  n = 0.002651
FEATURE [App::DocumentObjectGroupPython] Pb_element025  label="Pb_element : 0.933"  # scripted group (container) (typed FeaturePython)
  n = 0.751938
FEATURE [App::DocumentObjectGroupPython] G4_GLASS_LEAD  # scripted group (container) (typed FeaturePython)
  Dunit = g/cm3
  Dvalue = 6.22
  Group = -> [O_element564,Si_element032,Ti_element017,As_element014,Pb_element025]
  conduct = 2
  density = 1
  expand = 3
  formula = G4_GLASS_LEAD
  name = G4_GLASS_LEAD
  specific = 4
FEATURE [App::DocumentObjectGroupPython] O_element565  label="O_element : 0.987"  # scripted group (container) (typed FeaturePython)
  n = 0.4598
FEATURE [App::DocumentObjectGroupPython] Na_element089  label="Na_element : 0.150"  # scripted group (container) (typed FeaturePython)
  n = 0.0964411
FEATURE [App::DocumentObjectGroupPython] Si_element033  label="Si_element : 0.394"  # scripted group (container) (typed FeaturePython)
  n = 0.336553
FEATURE [App::DocumentObjectGroupPython] Ca_element067  label="Ca_element : 0.245"  # scripted group (container) (typed FeaturePython)
  n = 0.107205
FEATURE [App::DocumentObjectGroupPython] G4_GLASS_PLATE  # scripted group (container) (typed FeaturePython)
  Dunit = g/cm3
  Dvalue = 2.4
  Group = -> [O_element565,Na_element089,Si_element033,Ca_element067]
  conduct = 2
  density = 1
  expand = 3
  formula = G4_GLASS_PLATE
  name = G4_GLASS_PLATE
  specific = 4
FEATURE [App::DocumentObjectGroupPython] C_element641  label="C_element : 417"  # scripted group (container) (typed FeaturePython)
  n = 5
  ref = C_element
FEATURE [App::DocumentObjectGroupPython] H_element594  label="H_element : 381"  # scripted group (container) (typed FeaturePython)
  n = 10
  ref = H_element
FEATURE [App::DocumentObjectGroupPython] N_element291  label="N_element : 159"  # scripted group (container) (typed FeaturePython)
  n = 2
  ref = N_element
FEATURE [App::DocumentObjectGroupPython] O_element566  label="O_element : 358"  # scripted group (container) (typed FeaturePython)
  n = 3
  ref = O_element
FEATURE [App::DocumentObjectGroupPython] G4_GLUTAMINE  # scripted group (container) (typed FeaturePython)
  Dunit = g/cm3
  Dvalue = 1.46
  Group = -> [C_element641,H_element594,N_element291,O_element566]
  conduct = 2
  density = 1
  expand = 3
  formula = G4_GLUTAMINE
  name = G4_GLUTAMINE
  specific = 4
FEATURE [App::DocumentObjectGroupPython] C_element642  label="C_element : 418"  # scripted group (container) (typed FeaturePython)
  n = 3
  ref = C_element
FEATURE [App::DocumentObjectGroupPython] H_element595  label="H_element : 382"  # scripted group (container) (typed FeaturePython)
  n = 8
  ref = H_element
FEATURE [App::DocumentObjectGroupPython] O_element567  label="O_element : 359"  # scripted group (container) (typed FeaturePython)
  n = 3
  ref = O_element
FEATURE [App::DocumentObjectGroupPython] G4_GLYCEROL  # scripted group (container) (typed FeaturePython)
  Dunit = g/cm3
  Dvalue = 1.2613
  Group = -> [C_element642,H_element595,O_element567]
  conduct = 2
  density = 1
  expand = 3
  formula = G4_GLYCEROL
  name = G4_GLYCEROL
  specific = 4
FEATURE [App::DocumentObjectGroupPython] C_element643  label="C_element : 419"  # scripted group (container) (typed FeaturePython)
  n = 5
  ref = C_element
FEATURE [App::DocumentObjectGroupPython] H_element596  label="H_element : 383"  # scripted group (container) (typed FeaturePython)
  n = 5
  ref = H_element
FEATURE [App::DocumentObjectGroupPython] N_element292  label="N_element : 160"  # scripted group (container) (typed FeaturePython)
  n = 5
  ref = N_element
FEATURE [App::DocumentObjectGroupPython] O_element568  label="O_element : 360"  # scripted group (container) (typed FeaturePython)
  n = 1
  ref = O_element
FEATURE [App::DocumentObjectGroupPython] G4_GUANINE  # scripted group (container) (typed FeaturePython)
  Dunit = g/cm3
  Dvalue = 2.2
  Group = -> [C_element643,H_element596,N_element292,O_element568]
  conduct = 2
  density = 1
  expand = 3
  formula = G4_GUANINE
  name = G4_GUANINE
  specific = 4
FEATURE [App::DocumentObjectGroupPython] Ca_element068  label="Ca_element : 033"  # scripted group (container) (typed FeaturePython)
  n = 1
  ref = Ca_element
FEATURE [App::DocumentObjectGroupPython] S_element106  label="S_element : 032"  # scripted group (container) (typed FeaturePython)
  n = 1
  ref = S_element
FEATURE [App::DocumentObjectGroupPython] O_element569  label="O_element : 361"  # scripted group (container) (typed FeaturePython)
  n = 6
  ref = O_element
FEATURE [App::DocumentObjectGroupPython] H_element597  label="H_element : 384"  # scripted group (container) (typed FeaturePython)
  n = 4
  ref = H_element
FEATURE [App::DocumentObjectGroupPython] G4_GYPSUM  # scripted group (container) (typed FeaturePython)
  Dunit = g/cm3
  Dvalue = 2.32
  Group = -> [Ca_element068,S_element106,O_element569,H_element597]
  conduct = 2
  density = 1
  expand = 3
  formula = G4_GYPSUM
  name = G4_GYPSUM
  specific = 4
FEATURE [App::DocumentObjectGroupPython] C_element644  label="C_element : 420"  # scripted group (container) (typed FeaturePython)
  n = 7
  ref = C_element
FEATURE [App::DocumentObjectGroupPython] H_element598  label="H_element : 385"  # scripted group (container) (typed FeaturePython)
  n = 16
  ref = H_element
FEATURE [App::DocumentObjectGroupPython] G4_N_HEPTANE  label="G4_N-HEPTANE"  # scripted group (container) (typed FeaturePython)
  Dunit = g/cm3
  Dvalue = 0.68376
  Group = -> [C_element644,H_element598]
  conduct = 2
  density = 1
  expand = 3
  formula = G4_N-HEPTANE
  name = G4_N-HEPTANE
  specific = 4
FEATURE [App::DocumentObjectGroupPython] C_element645  label="C_element : 421"  # scripted group (container) (typed FeaturePython)
  n = 6
  ref = C_element
FEATURE [App::DocumentObjectGroupPython] H_element599  label="H_element : 386"  # scripted group (container) (typed FeaturePython)
  n = 14
  ref = H_element
FEATURE [App::DocumentObjectGroupPython] G4_N_HEXANE  label="G4_N-HEXANE"  # scripted group (container) (typed FeaturePython)
  Dunit = g/cm3
  Dvalue = 0.6603
  Group = -> [C_element645,H_element599]
  conduct = 2
  density = 1
  expand = 3
  formula = G4_N-HEXANE
  name = G4_N-HEXANE
  specific = 4
FEATURE [App::DocumentObjectGroupPython] C_element646  label="C_element : 422"  # scripted group (container) (typed FeaturePython)
  n = 22
  ref = C_element
FEATURE [App::DocumentObjectGroupPython] H_element600  label="H_element : 387"  # scripted group (container) (typed FeaturePython)
  n = 10
  ref = H_element
FEATURE [App::DocumentObjectGroupPython] N_element293  label="N_element : 161"  # scripted group (container) (typed FeaturePython)
  n = 2
  ref = N_element
FEATURE [App::DocumentObjectGroupPython] O_element570  label="O_element : 362"  # scripted group (container) (typed FeaturePython)
  n = 5
  ref = O_element
FEATURE [App::DocumentObjectGroupPython] G4_KAPTON  # scripted group (container) (typed FeaturePython)
  Dunit = g/cm3
  Dvalue = 1.42
  Group = -> [C_element646,H_element600,N_element293,O_element570]
  conduct = 2
  density = 1
  expand = 3
  formula = G4_KAPTON
  name = G4_KAPTON
  specific = 4
FEATURE [App::DocumentObjectGroupPython] La_element013  label="La_element : 011"  # scripted group (container) (typed FeaturePython)
  n = 1
  ref = La_element
FEATURE [App::DocumentObjectGroupPython] Br_element031  label="Br_element : 017"  # scripted group (container) (typed FeaturePython)
  n = 1
  ref = Br_element
FEATURE [App::DocumentObjectGroupPython] O_element571  label="O_element : 363"  # scripted group (container) (typed FeaturePython)
  n = 1
  ref = O_element
FEATURE [App::DocumentObjectGroupPython] G4_LANTHANUM_OXYBROMIDE  # scripted group (container) (typed FeaturePython)
  Dunit = g/cm3
  Dvalue = 6.28
  Group = -> [La_element013,Br_element031,O_element571]
  conduct = 2
  density = 1
  expand = 3
  formula = G4_LANTHANUM_OXYBROMIDE
  name = G4_LANTHANUM_OXYBROMIDE
  specific = 4
FEATURE [App::DocumentObjectGroupPython] La_element014  label="La_element : 012"  # scripted group (container) (typed FeaturePython)
  n = 2
  ref = La_element
FEATURE [App::DocumentObjectGroupPython] O_element572  label="O_element : 364"  # scripted group (container) (typed FeaturePython)
  n = 2
  ref = O_element
FEATURE [App::DocumentObjectGroupPython] S_element107  label="S_element : 033"  # scripted group (container) (typed FeaturePython)
  n = 1
  ref = S_element
FEATURE [App::DocumentObjectGroupPython] G4_LANTHANUM_OXYSULFIDE  # scripted group (container) (typed FeaturePython)
  Dunit = g/cm3
  Dvalue = 5.86
  Group = -> [La_element014,O_element572,S_element107]
  conduct = 2
  density = 1
  expand = 3
  formula = G4_LANTHANUM_OXYSULFIDE
  name = G4_LANTHANUM_OXYSULFIDE
  specific = 4
FEATURE [App::DocumentObjectGroupPython] O_element573  label="O_element : 0.988"  # scripted group (container) (typed FeaturePython)
  n = 0.071682
FEATURE [App::DocumentObjectGroupPython] Pb_element026  label="Pb_element : 0.934"  # scripted group (container) (typed FeaturePython)
  n = 0.928318
FEATURE [App::DocumentObjectGroupPython] G4_LEAD_OXIDE  # scripted group (container) (typed FeaturePython)
  Dunit = g/cm3
  Dvalue = 9.53
  Group = -> [O_element573,Pb_element026]
  conduct = 2
  density = 1
  expand = 3
  formula = G4_LEAD_OXIDE
  name = G4_LEAD_OXIDE
  specific = 4
FEATURE [App::DocumentObjectGroupPython] Li_element033  label="Li_element : 031"  # scripted group (container) (typed FeaturePython)
  n = 1
  ref = Li_element
FEATURE [App::DocumentObjectGroupPython] N_element294  label="N_element : 162"  # scripted group (container) (typed FeaturePython)
  n = 1
  ref = N_element
FEATURE [App::DocumentObjectGroupPython] H_element601  label="H_element : 388"  # scripted group (container) (typed FeaturePython)
  n = 2
  ref = H_element
FEATURE [App::DocumentObjectGroupPython] G4_LITHIUM_AMIDE  # scripted group (container) (typed FeaturePython)
  Dunit = g/cm3
  Dvalue = 1.178
  Group = -> [Li_element033,N_element294,H_element601]
  conduct = 2
  density = 1
  expand = 3
  formula = G4_LITHIUM_AMIDE
  name = G4_LITHIUM_AMIDE
  specific = 4
FEATURE [App::DocumentObjectGroupPython] Li_element034  label="Li_element : 032"  # scripted group (container) (typed FeaturePython)
  n = 2
  ref = Li_element
FEATURE [App::DocumentObjectGroupPython] C_element647  label="C_element : 423"  # scripted group (container) (typed FeaturePython)
  n = 1
  ref = C_element
FEATURE [App::DocumentObjectGroupPython] O_element574  label="O_element : 365"  # scripted group (container) (typed FeaturePython)
  n = 3
  ref = O_element
FEATURE [App::DocumentObjectGroupPython] G4_LITHIUM_CARBONATE  # scripted group (container) (typed FeaturePython)
  Dunit = g/cm3
  Dvalue = 2.11
  Group = -> [Li_element034,C_element647,O_element574]
  conduct = 2
  density = 1
  expand = 3
  formula = G4_LITHIUM_CARBONATE
  name = G4_LITHIUM_CARBONATE
  specific = 4
FEATURE [App::DocumentObjectGroupPython] Li_element035  label="Li_element : 033"  # scripted group (container) (typed FeaturePython)
  n = 1
  ref = Li_element
FEATURE [App::DocumentObjectGroupPython] F_element088  label="F_element : 041"  # scripted group (container) (typed FeaturePython)
  n = 1
  ref = F_element
FEATURE [App::DocumentObjectGroupPython] G4_LITHIUM_FLUORIDE  # scripted group (container) (typed FeaturePython)
  Dunit = g/cm3
  Dvalue = 2.635
  Group = -> [Li_element035,F_element088]
  conduct = 2
  density = 1
  expand = 3
  formula = G4_LITHIUM_FLUORIDE
  name = G4_LITHIUM_FLUORIDE
  specific = 4
FEATURE [App::DocumentObjectGroupPython] Li_element036  label="Li_element : 034"  # scripted group (container) (typed FeaturePython)
  n = 1
  ref = Li_element
FEATURE [App::DocumentObjectGroupPython] H_element602  label="H_element : 389"  # scripted group (container) (typed FeaturePython)
  n = 1
  ref = H_element
FEATURE [App::DocumentObjectGroupPython] G4_LITHIUM_HYDRIDE  # scripted group (container) (typed FeaturePython)
  Dunit = g/cm3
  Dvalue = 0.82
  Group = -> [Li_element036,H_element602]
  conduct = 2
  density = 1
  expand = 3
  formula = G4_LITHIUM_HYDRIDE
  name = G4_LITHIUM_HYDRIDE
  specific = 4
FEATURE [App::DocumentObjectGroupPython] Li_element037  label="Li_element : 035"  # scripted group (container) (typed FeaturePython)
  n = 1
  ref = Li_element
FEATURE [App::DocumentObjectGroupPython] I_element043  label="I_element : 027"  # scripted group (container) (typed FeaturePython)
  n = 1
  ref = I_element
FEATURE [App::DocumentObjectGroupPython] G4_LITHIUM_IODIDE  # scripted group (container) (typed FeaturePython)
  Dunit = g/cm3
  Dvalue = 3.494
  Group = -> [Li_element037,I_element043]
  conduct = 2
  density = 1
  expand = 3
  formula = G4_LITHIUM_IODIDE
  name = G4_LITHIUM_IODIDE
  specific = 4
FEATURE [App::DocumentObjectGroupPython] Li_element038  label="Li_element : 036"  # scripted group (container) (typed FeaturePython)
  n = 2
  ref = Li_element
FEATURE [App::DocumentObjectGroupPython] O_element575  label="O_element : 366"  # scripted group (container) (typed FeaturePython)
  n = 1
  ref = O_element
FEATURE [App::DocumentObjectGroupPython] G4_LITHIUM_OXIDE  # scripted group (container) (typed FeaturePython)
  Dunit = g/cm3
  Dvalue = 2.013
  Group = -> [Li_element038,O_element575]
  conduct = 2
  density = 1
  expand = 3
  formula = G4_LITHIUM_OXIDE
  name = G4_LITHIUM_OXIDE
  specific = 4
FEATURE [App::DocumentObjectGroupPython] Li_element039  label="Li_element : 037"  # scripted group (container) (typed FeaturePython)
  n = 2
  ref = Li_element
FEATURE [App::DocumentObjectGroupPython] B_element033  label="B_element : 026"  # scripted group (container) (typed FeaturePython)
  n = 4
  ref = B_element
FEATURE [App::DocumentObjectGroupPython] O_element576  label="O_element : 367"  # scripted group (container) (typed FeaturePython)
  n = 7
  ref = O_element
FEATURE [App::DocumentObjectGroupPython] G4_LITHIUM_TETRABORATE  # scripted group (container) (typed FeaturePython)
  Dunit = g/cm3
  Dvalue = 2.44
  Group = -> [Li_element039,B_element033,O_element576]
  conduct = 2
  density = 1
  expand = 3
  formula = G4_LITHIUM_TETRABORATE
  name = G4_LITHIUM_TETRABORATE
  specific = 4
FEATURE [App::DocumentObjectGroupPython] H_element603  label="H_element : 0.264"  # scripted group (container) (typed FeaturePython)
  n = 0.105
FEATURE [App::DocumentObjectGroupPython] C_element648  label="C_element : 0.995"  # scripted group (container) (typed FeaturePython)
  n = 0.083
FEATURE [App::DocumentObjectGroupPython] N_element295  label="N_element : 0.841"  # scripted group (container) (typed FeaturePython)
  n = 0.023
FEATURE [App::DocumentObjectGroupPython] O_element577  label="O_element : 0.989"  # scripted group (container) (typed FeaturePython)
  n = 0.779
FEATURE [App::DocumentObjectGroupPython] Na_element090  label="Na_element : 0.151"  # scripted group (container) (typed FeaturePython)
  n = 0.002
FEATURE [App::DocumentObjectGroupPython] P_element082  label="P_element : 0.143"  # scripted group (container) (typed FeaturePython)
  n = 0.001
FEATURE [App::DocumentObjectGroupPython] S_element108  label="S_element : 0.074"  # scripted group (container) (typed FeaturePython)
  n = 0.002
FEATURE [App::DocumentObjectGroupPython] Cl_element134  label="Cl_element : 0.634"  # scripted group (container) (typed FeaturePython)
  n = 0.003
FEATURE [App::DocumentObjectGroupPython] K_element057  label="K_element : 0.048"  # scripted group (container) (typed FeaturePython)
  n = 0.002
FEATURE [App::DocumentObjectGroupPython] G4_LUNG_ICRP  # scripted group (container) (typed FeaturePython)
  Dunit = g/cm3
  Dvalue = 1.04
  Group = -> [H_element603,C_element648,N_element295,O_element577,Na_element090,P_element082,S_element108,Cl_element134,K_element057]
  conduct = 2
  density = 1
  expand = 3
  formula = G4_LUNG_ICRP
  name = G4_LUNG_ICRP
  specific = 4
FEATURE [App::DocumentObjectGroupPython] H_element604  label="H_element : 0.265"  # scripted group (container) (typed FeaturePython)
  n = 0.114318
FEATURE [App::DocumentObjectGroupPython] C_element649  label="C_element : 0.996"  # scripted group (container) (typed FeaturePython)
  n = 0.655824
FEATURE [App::DocumentObjectGroupPython] O_element578  label="O_element : 0.990"  # scripted group (container) (typed FeaturePython)
  n = 0.0921831
FEATURE [App::DocumentObjectGroupPython] Mg_element048  label="Mg_element : 0.153"  # scripted group (container) (typed FeaturePython)
  n = 0.134792
FEATURE [App::DocumentObjectGroupPython] Ca_element069  label="Ca_element : 0.246"  # scripted group (container) (typed FeaturePython)
  n = 0.002883
FEATURE [App::DocumentObjectGroupPython] G4_M3_WAX  # scripted group (container) (typed FeaturePython)
  Dunit = g/cm3
  Dvalue = 1.05
  Group = -> [H_element604,C_element649,O_element578,Mg_element048,Ca_element069]
  conduct = 2
  density = 1
  expand = 3
  formula = G4_M3_WAX
  name = G4_M3_WAX
  specific = 4
FEATURE [App::DocumentObjectGroupPython] Mg_element049  label="Mg_element : 020"  # scripted group (container) (typed FeaturePython)
  n = 1
  ref = Mg_element
FEATURE [App::DocumentObjectGroupPython] C_element650  label="C_element : 424"  # scripted group (container) (typed FeaturePython)
  n = 1
  ref = C_element
FEATURE [App::DocumentObjectGroupPython] O_element579  label="O_element : 368"  # scripted group (container) (typed FeaturePython)
  n = 3
  ref = O_element
FEATURE [App::DocumentObjectGroupPython] G4_MAGNESIUM_CARBONATE  # scripted group (container) (typed FeaturePython)
  Dunit = g/cm3
  Dvalue = 2.958
  Group = -> [Mg_element049,C_element650,O_element579]
  conduct = 2
  density = 1
  expand = 3
  formula = G4_MAGNESIUM_CARBONATE
  name = G4_MAGNESIUM_CARBONATE
  specific = 4
FEATURE [App::DocumentObjectGroupPython] Mg_element050  label="Mg_element : 021"  # scripted group (container) (typed FeaturePython)
  n = 1
  ref = Mg_element
FEATURE [App::DocumentObjectGroupPython] F_element089  label="F_element : 042"  # scripted group (container) (typed FeaturePython)
  n = 2
  ref = F_element
FEATURE [App::DocumentObjectGroupPython] G4_MAGNESIUM_FLUORIDE  # scripted group (container) (typed FeaturePython)
  Dunit = g/cm3
  Dvalue = 3
  Group = -> [Mg_element050,F_element089]
  conduct = 2
  density = 1
  expand = 3
  formula = G4_MAGNESIUM_FLUORIDE
  name = G4_MAGNESIUM_FLUORIDE
  specific = 4
FEATURE [App::DocumentObjectGroupPython] Mg_element051  label="Mg_element : 022"  # scripted group (container) (typed FeaturePython)
  n = 1
  ref = Mg_element
FEATURE [App::DocumentObjectGroupPython] O_element580  label="O_element : 369"  # scripted group (container) (typed FeaturePython)
  n = 1
  ref = O_element
FEATURE [App::DocumentObjectGroupPython] G4_MAGNESIUM_OXIDE  # scripted group (container) (typed FeaturePython)
  Dunit = g/cm3
  Dvalue = 3.58
  Group = -> [Mg_element051,O_element580]
  conduct = 2
  density = 1
  expand = 3
  formula = G4_MAGNESIUM_OXIDE
  name = G4_MAGNESIUM_OXIDE
  specific = 4
FEATURE [App::DocumentObjectGroupPython] Mg_element052  label="Mg_element : 023"  # scripted group (container) (typed FeaturePython)
  n = 1
  ref = Mg_element
FEATURE [App::DocumentObjectGroupPython] B_element034  label="B_element : 027"  # scripted group (container) (typed FeaturePython)
  n = 4
  ref = B_element
FEATURE [App::DocumentObjectGroupPython] O_element581  label="O_element : 370"  # scripted group (container) (typed FeaturePython)
  n = 7
  ref = O_element
FEATURE [App::DocumentObjectGroupPython] G4_MAGNESIUM_TETRABORATE  # scripted group (container) (typed FeaturePython)
  Dunit = g/cm3
  Dvalue = 2.53
  Group = -> [Mg_element052,B_element034,O_element581]
  conduct = 2
  density = 1
  expand = 3
  formula = G4_MAGNESIUM_TETRABORATE
  name = G4_MAGNESIUM_TETRABORATE
  specific = 4
FEATURE [App::DocumentObjectGroupPython] Hg_element009  label="Hg_element : 008"  # scripted group (container) (typed FeaturePython)
  n = 1
  ref = Hg_element
FEATURE [App::DocumentObjectGroupPython] I_element044  label="I_element : 028"  # scripted group (container) (typed FeaturePython)
  n = 2
  ref = I_element
FEATURE [App::DocumentObjectGroupPython] G4_MERCURIC_IODIDE  # scripted group (container) (typed FeaturePython)
  Dunit = g/cm3
  Dvalue = 6.36
  Group = -> [Hg_element009,I_element044]
  conduct = 2
  density = 1
  expand = 3
  formula = G4_MERCURIC_IODIDE
  name = G4_MERCURIC_IODIDE
  specific = 4
FEATURE [App::DocumentObjectGroupPython] C_element651  label="C_element : 425"  # scripted group (container) (typed FeaturePython)
  n = 1
  ref = C_element
FEATURE [App::DocumentObjectGroupPython] H_element605  label="H_element : 390"  # scripted group (container) (typed FeaturePython)
  n = 4
  ref = H_element
FEATURE [App::DocumentObjectGroupPython] G4_METHANE  # scripted group (container) (typed FeaturePython)
  Dunit = g/cm3
  Dvalue = 0.000667151
  Group = -> [C_element651,H_element605]
  conduct = 2
  density = 1
  expand = 3
  formula = G4_METHANE
  name = G4_METHANE
  specific = 4
FEATURE [App::DocumentObjectGroupPython] C_element652  label="C_element : 426"  # scripted group (container) (typed FeaturePython)
  n = 1
  ref = C_element
FEATURE [App::DocumentObjectGroupPython] H_element606  label="H_element : 391"  # scripted group (container) (typed FeaturePython)
  n = 4
  ref = H_element
FEATURE [App::DocumentObjectGroupPython] O_element582  label="O_element : 371"  # scripted group (container) (typed FeaturePython)
  n = 1
  ref = O_element
FEATURE [App::DocumentObjectGroupPython] G4_METHANOL  # scripted group (container) (typed FeaturePython)
  Dunit = g/cm3
  Dvalue = 0.7914
  Group = -> [C_element652,H_element606,O_element582]
  conduct = 2
  density = 1
  expand = 3
  formula = G4_METHANOL
  name = G4_METHANOL
  specific = 4
FEATURE [App::DocumentObjectGroupPython] H_element607  label="H_element : 0.266"  # scripted group (container) (typed FeaturePython)
  n = 0.13404
FEATURE [App::DocumentObjectGroupPython] C_element653  label="C_element : 0.997"  # scripted group (container) (typed FeaturePython)
  n = 0.77796
FEATURE [App::DocumentObjectGroupPython] O_element583  label="O_element : 0.991"  # scripted group (container) (typed FeaturePython)
  n = 0.03502
FEATURE [App::DocumentObjectGroupPython] Mg_element053  label="Mg_element : 0.154"  # scripted group (container) (typed FeaturePython)
  n = 0.038594
FEATURE [App::DocumentObjectGroupPython] Ti_element018  label="Ti_element : 0.020"  # scripted group (container) (typed FeaturePython)
  n = 0.014386
FEATURE [App::DocumentObjectGroupPython] G4_MIX_D_WAX  # scripted group (container) (typed FeaturePython)
  Dunit = g/cm3
  Dvalue = 0.99
  Group = -> [H_element607,C_element653,O_element583,Mg_element053,Ti_element018]
  conduct = 2
  density = 1
  expand = 3
  formula = G4_MIX_D_WAX
  name = G4_MIX_D_WAX
  specific = 4
FEATURE [App::DocumentObjectGroupPython] H_element608  label="H_element : 0.267"  # scripted group (container) (typed FeaturePython)
  n = 0.081192
FEATURE [App::DocumentObjectGroupPython] C_element654  label="C_element : 0.998"  # scripted group (container) (typed FeaturePython)
  n = 0.583442
FEATURE [App::DocumentObjectGroupPython] N_element296  label="N_element : 0.842"  # scripted group (container) (typed FeaturePython)
  n = 0.017798
FEATURE [App::DocumentObjectGroupPython] O_element584  label="O_element : 0.992"  # scripted group (container) (typed FeaturePython)
  n = 0.186381
FEATURE [App::DocumentObjectGroupPython] Mg_element054  label="Mg_element : 0.155"  # scripted group (container) (typed FeaturePython)
  n = 0.130287
FEATURE [App::DocumentObjectGroupPython] Cl_element135  label="Cl_element : 0.635"  # scripted group (container) (typed FeaturePython)
  n = 0.0009
FEATURE [App::DocumentObjectGroupPython] G4_MS20_TISSUE  # scripted group (container) (typed FeaturePython)
  Dunit = g/cm3
  Dvalue = 1
  Group = -> [H_element608,C_element654,N_element296,O_element584,Mg_element054,Cl_element135]
  conduct = 2
  density = 1
  expand = 3
  formula = G4_MS20_TISSUE
  name = G4_MS20_TISSUE
  specific = 4
FEATURE [App::DocumentObjectGroupPython] H_element609  label="H_element : 0.268"  # scripted group (container) (typed FeaturePython)
  n = 0.102
FEATURE [App::DocumentObjectGroupPython] C_element655  label="C_element : 0.999"  # scripted group (container) (typed FeaturePython)
  n = 0.143
FEATURE [App::DocumentObjectGroupPython] N_element297  label="N_element : 0.843"  # scripted group (container) (typed FeaturePython)
  n = 0.034
FEATURE [App::DocumentObjectGroupPython] O_element585  label="O_element : 0.993"  # scripted group (container) (typed FeaturePython)
  n = 0.71
FEATURE [App::DocumentObjectGroupPython] Na_element091  label="Na_element : 0.152"  # scripted group (container) (typed FeaturePython)
  n = 0.001
FEATURE [App::DocumentObjectGroupPython] P_element083  label="P_element : 0.144"  # scripted group (container) (typed FeaturePython)
  n = 0.002
FEATURE [App::DocumentObjectGroupPython] S_element109  label="S_element : 0.075"  # scripted group (container) (typed FeaturePython)
  n = 0.003
FEATURE [App::DocumentObjectGroupPython] Cl_element136  label="Cl_element : 0.636"  # scripted group (container) (typed FeaturePython)
  n = 0.001
FEATURE [App::DocumentObjectGroupPython] K_element058  label="K_element : 0.049"  # scripted group (container) (typed FeaturePython)
  n = 0.004
FEATURE [App::DocumentObjectGroupPython] G4_MUSCLE_SKELETAL_ICRP  # scripted group (container) (typed FeaturePython)
  Dunit = g/cm3
  Dvalue = 1.05
  Group = -> [H_element609,C_element655,N_element297,O_element585,Na_element091,P_element083,S_element109,Cl_element136,K_element058]
  conduct = 2
  density = 1
  expand = 3
  formula = G4_MUSCLE_SKELETAL_ICRP
  name = G4_MUSCLE_SKELETAL_ICRP
  specific = 4
FEATURE [App::DocumentObjectGroupPython] H_element610  label="H_element : 0.269"  # scripted group (container) (typed FeaturePython)
  n = 0.102102
FEATURE [App::DocumentObjectGroupPython] C_element656  label="C_element : 0.1000"  # scripted group (container) (typed FeaturePython)
  n = 0.123123
FEATURE [App::DocumentObjectGroupPython] N_element298  label="N_element : 0.844"  # scripted group (container) (typed FeaturePython)
  n = 0.035035
FEATURE [App::DocumentObjectGroupPython] O_element586  label="O_element : 0.994"  # scripted group (container) (typed FeaturePython)
  n = 0.72973
FEATURE [App::DocumentObjectGroupPython] Na_element092  label="Na_element : 0.153"  # scripted group (container) (typed FeaturePython)
  n = 0.001001
FEATURE [App::DocumentObjectGroupPython] P_element084  label="P_element : 0.145"  # scripted group (container) (typed FeaturePython)
  n = 0.002002
FEATURE [App::DocumentObjectGroupPython] S_element110  label="S_element : 0.076"  # scripted group (container) (typed FeaturePython)
  n = 0.004004
FEATURE [App::DocumentObjectGroupPython] K_element059  label="K_element : 0.050"  # scripted group (container) (typed FeaturePython)
  n = 0.003003
FEATURE [App::DocumentObjectGroupPython] G4_MUSCLE_STRIATED_ICRU  # scripted group (container) (typed FeaturePython)
  Dunit = g/cm3
  Dvalue = 1.04
  Group = -> [H_element610,C_element656,N_element298,O_element586,Na_element092,P_element084,S_element110,K_element059]
  conduct = 2
  density = 1
  expand = 3
  formula = G4_MUSCLE_STRIATED_ICRU
  name = G4_MUSCLE_STRIATED_ICRU
  specific = 4
FEATURE [App::DocumentObjectGroupPython] H_element611  label="H_element : 0.270"  # scripted group (container) (typed FeaturePython)
  n = 0.0982341
FEATURE [App::DocumentObjectGroupPython] C_element657  label="C_element : 0.1001"  # scripted group (container) (typed FeaturePython)
  n = 0.156214
FEATURE [App::DocumentObjectGroupPython] N_element299  label="N_element : 0.845"  # scripted group (container) (typed FeaturePython)
  n = 0.035451
FEATURE [App::DocumentObjectGroupPython] O_element587  label="O_element : 0.995"  # scripted group (container) (typed FeaturePython)
  n = 0.710101
FEATURE [App::DocumentObjectGroupPython] G4_MUSCLE_WITH_SUCROSE  # scripted group (container) (typed FeaturePython)
  Dunit = g/cm3
  Dvalue = 1.11
  Group = -> [H_element611,C_element657,N_element299,O_element587]
  conduct = 2
  density = 1
  expand = 3
  formula = G4_MUSCLE_WITH_SUCROSE
  name = G4_MUSCLE_WITH_SUCROSE
  specific = 4
FEATURE [App::DocumentObjectGroupPython] H_element612  label="H_element : 0.271"  # scripted group (container) (typed FeaturePython)
  n = 0.101969
FEATURE [App::DocumentObjectGroupPython] C_element658  label="C_element : 0.1002"  # scripted group (container) (typed FeaturePython)
  n = 0.120058
FEATURE [App::DocumentObjectGroupPython] N_element300  label="N_element : 0.846"  # scripted group (container) (typed FeaturePython)
  n = 0.035451
FEATURE [App::DocumentObjectGroupPython] O_element588  label="O_element : 0.996"  # scripted group (container) (typed FeaturePython)
  n = 0.742522
FEATURE [App::DocumentObjectGroupPython] G4_MUSCLE_WITHOUT_SUCROSE  # scripted group (container) (typed FeaturePython)
  Dunit = g/cm3
  Dvalue = 1.07
  Group = -> [H_element612,C_element658,N_element300,O_element588]
  conduct = 2
  density = 1
  expand = 3
  formula = G4_MUSCLE_WITHOUT_SUCROSE
  name = G4_MUSCLE_WITHOUT_SUCROSE
  specific = 4
FEATURE [App::DocumentObjectGroupPython] C_element659  label="C_element : 427"  # scripted group (container) (typed FeaturePython)
  n = 10
  ref = C_element
FEATURE [App::DocumentObjectGroupPython] H_element613  label="H_element : 392"  # scripted group (container) (typed FeaturePython)
  n = 8
  ref = H_element
FEATURE [App::DocumentObjectGroupPython] G4_NAPHTHALENE  # scripted group (container) (typed FeaturePython)
  Dunit = g/cm3
  Dvalue = 1.145
  Group = -> [C_element659,H_element613]
  conduct = 2
  density = 1
  expand = 3
  formula = G4_NAPHTHALENE
  name = G4_NAPHTHALENE
  specific = 4
FEATURE [App::DocumentObjectGroupPython] C_element660  label="C_element : 428"  # scripted group (container) (typed FeaturePython)
  n = 6
  ref = C_element
FEATURE [App::DocumentObjectGroupPython] H_element614  label="H_element : 393"  # scripted group (container) (typed FeaturePython)
  n = 5
  ref = H_element
FEATURE [App::DocumentObjectGroupPython] N_element301  label="N_element : 163"  # scripted group (container) (typed FeaturePython)
  n = 1
  ref = N_element
FEATURE [App::DocumentObjectGroupPython] O_element589  label="O_element : 372"  # scripted group (container) (typed FeaturePython)
  n = 2
  ref = O_element
FEATURE [App::DocumentObjectGroupPython] G4_NITROBENZENE  # scripted group (container) (typed FeaturePython)
  Dunit = g/cm3
  Dvalue = 1.19867
  Group = -> [C_element660,H_element614,N_element301,O_element589]
  conduct = 2
  density = 1
  expand = 3
  formula = G4_NITROBENZENE
  name = G4_NITROBENZENE
  specific = 4
FEATURE [App::DocumentObjectGroupPython] N_element302  label="N_element : 164"  # scripted group (container) (typed FeaturePython)
  n = 2
  ref = N_element
FEATURE [App::DocumentObjectGroupPython] O_element590  label="O_element : 373"  # scripted group (container) (typed FeaturePython)
  n = 1
  ref = O_element
FEATURE [App::DocumentObjectGroupPython] G4_NITROUS_OXIDE  # scripted group (container) (typed FeaturePython)
  Dunit = g/cm3
  Dvalue = 0.00183094
  Group = -> [N_element302,O_element590]
  conduct = 2
  density = 1
  expand = 3
  formula = G4_NITROUS_OXIDE
  name = G4_NITROUS_OXIDE
  specific = 4
FEATURE [App::DocumentObjectGroupPython] H_element615  label="H_element : 0.272"  # scripted group (container) (typed FeaturePython)
  n = 0.103509
FEATURE [App::DocumentObjectGroupPython] C_element661  label="C_element : 0.1003"  # scripted group (container) (typed FeaturePython)
  n = 0.648416
FEATURE [App::DocumentObjectGroupPython] N_element303  label="N_element : 0.847"  # scripted group (container) (typed FeaturePython)
  n = 0.0995361
FEATURE [App::DocumentObjectGroupPython] O_element591  label="O_element : 0.997"  # scripted group (container) (typed FeaturePython)
  n = 0.148539
FEATURE [App::DocumentObjectGroupPython] G4_NYLON_8062  label="G4_NYLON-8062"  # scripted group (container) (typed FeaturePython)
  Dunit = g/cm3
  Dvalue = 1.08
  Group = -> [H_element615,C_element661,N_element303,O_element591]
  conduct = 2
  density = 1
  expand = 3
  formula = G4_NYLON-8062
  name = G4_NYLON-8062
  specific = 4
FEATURE [App::DocumentObjectGroupPython] C_element662  label="C_element : 429"  # scripted group (container) (typed FeaturePython)
  n = 6
  ref = C_element
FEATURE [App::DocumentObjectGroupPython] H_element616  label="H_element : 394"  # scripted group (container) (typed FeaturePython)
  n = 11
  ref = H_element
FEATURE [App::DocumentObjectGroupPython] N_element304  label="N_element : 165"  # scripted group (container) (typed FeaturePython)
  n = 1
  ref = N_element
FEATURE [App::DocumentObjectGroupPython] O_element592  label="O_element : 374"  # scripted group (container) (typed FeaturePython)
  n = 1
  ref = O_element
FEATURE [App::DocumentObjectGroupPython] G4_NYLON_6_6  label="G4_NYLON-6-6"  # scripted group (container) (typed FeaturePython)
  Dunit = g/cm3
  Dvalue = 1.14
  Group = -> [C_element662,H_element616,N_element304,O_element592]
  conduct = 2
  density = 1
  expand = 3
  formula = G4_NYLON-6-6
  name = G4_NYLON-6-6
  specific = 4
FEATURE [App::DocumentObjectGroupPython] H_element617  label="H_element : 0.273"  # scripted group (container) (typed FeaturePython)
  n = 0.107062
FEATURE [App::DocumentObjectGroupPython] C_element663  label="C_element : 0.1004"  # scripted group (container) (typed FeaturePython)
  n = 0.680449
FEATURE [App::DocumentObjectGroupPython] N_element305  label="N_element : 0.848"  # scripted group (container) (typed FeaturePython)
  n = 0.099189
FEATURE [App::DocumentObjectGroupPython] O_element593  label="O_element : 0.998"  # scripted group (container) (typed FeaturePython)
  n = 0.1133
FEATURE [App::DocumentObjectGroupPython] G4_NYLON_6_10  label="G4_NYLON-6-10"  # scripted group (container) (typed FeaturePython)
  Dunit = g/cm3
  Dvalue = 1.14
  Group = -> [H_element617,C_element663,N_element305,O_element593]
  conduct = 2
  density = 1
  expand = 3
  formula = G4_NYLON-6-10
  name = G4_NYLON-6-10
  specific = 4
FEATURE [App::DocumentObjectGroupPython] H_element618  label="H_element : 0.274"  # scripted group (container) (typed FeaturePython)
  n = 0.115476
FEATURE [App::DocumentObjectGroupPython] C_element664  label="C_element : 0.1005"  # scripted group (container) (typed FeaturePython)
  n = 0.720818
FEATURE [App::DocumentObjectGroupPython] N_element306  label="N_element : 0.849"  # scripted group (container) (typed FeaturePython)
  n = 0.0764169
FEATURE [App::DocumentObjectGroupPython] O_element594  label="O_element : 0.999"  # scripted group (container) (typed FeaturePython)
  n = 0.0872889
FEATURE [App::DocumentObjectGroupPython] G4_NYLON_11_RILSAN  label="G4_NYLON-11_RILSAN"  # scripted group (container) (typed FeaturePython)
  Dunit = g/cm3
  Dvalue = 1.425
  Group = -> [H_element618,C_element664,N_element306,O_element594]
  conduct = 2
  density = 1
  expand = 3
  formula = G4_NYLON-11_RILSAN
  name = G4_NYLON-11_RILSAN
  specific = 4
FEATURE [App::DocumentObjectGroupPython] C_element665  label="C_element : 430"  # scripted group (container) (typed FeaturePython)
  n = 8
  ref = C_element
FEATURE [App::DocumentObjectGroupPython] H_element619  label="H_element : 395"  # scripted group (container) (typed FeaturePython)
  n = 18
  ref = H_element
FEATURE [App::DocumentObjectGroupPython] G4_OCTANE  # scripted group (container) (typed FeaturePython)
  Dunit = g/cm3
  Dvalue = 0.7026
  Group = -> [C_element665,H_element619]
  conduct = 2
  density = 1
  expand = 3
  formula = G4_OCTANE
  name = G4_OCTANE
  specific = 4
FEATURE [App::DocumentObjectGroupPython] C_element666  label="C_element : 431"  # scripted group (container) (typed FeaturePython)
  n = 25
  ref = C_element
FEATURE [App::DocumentObjectGroupPython] H_element620  label="H_element : 396"  # scripted group (container) (typed FeaturePython)
  n = 52
  ref = H_element
FEATURE [App::DocumentObjectGroupPython] G4_PARAFFIN  # scripted group (container) (typed FeaturePython)
  Dunit = g/cm3
  Dvalue = 0.93
  Group = -> [C_element666,H_element620]
  conduct = 2
  density = 1
  expand = 3
  formula = G4_PARAFFIN
  name = G4_PARAFFIN
  specific = 4
FEATURE [App::DocumentObjectGroupPython] C_element667  label="C_element : 432"  # scripted group (container) (typed FeaturePython)
  n = 5
  ref = C_element
FEATURE [App::DocumentObjectGroupPython] H_element621  label="H_element : 397"  # scripted group (container) (typed FeaturePython)
  n = 12
  ref = H_element
FEATURE [App::DocumentObjectGroupPython] G4_N_PENTANE  label="G4_N-PENTANE"  # scripted group (container) (typed FeaturePython)
  Dunit = g/cm3
  Dvalue = 0.6262
  Group = -> [C_element667,H_element621]
  conduct = 2
  density = 1
  expand = 3
  formula = G4_N-PENTANE
  name = G4_N-PENTANE
  specific = 4
FEATURE [App::DocumentObjectGroupPython] H_element622  label="H_element : 0.275"  # scripted group (container) (typed FeaturePython)
  n = 0.0141
FEATURE [App::DocumentObjectGroupPython] C_element668  label="C_element : 0.1006"  # scripted group (container) (typed FeaturePython)
  n = 0.072261
FEATURE [App::DocumentObjectGroupPython] N_element307  label="N_element : 0.850"  # scripted group (container) (typed FeaturePython)
  n = 0.01932
FEATURE [App::DocumentObjectGroupPython] O_element595  label="O_element : 0.1000"  # scripted group (container) (typed FeaturePython)
  n = 0.066101
FEATURE [App::DocumentObjectGroupPython] S_element111  label="S_element : 0.077"  # scripted group (container) (typed FeaturePython)
  n = 0.00189
FEATURE [App::DocumentObjectGroupPython] Br_element032  label="Br_element : 0.770"  # scripted group (container) (typed FeaturePython)
  n = 0.349103
FEATURE [App::DocumentObjectGroupPython] Ag_element025  label="Ag_element : 0.579"  # scripted group (container) (typed FeaturePython)
  n = 0.474105
FEATURE [App::DocumentObjectGroupPython] I_element045  label="I_element : 0.658"  # scripted group (container) (typed FeaturePython)
  n = 0.00312
FEATURE [App::DocumentObjectGroupPython] G4_PHOTO_EMULSION  # scripted group (container) (typed FeaturePython)
  Dunit = g/cm3
  Dvalue = 3.815
  Group = -> [H_element622,C_element668,N_element307,O_element595,S_element111,Br_element032,Ag_element025,I_element045]
  conduct = 2
  density = 1
  expand = 3
  formula = G4_PHOTO_EMULSION
  name = G4_PHOTO_EMULSION
  specific = 4
FEATURE [App::DocumentObjectGroupPython] C_element669  label="C_element : 433"  # scripted group (container) (typed FeaturePython)
  n = 9
  ref = C_element
FEATURE [App::DocumentObjectGroupPython] H_element623  label="H_element : 398"  # scripted group (container) (typed FeaturePython)
  n = 10
  ref = H_element
FEATURE [App::DocumentObjectGroupPython] G4_PLASTIC_SC_VINYLTOLUENE  # scripted group (container) (typed FeaturePython)
  Dunit = g/cm3
  Dvalue = 1.032
  Group = -> [C_element669,H_element623]
  conduct = 2
  density = 1
  expand = 3
  formula = G4_PLASTIC_SC_VINYLTOLUENE
  name = G4_PLASTIC_SC_VINYLTOLUENE
  specific = 4
FEATURE [App::DocumentObjectGroupPython] Pu_element009  label="Pu_element : 008"  # scripted group (container) (typed FeaturePython)
  n = 1
  ref = Pu_element
FEATURE [App::DocumentObjectGroupPython] O_element596  label="O_element : 375"  # scripted group (container) (typed FeaturePython)
  n = 2
  ref = O_element
FEATURE [App::DocumentObjectGroupPython] G4_PLUTONIUM_DIOXIDE  # scripted group (container) (typed FeaturePython)
  Dunit = g/cm3
  Dvalue = 11.46
  Group = -> [Pu_element009,O_element596]
  conduct = 2
  density = 1
  expand = 3
  formula = G4_PLUTONIUM_DIOXIDE
  name = G4_PLUTONIUM_DIOXIDE
  specific = 4
FEATURE [App::DocumentObjectGroupPython] C_element670  label="C_element : 434"  # scripted group (container) (typed FeaturePython)
  n = 3
  ref = C_element
FEATURE [App::DocumentObjectGroupPython] H_element624  label="H_element : 399"  # scripted group (container) (typed FeaturePython)
  n = 3
  ref = H_element
FEATURE [App::DocumentObjectGroupPython] N_element308  label="N_element : 166"  # scripted group (container) (typed FeaturePython)
  n = 1
  ref = N_element
FEATURE [App::DocumentObjectGroupPython] G4_POLYACRYLONITRILE  # scripted group (container) (typed FeaturePython)
  Dunit = g/cm3
  Dvalue = 1.17
  Group = -> [C_element670,H_element624,N_element308]
  conduct = 2
  density = 1
  expand = 3
  formula = G4_POLYACRYLONITRILE
  name = G4_POLYACRYLONITRILE
  specific = 4
FEATURE [App::DocumentObjectGroupPython] C_element671  label="C_element : 435"  # scripted group (container) (typed FeaturePython)
  n = 16
  ref = C_element
FEATURE [App::DocumentObjectGroupPython] H_element625  label="H_element : 400"  # scripted group (container) (typed FeaturePython)
  n = 14
  ref = H_element
FEATURE [App::DocumentObjectGroupPython] O_element597  label="O_element : 376"  # scripted group (container) (typed FeaturePython)
  n = 3
  ref = O_element
FEATURE [App::DocumentObjectGroupPython] G4_POLYCARBONATE  # scripted group (container) (typed FeaturePython)
  Dunit = g/cm3
  Dvalue = 1.2
  Group = -> [C_element671,H_element625,O_element597]
  conduct = 2
  density = 1
  expand = 3
  formula = G4_POLYCARBONATE
  name = G4_POLYCARBONATE
  specific = 4
FEATURE [App::DocumentObjectGroupPython] C_element672  label="C_element : 436"  # scripted group (container) (typed FeaturePython)
  n = 8
  ref = C_element
FEATURE [App::DocumentObjectGroupPython] H_element626  label="H_element : 401"  # scripted group (container) (typed FeaturePython)
  n = 7
  ref = H_element
FEATURE [App::DocumentObjectGroupPython] Cl_element137  label="Cl_element : 067"  # scripted group (container) (typed FeaturePython)
  n = 1
  ref = Cl_element
FEATURE [App::DocumentObjectGroupPython] G4_POLYCHLOROSTYRENE  # scripted group (container) (typed FeaturePython)
  Dunit = g/cm3
  Dvalue = 1.3
  Group = -> [C_element672,H_element626,Cl_element137]
  conduct = 2
  density = 1
  expand = 3
  formula = G4_POLYCHLOROSTYRENE
  name = G4_POLYCHLOROSTYRENE
  specific = 4
FEATURE [App::DocumentObjectGroupPython] C_element673  label="C_element : 437"  # scripted group (container) (typed FeaturePython)
  n = 1
  ref = C_element
FEATURE [App::DocumentObjectGroupPython] H_element627  label="H_element : 402"  # scripted group (container) (typed FeaturePython)
  n = 2
  ref = H_element
FEATURE [App::DocumentObjectGroupPython] G4_POLYETHYLENE  # scripted group (container) (typed FeaturePython)
  Dunit = g/cm3
  Dvalue = 0.94
  Group = -> [C_element673,H_element627]
  conduct = 2
  density = 1
  expand = 3
  formula = G4_POLYETHYLENE
  name = G4_POLYETHYLENE
  specific = 4
FEATURE [App::DocumentObjectGroupPython] C_element674  label="C_element : 438"  # scripted group (container) (typed FeaturePython)
  n = 10
  ref = C_element
FEATURE [App::DocumentObjectGroupPython] H_element628  label="H_element : 403"  # scripted group (container) (typed FeaturePython)
  n = 8
  ref = H_element
FEATURE [App::DocumentObjectGroupPython] O_element598  label="O_element : 377"  # scripted group (container) (typed FeaturePython)
  n = 4
  ref = O_element
FEATURE [App::DocumentObjectGroupPython] G4_MYLAR  # scripted group (container) (typed FeaturePython)
  Dunit = g/cm3
  Dvalue = 1.4
  Group = -> [C_element674,H_element628,O_element598]
  conduct = 2
  density = 1
  expand = 3
  formula = G4_MYLAR
  name = G4_MYLAR
  specific = 4
FEATURE [App::DocumentObjectGroupPython] C_element675  label="C_element : 439"  # scripted group (container) (typed FeaturePython)
  n = 5
  ref = C_element
FEATURE [App::DocumentObjectGroupPython] H_element629  label="H_element : 404"  # scripted group (container) (typed FeaturePython)
  n = 8
  ref = H_element
FEATURE [App::DocumentObjectGroupPython] O_element599  label="O_element : 378"  # scripted group (container) (typed FeaturePython)
  n = 2
  ref = O_element
FEATURE [App::DocumentObjectGroupPython] G4_PLEXIGLASS  # scripted group (container) (typed FeaturePython)
  Dunit = g/cm3
  Dvalue = 1.19
  Group = -> [C_element675,H_element629,O_element599]
  conduct = 2
  density = 1
  expand = 3
  formula = G4_PLEXIGLASS
  name = G4_PLEXIGLASS
  specific = 4
FEATURE [App::DocumentObjectGroupPython] C_element676  label="C_element : 440"  # scripted group (container) (typed FeaturePython)
  n = 1
  ref = C_element
FEATURE [App::DocumentObjectGroupPython] H_element630  label="H_element : 405"  # scripted group (container) (typed FeaturePython)
  n = 2
  ref = H_element
FEATURE [App::DocumentObjectGroupPython] O_element600  label="O_element : 379"  # scripted group (container) (typed FeaturePython)
  n = 1
  ref = O_element
FEATURE [App::DocumentObjectGroupPython] G4_POLYOXYMETHYLENE  # scripted group (container) (typed FeaturePython)
  Dunit = g/cm3
  Dvalue = 1.425
  Group = -> [C_element676,H_element630,O_element600]
  conduct = 2
  density = 1
  expand = 3
  formula = G4_POLYOXYMETHYLENE
  name = G4_POLYOXYMETHYLENE
  specific = 4
FEATURE [App::DocumentObjectGroupPython] C_element677  label="C_element : 441"  # scripted group (container) (typed FeaturePython)
  n = 2
  ref = C_element
FEATURE [App::DocumentObjectGroupPython] H_element631  label="H_element : 406"  # scripted group (container) (typed FeaturePython)
  n = 4
  ref = H_element
FEATURE [App::DocumentObjectGroupPython] G4_POLYPROPYLENE  # scripted group (container) (typed FeaturePython)
  Dunit = g/cm3
  Dvalue = 0.9
  Group = -> [C_element677,H_element631]
  conduct = 2
  density = 1
  expand = 3
  formula = G4_POLYPROPYLENE
  name = G4_POLYPROPYLENE
  specific = 4
FEATURE [App::DocumentObjectGroupPython] C_element678  label="C_element : 442"  # scripted group (container) (typed FeaturePython)
  n = 8
  ref = C_element
FEATURE [App::DocumentObjectGroupPython] H_element632  label="H_element : 407"  # scripted group (container) (typed FeaturePython)
  n = 8
  ref = H_element
FEATURE [App::DocumentObjectGroupPython] G4_POLYSTYRENE  # scripted group (container) (typed FeaturePython)
  Dunit = g/cm3
  Dvalue = 1.06
  Group = -> [C_element678,H_element632]
  conduct = 2
  density = 1
  expand = 3
  formula = G4_POLYSTYRENE
  name = G4_POLYSTYRENE
  specific = 4
FEATURE [App::DocumentObjectGroupPython] C_element679  label="C_element : 443"  # scripted group (container) (typed FeaturePython)
  n = 2
  ref = C_element
FEATURE [App::DocumentObjectGroupPython] F_element090  label="F_element : 043"  # scripted group (container) (typed FeaturePython)
  n = 4
  ref = F_element
FEATURE [App::DocumentObjectGroupPython] G4_TEFLON  # scripted group (container) (typed FeaturePython)
  Dunit = g/cm3
  Dvalue = 2.2
  Group = -> [C_element679,F_element090]
  conduct = 2
  density = 1
  expand = 3
  formula = G4_TEFLON
  name = G4_TEFLON
  specific = 4
FEATURE [App::DocumentObjectGroupPython] C_element680  label="C_element : 444"  # scripted group (container) (typed FeaturePython)
  n = 2
  ref = C_element
FEATURE [App::DocumentObjectGroupPython] F_element091  label="F_element : 044"  # scripted group (container) (typed FeaturePython)
  n = 3
  ref = F_element
FEATURE [App::DocumentObjectGroupPython] Cl_element138  label="Cl_element : 068"  # scripted group (container) (typed FeaturePython)
  n = 1
  ref = Cl_element
FEATURE [App::DocumentObjectGroupPython] G4_POLYTRIFLUOROCHLOROETHYLENE  # scripted group (container) (typed FeaturePython)
  Dunit = g/cm3
  Dvalue = 2.1
  Group = -> [C_element680,F_element091,Cl_element138]
  conduct = 2
  density = 1
  expand = 3
  formula = G4_POLYTRIFLUOROCHLOROETHYLENE
  name = G4_POLYTRIFLUOROCHLOROETHYLENE
  specific = 4
FEATURE [App::DocumentObjectGroupPython] C_element681  label="C_element : 445"  # scripted group (container) (typed FeaturePython)
  n = 4
  ref = C_element
FEATURE [App::DocumentObjectGroupPython] H_element633  label="H_element : 408"  # scripted group (container) (typed FeaturePython)
  n = 6
  ref = H_element
FEATURE [App::DocumentObjectGroupPython] O_element601  label="O_element : 380"  # scripted group (container) (typed FeaturePython)
  n = 2
  ref = O_element
FEATURE [App::DocumentObjectGroupPython] G4_POLYVINYL_ACETATE  # scripted group (container) (typed FeaturePython)
  Dunit = g/cm3
  Dvalue = 1.19
  Group = -> [C_element681,H_element633,O_element601]
  conduct = 2
  density = 1
  expand = 3
  formula = G4_POLYVINYL_ACETATE
  name = G4_POLYVINYL_ACETATE
  specific = 4
FEATURE [App::DocumentObjectGroupPython] C_element682  label="C_element : 446"  # scripted group (container) (typed FeaturePython)
  n = 2
  ref = C_element
FEATURE [App::DocumentObjectGroupPython] H_element634  label="H_element : 409"  # scripted group (container) (typed FeaturePython)
  n = 4
  ref = H_element
FEATURE [App::DocumentObjectGroupPython] O_element602  label="O_element : 381"  # scripted group (container) (typed FeaturePython)
  n = 1
  ref = O_element
FEATURE [App::DocumentObjectGroupPython] G4_POLYVINYL_ALCOHOL  # scripted group (container) (typed FeaturePython)
  Dunit = g/cm3
  Dvalue = 1.3
  Group = -> [C_element682,H_element634,O_element602]
  conduct = 2
  density = 1
  expand = 3
  formula = G4_POLYVINYL_ALCOHOL
  name = G4_POLYVINYL_ALCOHOL
  specific = 4
FEATURE [App::DocumentObjectGroupPython] C_element683  label="C_element : 447"  # scripted group (container) (typed FeaturePython)
  n = 8
  ref = C_element
FEATURE [App::DocumentObjectGroupPython] H_element635  label="H_element : 410"  # scripted group (container) (typed FeaturePython)
  n = 14
  ref = H_element
FEATURE [App::DocumentObjectGroupPython] O_element603  label="O_element : 382"  # scripted group (container) (typed FeaturePython)
  n = 2
  ref = O_element
FEATURE [App::DocumentObjectGroupPython] G4_POLYVINYL_BUTYRAL  # scripted group (container) (typed FeaturePython)
  Dunit = g/cm3
  Dvalue = 1.12
  Group = -> [C_element683,H_element635,O_element603]
  conduct = 2
  density = 1
  expand = 3
  formula = G4_POLYVINYL_BUTYRAL
  name = G4_POLYVINYL_BUTYRAL
  specific = 4
FEATURE [App::DocumentObjectGroupPython] C_element684  label="C_element : 448"  # scripted group (container) (typed FeaturePython)
  n = 2
  ref = C_element
FEATURE [App::DocumentObjectGroupPython] H_element636  label="H_element : 411"  # scripted group (container) (typed FeaturePython)
  n = 3
  ref = H_element
FEATURE [App::DocumentObjectGroupPython] Cl_element139  label="Cl_element : 069"  # scripted group (container) (typed FeaturePython)
  n = 1
  ref = Cl_element
FEATURE [App::DocumentObjectGroupPython] G4_POLYVINYL_CHLORIDE  # scripted group (container) (typed FeaturePython)
  Dunit = g/cm3
  Dvalue = 1.3
  Group = -> [C_element684,H_element636,Cl_element139]
  conduct = 2
  density = 1
  expand = 3
  formula = G4_POLYVINYL_CHLORIDE
  name = G4_POLYVINYL_CHLORIDE
  specific = 4
FEATURE [App::DocumentObjectGroupPython] C_element685  label="C_element : 449"  # scripted group (container) (typed FeaturePython)
  n = 2
  ref = C_element
FEATURE [App::DocumentObjectGroupPython] H_element637  label="H_element : 412"  # scripted group (container) (typed FeaturePython)
  n = 2
  ref = H_element
FEATURE [App::DocumentObjectGroupPython] Cl_element140  label="Cl_element : 070"  # scripted group (container) (typed FeaturePython)
  n = 2
  ref = Cl_element
FEATURE [App::DocumentObjectGroupPython] G4_POLYVINYLIDENE_CHLORIDE  # scripted group (container) (typed FeaturePython)
  Dunit = g/cm3
  Dvalue = 1.7
  Group = -> [C_element685,H_element637,Cl_element140]
  conduct = 2
  density = 1
  expand = 3
  formula = G4_POLYVINYLIDENE_CHLORIDE
  name = G4_POLYVINYLIDENE_CHLORIDE
  specific = 4
FEATURE [App::DocumentObjectGroupPython] C_element686  label="C_element : 450"  # scripted group (container) (typed FeaturePython)
  n = 2
  ref = C_element
FEATURE [App::DocumentObjectGroupPython] H_element638  label="H_element : 413"  # scripted group (container) (typed FeaturePython)
  n = 2
  ref = H_element
FEATURE [App::DocumentObjectGroupPython] F_element092  label="F_element : 045"  # scripted group (container) (typed FeaturePython)
  n = 2
  ref = F_element
FEATURE [App::DocumentObjectGroupPython] G4_POLYVINYLIDENE_FLUORIDE  # scripted group (container) (typed FeaturePython)
  Dunit = g/cm3
  Dvalue = 1.76
  Group = -> [C_element686,H_element638,F_element092]
  conduct = 2
  density = 1
  expand = 3
  formula = G4_POLYVINYLIDENE_FLUORIDE
  name = G4_POLYVINYLIDENE_FLUORIDE
  specific = 4
FEATURE [App::DocumentObjectGroupPython] C_element687  label="C_element : 451"  # scripted group (container) (typed FeaturePython)
  n = 6
  ref = C_element
FEATURE [App::DocumentObjectGroupPython] H_element639  label="H_element : 414"  # scripted group (container) (typed FeaturePython)
  n = 9
  ref = H_element
FEATURE [App::DocumentObjectGroupPython] N_element309  label="N_element : 167"  # scripted group (container) (typed FeaturePython)
  n = 1
  ref = N_element
FEATURE [App::DocumentObjectGroupPython] O_element604  label="O_element : 383"  # scripted group (container) (typed FeaturePython)
  n = 1
  ref = O_element
FEATURE [App::DocumentObjectGroupPython] G4_POLYVINYL_PYRROLIDONE  # scripted group (container) (typed FeaturePython)
  Dunit = g/cm3
  Dvalue = 1.25
  Group = -> [C_element687,H_element639,N_element309,O_element604]
  conduct = 2
  density = 1
  expand = 3
  formula = G4_POLYVINYL_PYRROLIDONE
  name = G4_POLYVINYL_PYRROLIDONE
  specific = 4
FEATURE [App::DocumentObjectGroupPython] K_element060  label="K_element : 011"  # scripted group (container) (typed FeaturePython)
  n = 1
  ref = K_element
FEATURE [App::DocumentObjectGroupPython] I_element046  label="I_element : 029"  # scripted group (container) (typed FeaturePython)
  n = 1
  ref = I_element
FEATURE [App::DocumentObjectGroupPython] G4_POTASSIUM_IODIDE  # scripted group (container) (typed FeaturePython)
  Dunit = g/cm3
  Dvalue = 3.13
  Group = -> [K_element060,I_element046]
  conduct = 2
  density = 1
  expand = 3
  formula = G4_POTASSIUM_IODIDE
  name = G4_POTASSIUM_IODIDE
  specific = 4
FEATURE [App::DocumentObjectGroupPython] K_element061  label="K_element : 012"  # scripted group (container) (typed FeaturePython)
  n = 2
  ref = K_element
FEATURE [App::DocumentObjectGroupPython] O_element605  label="O_element : 384"  # scripted group (container) (typed FeaturePython)
  n = 1
  ref = O_element
FEATURE [App::DocumentObjectGroupPython] G4_POTASSIUM_OXIDE  # scripted group (container) (typed FeaturePython)
  Dunit = g/cm3
  Dvalue = 2.32
  Group = -> [K_element061,O_element605]
  conduct = 2
  density = 1
  expand = 3
  formula = G4_POTASSIUM_OXIDE
  name = G4_POTASSIUM_OXIDE
  specific = 4
FEATURE [App::DocumentObjectGroupPython] C_element688  label="C_element : 452"  # scripted group (container) (typed FeaturePython)
  n = 3
  ref = C_element
FEATURE [App::DocumentObjectGroupPython] H_element640  label="H_element : 415"  # scripted group (container) (typed FeaturePython)
  n = 8
  ref = H_element
FEATURE [App::DocumentObjectGroupPython] G4_PROPANE  # scripted group (container) (typed FeaturePython)
  Dunit = g/cm3
  Dvalue = 0.00187939
  Group = -> [C_element688,H_element640]
  conduct = 2
  density = 1
  expand = 3
  formula = G4_PROPANE
  name = G4_PROPANE
  specific = 4
FEATURE [App::DocumentObjectGroupPython] C_element689  label="C_element : 453"  # scripted group (container) (typed FeaturePython)
  n = 3
  ref = C_element
FEATURE [App::DocumentObjectGroupPython] H_element641  label="H_element : 416"  # scripted group (container) (typed FeaturePython)
  n = 8
  ref = H_element
FEATURE [App::DocumentObjectGroupPython] G4_lPROPANE  # scripted group (container) (typed FeaturePython)
  Dunit = g/cm3
  Dvalue = 0.43
  Group = -> [C_element689,H_element641]
  conduct = 2
  density = 1
  expand = 3
  formula = G4_lPROPANE
  name = G4_lPROPANE
  specific = 4
FEATURE [App::DocumentObjectGroupPython] C_element690  label="C_element : 454"  # scripted group (container) (typed FeaturePython)
  n = 3
  ref = C_element
FEATURE [App::DocumentObjectGroupPython] H_element642  label="H_element : 417"  # scripted group (container) (typed FeaturePython)
  n = 8
  ref = H_element
FEATURE [App::DocumentObjectGroupPython] O_element606  label="O_element : 385"  # scripted group (container) (typed FeaturePython)
  n = 1
  ref = O_element
FEATURE [App::DocumentObjectGroupPython] G4_N_PROPYL_ALCOHOL  label="G4_N-PROPYL_ALCOHOL"  # scripted group (container) (typed FeaturePython)
  Dunit = g/cm3
  Dvalue = 0.8035
  Group = -> [C_element690,H_element642,O_element606]
  conduct = 2
  density = 1
  expand = 3
  formula = G4_N-PROPYL_ALCOHOL
  name = G4_N-PROPYL_ALCOHOL
  specific = 4
FEATURE [App::DocumentObjectGroupPython] C_element691  label="C_element : 455"  # scripted group (container) (typed FeaturePython)
  n = 5
  ref = C_element
FEATURE [App::DocumentObjectGroupPython] H_element643  label="H_element : 418"  # scripted group (container) (typed FeaturePython)
  n = 5
  ref = H_element
FEATURE [App::DocumentObjectGroupPython] N_element310  label="N_element : 168"  # scripted group (container) (typed FeaturePython)
  n = 1
  ref = N_element
FEATURE [App::DocumentObjectGroupPython] G4_PYRIDINE  # scripted group (container) (typed FeaturePython)
  Dunit = g/cm3
  Dvalue = 0.9819
  Group = -> [C_element691,H_element643,N_element310]
  conduct = 2
  density = 1
  expand = 3
  formula = G4_PYRIDINE
  name = G4_PYRIDINE
  specific = 4
FEATURE [App::DocumentObjectGroupPython] H_element644  label="H_element : 0.276"  # scripted group (container) (typed FeaturePython)
  n = 0.143711
FEATURE [App::DocumentObjectGroupPython] C_element692  label="C_element : 0.1007"  # scripted group (container) (typed FeaturePython)
  n = 0.856289
FEATURE [App::DocumentObjectGroupPython] G4_RUBBER_BUTYL  # scripted group (container) (typed FeaturePython)
  Dunit = g/cm3
  Dvalue = 0.92
  Group = -> [H_element644,C_element692]
  conduct = 2
  density = 1
  expand = 3
  formula = G4_RUBBER_BUTYL
  name = G4_RUBBER_BUTYL
  specific = 4
FEATURE [App::DocumentObjectGroupPython] H_element645  label="H_element : 0.277"  # scripted group (container) (typed FeaturePython)
  n = 0.118371
FEATURE [App::DocumentObjectGroupPython] C_element693  label="C_element : 0.1008"  # scripted group (container) (typed FeaturePython)
  n = 0.881629
FEATURE [App::DocumentObjectGroupPython] G4_RUBBER_NATURAL  # scripted group (container) (typed FeaturePython)
  Dunit = g/cm3
  Dvalue = 0.92
  Group = -> [H_element645,C_element693]
  conduct = 2
  density = 1
  expand = 3
  formula = G4_RUBBER_NATURAL
  name = G4_RUBBER_NATURAL
  specific = 4
FEATURE [App::DocumentObjectGroupPython] H_element646  label="H_element : 0.278"  # scripted group (container) (typed FeaturePython)
  n = 0.05692
FEATURE [App::DocumentObjectGroupPython] C_element694  label="C_element : 0.1009"  # scripted group (container) (typed FeaturePython)
  n = 0.542646
FEATURE [App::DocumentObjectGroupPython] Cl_element141  label="Cl_element : 0.637"  # scripted group (container) (typed FeaturePython)
  n = 0.400434
FEATURE [App::DocumentObjectGroupPython] G4_RUBBER_NEOPRENE  # scripted group (container) (typed FeaturePython)
  Dunit = g/cm3
  Dvalue = 1.23
  Group = -> [H_element646,C_element694,Cl_element141]
  conduct = 2
  density = 1
  expand = 3
  formula = G4_RUBBER_NEOPRENE
  name = G4_RUBBER_NEOPRENE
  specific = 4
FEATURE [App::DocumentObjectGroupPython] Si_element034  label="Si_element : 008"  # scripted group (container) (typed FeaturePython)
  n = 1
  ref = Si_element
FEATURE [App::DocumentObjectGroupPython] O_element607  label="O_element : 386"  # scripted group (container) (typed FeaturePython)
  n = 2
  ref = O_element
FEATURE [App::DocumentObjectGroupPython] G4_SILICON_DIOXIDE  # scripted group (container) (typed FeaturePython)
  Dunit = g/cm3
  Dvalue = 2.32
  Group = -> [Si_element034,O_element607]
  conduct = 2
  density = 1
  expand = 3
  formula = G4_SILICON_DIOXIDE
  name = G4_SILICON_DIOXIDE
  specific = 4
FEATURE [App::DocumentObjectGroupPython] Ag_element026  label="Ag_element : 016"  # scripted group (container) (typed FeaturePython)
  n = 1
  ref = Ag_element
FEATURE [App::DocumentObjectGroupPython] Br_element033  label="Br_element : 018"  # scripted group (container) (typed FeaturePython)
  n = 1
  ref = Br_element
FEATURE [App::DocumentObjectGroupPython] G4_SILVER_BROMIDE  # scripted group (container) (typed FeaturePython)
  Dunit = g/cm3
  Dvalue = 6.473
  Group = -> [Ag_element026,Br_element033]
  conduct = 2
  density = 1
  expand = 3
  formula = G4_SILVER_BROMIDE
  name = G4_SILVER_BROMIDE
  specific = 4
FEATURE [App::DocumentObjectGroupPython] Ag_element027  label="Ag_element : 017"  # scripted group (container) (typed FeaturePython)
  n = 1
  ref = Ag_element
FEATURE [App::DocumentObjectGroupPython] Cl_element142  label="Cl_element : 071"  # scripted group (container) (typed FeaturePython)
  n = 1
  ref = Cl_element
FEATURE [App::DocumentObjectGroupPython] G4_SILVER_CHLORIDE  # scripted group (container) (typed FeaturePython)
  Dunit = g/cm3
  Dvalue = 5.56
  Group = -> [Ag_element027,Cl_element142]
  conduct = 2
  density = 1
  expand = 3
  formula = G4_SILVER_CHLORIDE
  name = G4_SILVER_CHLORIDE
  specific = 4
FEATURE [App::DocumentObjectGroupPython] Br_element034  label="Br_element : 0.771"  # scripted group (container) (typed FeaturePython)
  n = 0.422895
FEATURE [App::DocumentObjectGroupPython] Ag_element028  label="Ag_element : 0.580"  # scripted group (container) (typed FeaturePython)
  n = 0.573748
FEATURE [App::DocumentObjectGroupPython] I_element047  label="I_element : 0.659"  # scripted group (container) (typed FeaturePython)
  n = 0.003357
FEATURE [App::DocumentObjectGroupPython] G4_SILVER_HALIDES  # scripted group (container) (typed FeaturePython)
  Dunit = g/cm3
  Dvalue = 6.47
  Group = -> [Br_element034,Ag_element028,I_element047]
  conduct = 2
  density = 1
  expand = 3
  formula = G4_SILVER_HALIDES
  name = G4_SILVER_HALIDES
  specific = 4
FEATURE [App::DocumentObjectGroupPython] Ag_element029  label="Ag_element : 018"  # scripted group (container) (typed FeaturePython)
  n = 1
  ref = Ag_element
FEATURE [App::DocumentObjectGroupPython] I_element048  label="I_element : 030"  # scripted group (container) (typed FeaturePython)
  n = 1
  ref = I_element
FEATURE [App::DocumentObjectGroupPython] G4_SILVER_IODIDE  # scripted group (container) (typed FeaturePython)
  Dunit = g/cm3
  Dvalue = 6.01
  Group = -> [Ag_element029,I_element048]
  conduct = 2
  density = 1
  expand = 3
  formula = G4_SILVER_IODIDE
  name = G4_SILVER_IODIDE
  specific = 4
FEATURE [App::DocumentObjectGroupPython] H_element647  label="H_element : 0.279"  # scripted group (container) (typed FeaturePython)
  n = 0.1
FEATURE [App::DocumentObjectGroupPython] C_element695  label="C_element : 0.1010"  # scripted group (container) (typed FeaturePython)
  n = 0.204
FEATURE [App::DocumentObjectGroupPython] N_element311  label="N_element : 0.851"  # scripted group (container) (typed FeaturePython)
  n = 0.042
FEATURE [App::DocumentObjectGroupPython] O_element608  label="O_element : 0.1001"  # scripted group (container) (typed FeaturePython)
  n = 0.645
FEATURE [App::DocumentObjectGroupPython] Na_element093  label="Na_element : 0.154"  # scripted group (container) (typed FeaturePython)
  n = 0.002
FEATURE [App::DocumentObjectGroupPython] P_element085  label="P_element : 0.146"  # scripted group (container) (typed FeaturePython)
  n = 0.001
FEATURE [App::DocumentObjectGroupPython] S_element112  label="S_element : 0.078"  # scripted group (container) (typed FeaturePython)
  n = 0.002
FEATURE [App::DocumentObjectGroupPython] Cl_element143  label="Cl_element : 0.638"  # scripted group (container) (typed FeaturePython)
  n = 0.003
FEATURE [App::DocumentObjectGroupPython] K_element062  label="K_element : 0.051"  # scripted group (container) (typed FeaturePython)
  n = 0.001
FEATURE [App::DocumentObjectGroupPython] G4_SKIN_ICRP  # scripted group (container) (typed FeaturePython)
  Dunit = g/cm3
  Dvalue = 1.09
  Group = -> [H_element647,C_element695,N_element311,O_element608,Na_element093,P_element085,S_element112,Cl_element143,K_element062]
  conduct = 2
  density = 1
  expand = 3
  formula = G4_SKIN_ICRP
  name = G4_SKIN_ICRP
  specific = 4
FEATURE [App::DocumentObjectGroupPython] Na_element094  label="Na_element : 019"  # scripted group (container) (typed FeaturePython)
  n = 2
  ref = Na_element
FEATURE [App::DocumentObjectGroupPython] C_element696  label="C_element : 456"  # scripted group (container) (typed FeaturePython)
  n = 1
  ref = C_element
FEATURE [App::DocumentObjectGroupPython] O_element609  label="O_element : 387"  # scripted group (container) (typed FeaturePython)
  n = 3
  ref = O_element
FEATURE [App::DocumentObjectGroupPython] G4_SODIUM_CARBONATE  # scripted group (container) (typed FeaturePython)
  Dunit = g/cm3
  Dvalue = 2.532
  Group = -> [Na_element094,C_element696,O_element609]
  conduct = 2
  density = 1
  expand = 3
  formula = G4_SODIUM_CARBONATE
  name = G4_SODIUM_CARBONATE
  specific = 4
FEATURE [App::DocumentObjectGroupPython] Na_element095  label="Na_element : 020"  # scripted group (container) (typed FeaturePython)
  n = 1
  ref = Na_element
FEATURE [App::DocumentObjectGroupPython] I_element049  label="I_element : 031"  # scripted group (container) (typed FeaturePython)
  n = 1
  ref = I_element
FEATURE [App::DocumentObjectGroupPython] G4_SODIUM_IODIDE  # scripted group (container) (typed FeaturePython)
  Dunit = g/cm3
  Dvalue = 3.667
  Group = -> [Na_element095,I_element049]
  conduct = 2
  density = 1
  expand = 3
  formula = G4_SODIUM_IODIDE
  name = G4_SODIUM_IODIDE
  specific = 4
FEATURE [App::DocumentObjectGroupPython] Na_element096  label="Na_element : 021"  # scripted group (container) (typed FeaturePython)
  n = 2
  ref = Na_element
FEATURE [App::DocumentObjectGroupPython] O_element610  label="O_element : 388"  # scripted group (container) (typed FeaturePython)
  n = 1
  ref = O_element
FEATURE [App::DocumentObjectGroupPython] G4_SODIUM_MONOXIDE  # scripted group (container) (typed FeaturePython)
  Dunit = g/cm3
  Dvalue = 2.27
  Group = -> [Na_element096,O_element610]
  conduct = 2
  density = 1
  expand = 3
  formula = G4_SODIUM_MONOXIDE
  name = G4_SODIUM_MONOXIDE
  specific = 4
FEATURE [App::DocumentObjectGroupPython] Na_element097  label="Na_element : 022"  # scripted group (container) (typed FeaturePython)
  n = 1
  ref = Na_element
FEATURE [App::DocumentObjectGroupPython] N_element312  label="N_element : 169"  # scripted group (container) (typed FeaturePython)
  n = 1
  ref = N_element
FEATURE [App::DocumentObjectGroupPython] O_element611  label="O_element : 389"  # scripted group (container) (typed FeaturePython)
  n = 3
  ref = O_element
FEATURE [App::DocumentObjectGroupPython] G4_SODIUM_NITRATE  # scripted group (container) (typed FeaturePython)
  Dunit = g/cm3
  Dvalue = 2.261
  Group = -> [Na_element097,N_element312,O_element611]
  conduct = 2
  density = 1
  expand = 3
  formula = G4_SODIUM_NITRATE
  name = G4_SODIUM_NITRATE
  specific = 4
FEATURE [App::DocumentObjectGroupPython] C_element697  label="C_element : 457"  # scripted group (container) (typed FeaturePython)
  n = 14
  ref = C_element
FEATURE [App::DocumentObjectGroupPython] H_element648  label="H_element : 419"  # scripted group (container) (typed FeaturePython)
  n = 12
  ref = H_element
FEATURE [App::DocumentObjectGroupPython] G4_STILBENE  # scripted group (container) (typed FeaturePython)
  Dunit = g/cm3
  Dvalue = 0.9707
  Group = -> [C_element697,H_element648]
  conduct = 2
  density = 1
  expand = 3
  formula = G4_STILBENE
  name = G4_STILBENE
  specific = 4
FEATURE [App::DocumentObjectGroupPython] C_element698  label="C_element : 458"  # scripted group (container) (typed FeaturePython)
  n = 12
  ref = C_element
FEATURE [App::DocumentObjectGroupPython] H_element649  label="H_element : 420"  # scripted group (container) (typed FeaturePython)
  n = 22
  ref = H_element
FEATURE [App::DocumentObjectGroupPython] O_element612  label="O_element : 390"  # scripted group (container) (typed FeaturePython)
  n = 11
  ref = O_element
FEATURE [App::DocumentObjectGroupPython] G4_SUCROSE  # scripted group (container) (typed FeaturePython)
  Dunit = g/cm3
  Dvalue = 1.5805
  Group = -> [C_element698,H_element649,O_element612]
  conduct = 2
  density = 1
  expand = 3
  formula = G4_SUCROSE
  name = G4_SUCROSE
  specific = 4
FEATURE [App::DocumentObjectGroupPython] C_element699  label="C_element : 459"  # scripted group (container) (typed FeaturePython)
  n = 18
  ref = C_element
FEATURE [App::DocumentObjectGroupPython] H_element650  label="H_element : 421"  # scripted group (container) (typed FeaturePython)
  n = 14
  ref = H_element
FEATURE [App::DocumentObjectGroupPython] G4_TERPHENYL  # scripted group (container) (typed FeaturePython)
  Dunit = g/cm3
  Dvalue = 1.24
  Group = -> [C_element699,H_element650]
  conduct = 2
  density = 1
  expand = 3
  formula = G4_TERPHENYL
  name = G4_TERPHENYL
  specific = 4
FEATURE [App::DocumentObjectGroupPython] H_element651  label="H_element : 0.280"  # scripted group (container) (typed FeaturePython)
  n = 0.106
FEATURE [App::DocumentObjectGroupPython] C_element700  label="C_element : 0.1011"  # scripted group (container) (typed FeaturePython)
  n = 0.099
FEATURE [App::DocumentObjectGroupPython] N_element313  label="N_element : 0.852"  # scripted group (container) (typed FeaturePython)
  n = 0.02
FEATURE [App::DocumentObjectGroupPython] O_element613  label="O_element : 0.1002"  # scripted group (container) (typed FeaturePython)
  n = 0.766
FEATURE [App::DocumentObjectGroupPython] Na_element098  label="Na_element : 0.155"  # scripted group (container) (typed FeaturePython)
  n = 0.002
FEATURE [App::DocumentObjectGroupPython] P_element086  label="P_element : 0.147"  # scripted group (container) (typed FeaturePython)
  n = 0.001
FEATURE [App::DocumentObjectGroupPython] S_element113  label="S_element : 0.079"  # scripted group (container) (typed FeaturePython)
  n = 0.002
FEATURE [App::DocumentObjectGroupPython] Cl_element144  label="Cl_element : 0.639"  # scripted group (container) (typed FeaturePython)
  n = 0.002
FEATURE [App::DocumentObjectGroupPython] K_element063  label="K_element : 0.052"  # scripted group (container) (typed FeaturePython)
  n = 0.002
FEATURE [App::DocumentObjectGroupPython] G4_TESTIS_ICRP  # scripted group (container) (typed FeaturePython)
  Dunit = g/cm3
  Dvalue = 1.04
  Group = -> [H_element651,C_element700,N_element313,O_element613,Na_element098,P_element086,S_element113,Cl_element144,K_element063]
  conduct = 2
  density = 1
  expand = 3
  formula = G4_TESTIS_ICRP
  name = G4_TESTIS_ICRP
  specific = 4
FEATURE [App::DocumentObjectGroupPython] C_element701  label="C_element : 460"  # scripted group (container) (typed FeaturePython)
  n = 2
  ref = C_element
FEATURE [App::DocumentObjectGroupPython] Cl_element145  label="Cl_element : 072"  # scripted group (container) (typed FeaturePython)
  n = 4
  ref = Cl_element
FEATURE [App::DocumentObjectGroupPython] G4_TETRACHLOROETHYLENE  # scripted group (container) (typed FeaturePython)
  Dunit = g/cm3
  Dvalue = 1.625
  Group = -> [C_element701,Cl_element145]
  conduct = 2
  density = 1
  expand = 3
  formula = G4_TETRACHLOROETHYLENE
  name = G4_TETRACHLOROETHYLENE
  specific = 4
FEATURE [App::DocumentObjectGroupPython] Tl_element009  label="Tl_element : 008"  # scripted group (container) (typed FeaturePython)
  n = 1
  ref = Tl_element
FEATURE [App::DocumentObjectGroupPython] Cl_element146  label="Cl_element : 073"  # scripted group (container) (typed FeaturePython)
  n = 1
  ref = Cl_element
FEATURE [App::DocumentObjectGroupPython] G4_THALLIUM_CHLORIDE  # scripted group (container) (typed FeaturePython)
  Dunit = g/cm3
  Dvalue = 7.004
  Group = -> [Tl_element009,Cl_element146]
  conduct = 2
  density = 1
  expand = 3
  formula = G4_THALLIUM_CHLORIDE
  name = G4_THALLIUM_CHLORIDE
  specific = 4
FEATURE [App::DocumentObjectGroupPython] H_element652  label="H_element : 0.281"  # scripted group (container) (typed FeaturePython)
  n = 0.105
FEATURE [App::DocumentObjectGroupPython] C_element702  label="C_element : 0.1012"  # scripted group (container) (typed FeaturePython)
  n = 0.256
FEATURE [App::DocumentObjectGroupPython] N_element314  label="N_element : 0.853"  # scripted group (container) (typed FeaturePython)
  n = 0.027
FEATURE [App::DocumentObjectGroupPython] O_element614  label="O_element : 0.1003"  # scripted group (container) (typed FeaturePython)
  n = 0.602
FEATURE [App::DocumentObjectGroupPython] Na_element099  label="Na_element : 0.156"  # scripted group (container) (typed FeaturePython)
  n = 0.001
FEATURE [App::DocumentObjectGroupPython] P_element087  label="P_element : 0.148"  # scripted group (container) (typed FeaturePython)
  n = 0.002
FEATURE [App::DocumentObjectGroupPython] S_element114  label="S_element : 0.080"  # scripted group (container) (typed FeaturePython)
  n = 0.003
FEATURE [App::DocumentObjectGroupPython] Cl_element147  label="Cl_element : 0.640"  # scripted group (container) (typed FeaturePython)
  n = 0.002
FEATURE [App::DocumentObjectGroupPython] K_element064  label="K_element : 0.053"  # scripted group (container) (typed FeaturePython)
  n = 0.002
FEATURE [App::DocumentObjectGroupPython] G4_TISSUE_SOFT_ICRP  # scripted group (container) (typed FeaturePython)
  Dunit = g/cm3
  Dvalue = 1.03
  Group = -> [H_element652,C_element702,N_element314,O_element614,Na_element099,P_element087,S_element114,Cl_element147,K_element064]
  conduct = 2
  density = 1
  expand = 3
  formula = G4_TISSUE_SOFT_ICRP
  name = G4_TISSUE_SOFT_ICRP
  specific = 4
FEATURE [App::DocumentObjectGroupPython] H_element653  label="H_element : 0.282"  # scripted group (container) (typed FeaturePython)
  n = 0.101
FEATURE [App::DocumentObjectGroupPython] C_element703  label="C_element : 0.1013"  # scripted group (container) (typed FeaturePython)
  n = 0.111
FEATURE [App::DocumentObjectGroupPython] N_element315  label="N_element : 0.854"  # scripted group (container) (typed FeaturePython)
  n = 0.026
FEATURE [App::DocumentObjectGroupPython] O_element615  label="O_element : 0.1004"  # scripted group (container) (typed FeaturePython)
  n = 0.762
FEATURE [App::DocumentObjectGroupPython] G4_TISSUE_SOFT_ICRU_4  label="G4_TISSUE_SOFT_ICRU-4"  # scripted group (container) (typed FeaturePython)
  Dunit = g/cm3
  Dvalue = 1
  Group = -> [H_element653,C_element703,N_element315,O_element615]
  conduct = 2
  density = 1
  expand = 3
  formula = G4_TISSUE_SOFT_ICRU-4
  name = G4_TISSUE_SOFT_ICRU-4
  specific = 4
FEATURE [App::DocumentObjectGroupPython] H_element654  label="H_element : 0.283"  # scripted group (container) (typed FeaturePython)
  n = 0.101869
FEATURE [App::DocumentObjectGroupPython] C_element704  label="C_element : 0.1014"  # scripted group (container) (typed FeaturePython)
  n = 0.456179
FEATURE [App::DocumentObjectGroupPython] N_element316  label="N_element : 0.855"  # scripted group (container) (typed FeaturePython)
  n = 0.035172
FEATURE [App::DocumentObjectGroupPython] O_element616  label="O_element : 0.1005"  # scripted group (container) (typed FeaturePython)
  n = 0.40678
FEATURE [App::DocumentObjectGroupPython] G4_TISSUE_METHANE  label="G4_TISSUE-METHANE"  # scripted group (container) (typed FeaturePython)
  Dunit = g/cm3
  Dvalue = 0.00106409
  Group = -> [H_element654,C_element704,N_element316,O_element616]
  conduct = 2
  density = 1
  expand = 3
  formula = G4_TISSUE-METHANE
  name = G4_TISSUE-METHANE
  specific = 4
FEATURE [App::DocumentObjectGroupPython] H_element655  label="H_element : 0.284"  # scripted group (container) (typed FeaturePython)
  n = 0.102672
FEATURE [App::DocumentObjectGroupPython] C_element705  label="C_element : 0.1015"  # scripted group (container) (typed FeaturePython)
  n = 0.56894
FEATURE [App::DocumentObjectGroupPython] N_element317  label="N_element : 0.856"  # scripted group (container) (typed FeaturePython)
  n = 0.035022
FEATURE [App::DocumentObjectGroupPython] O_element617  label="O_element : 0.1006"  # scripted group (container) (typed FeaturePython)
  n = 0.293366
FEATURE [App::DocumentObjectGroupPython] G4_TISSUE_PROPANE  label="G4_TISSUE-PROPANE"  # scripted group (container) (typed FeaturePython)
  Dunit = g/cm3
  Dvalue = 0.00182628
  Group = -> [H_element655,C_element705,N_element317,O_element617]
  conduct = 2
  density = 1
  expand = 3
  formula = G4_TISSUE-PROPANE
  name = G4_TISSUE-PROPANE
  specific = 4
FEATURE [App::DocumentObjectGroupPython] Ti_element019  label="Ti_element : 008"  # scripted group (container) (typed FeaturePython)
  n = 1
  ref = Ti_element
FEATURE [App::DocumentObjectGroupPython] O_element618  label="O_element : 391"  # scripted group (container) (typed FeaturePython)
  n = 2
  ref = O_element
FEATURE [App::DocumentObjectGroupPython] G4_TITANIUM_DIOXIDE  # scripted group (container) (typed FeaturePython)
  Dunit = g/cm3
  Dvalue = 4.26
  Group = -> [Ti_element019,O_element618]
  conduct = 2
  density = 1
  expand = 3
  formula = G4_TITANIUM_DIOXIDE
  name = G4_TITANIUM_DIOXIDE
  specific = 4
FEATURE [App::DocumentObjectGroupPython] C_element706  label="C_element : 461"  # scripted group (container) (typed FeaturePython)
  n = 7
  ref = C_element
FEATURE [App::DocumentObjectGroupPython] H_element656  label="H_element : 422"  # scripted group (container) (typed FeaturePython)
  n = 8
  ref = H_element
FEATURE [App::DocumentObjectGroupPython] G4_TOLUENE  # scripted group (container) (typed FeaturePython)
  Dunit = g/cm3
  Dvalue = 0.8669
  Group = -> [C_element706,H_element656]
  conduct = 2
  density = 1
  expand = 3
  formula = G4_TOLUENE
  name = G4_TOLUENE
  specific = 4
FEATURE [App::DocumentObjectGroupPython] C_element707  label="C_element : 462"  # scripted group (container) (typed FeaturePython)
  n = 2
  ref = C_element
FEATURE [App::DocumentObjectGroupPython] H_element657  label="H_element : 423"  # scripted group (container) (typed FeaturePython)
  n = 1
  ref = H_element
FEATURE [App::DocumentObjectGroupPython] Cl_element148  label="Cl_element : 074"  # scripted group (container) (typed FeaturePython)
  n = 3
  ref = Cl_element
FEATURE [App::DocumentObjectGroupPython] G4_TRICHLOROETHYLENE  # scripted group (container) (typed FeaturePython)
  Dunit = g/cm3
  Dvalue = 1.46
  Group = -> [C_element707,H_element657,Cl_element148]
  conduct = 2
  density = 1
  expand = 3
  formula = G4_TRICHLOROETHYLENE
  name = G4_TRICHLOROETHYLENE
  specific = 4
FEATURE [App::DocumentObjectGroupPython] C_element708  label="C_element : 463"  # scripted group (container) (typed FeaturePython)
  n = 6
  ref = C_element
FEATURE [App::DocumentObjectGroupPython] H_element658  label="H_element : 424"  # scripted group (container) (typed FeaturePython)
  n = 15
  ref = H_element
FEATURE [App::DocumentObjectGroupPython] O_element619  label="O_element : 392"  # scripted group (container) (typed FeaturePython)
  n = 4
  ref = O_element
FEATURE [App::DocumentObjectGroupPython] P_element088  label="P_element : 032"  # scripted group (container) (typed FeaturePython)
  n = 1
  ref = P_element
FEATURE [App::DocumentObjectGroupPython] G4_TRIETHYL_PHOSPHATE  # scripted group (container) (typed FeaturePython)
  Dunit = g/cm3
  Dvalue = 1.07
  Group = -> [C_element708,H_element658,O_element619,P_element088]
  conduct = 2
  density = 1
  expand = 3
  formula = G4_TRIETHYL_PHOSPHATE
  name = G4_TRIETHYL_PHOSPHATE
  specific = 4
FEATURE [App::DocumentObjectGroupPython] W_element023  label="W_element : 022"  # scripted group (container) (typed FeaturePython)
  n = 1
  ref = W_element
FEATURE [App::DocumentObjectGroupPython] F_element093  label="F_element : 046"  # scripted group (container) (typed FeaturePython)
  n = 6
  ref = F_element
FEATURE [App::DocumentObjectGroupPython] G4_TUNGSTEN_HEXAFLUORIDE  # scripted group (container) (typed FeaturePython)
  Dunit = g/cm3
  Dvalue = 2.4
  Group = -> [W_element023,F_element093]
  conduct = 2
  density = 1
  expand = 3
  formula = G4_TUNGSTEN_HEXAFLUORIDE
  name = G4_TUNGSTEN_HEXAFLUORIDE
  specific = 4
FEATURE [App::DocumentObjectGroupPython] U_element017  label="U_element : 016"  # scripted group (container) (typed FeaturePython)
  n = 1
  ref = U_element
FEATURE [App::DocumentObjectGroupPython] C_element709  label="C_element : 464"  # scripted group (container) (typed FeaturePython)
  n = 2
  ref = C_element
FEATURE [App::DocumentObjectGroupPython] G4_URANIUM_DICARBIDE  # scripted group (container) (typed FeaturePython)
  Dunit = g/cm3
  Dvalue = 11.28
  Group = -> [U_element017,C_element709]
  conduct = 2
  density = 1
  expand = 3
  formula = G4_URANIUM_DICARBIDE
  name = G4_URANIUM_DICARBIDE
  specific = 4
FEATURE [App::DocumentObjectGroupPython] U_element018  label="U_element : 017"  # scripted group (container) (typed FeaturePython)
  n = 1
  ref = U_element
FEATURE [App::DocumentObjectGroupPython] C_element710  label="C_element : 465"  # scripted group (container) (typed FeaturePython)
  n = 1
  ref = C_element
FEATURE [App::DocumentObjectGroupPython] G4_URANIUM_MONOCARBIDE  # scripted group (container) (typed FeaturePython)
  Dunit = g/cm3
  Dvalue = 13.63
  Group = -> [U_element018,C_element710]
  conduct = 2
  density = 1
  expand = 3
  formula = G4_URANIUM_MONOCARBIDE
  name = G4_URANIUM_MONOCARBIDE
  specific = 4
FEATURE [App::DocumentObjectGroupPython] U_element019  label="U_element : 018"  # scripted group (container) (typed FeaturePython)
  n = 1
  ref = U_element
FEATURE [App::DocumentObjectGroupPython] O_element620  label="O_element : 393"  # scripted group (container) (typed FeaturePython)
  n = 2
  ref = O_element
FEATURE [App::DocumentObjectGroupPython] G4_URANIUM_OXIDE  # scripted group (container) (typed FeaturePython)
  Dunit = g/cm3
  Dvalue = 10.96
  Group = -> [U_element019,O_element620]
  conduct = 2
  density = 1
  expand = 3
  formula = G4_URANIUM_OXIDE
  name = G4_URANIUM_OXIDE
  specific = 4
FEATURE [App::DocumentObjectGroupPython] C_element711  label="C_element : 466"  # scripted group (container) (typed FeaturePython)
  n = 1
  ref = C_element
FEATURE [App::DocumentObjectGroupPython] H_element659  label="H_element : 425"  # scripted group (container) (typed FeaturePython)
  n = 4
  ref = H_element
FEATURE [App::DocumentObjectGroupPython] N_element318  label="N_element : 170"  # scripted group (container) (typed FeaturePython)
  n = 2
  ref = N_element
FEATURE [App::DocumentObjectGroupPython] O_element621  label="O_element : 394"  # scripted group (container) (typed FeaturePython)
  n = 1
  ref = O_element
FEATURE [App::DocumentObjectGroupPython] G4_UREA  # scripted group (container) (typed FeaturePython)
  Dunit = g/cm3
  Dvalue = 1.323
  Group = -> [C_element711,H_element659,N_element318,O_element621]
  conduct = 2
  density = 1
  expand = 3
  formula = G4_UREA
  name = G4_UREA
  specific = 4
FEATURE [App::DocumentObjectGroupPython] C_element712  label="C_element : 467"  # scripted group (container) (typed FeaturePython)
  n = 5
  ref = C_element
FEATURE [App::DocumentObjectGroupPython] H_element660  label="H_element : 426"  # scripted group (container) (typed FeaturePython)
  n = 11
  ref = H_element
FEATURE [App::DocumentObjectGroupPython] N_element319  label="N_element : 171"  # scripted group (container) (typed FeaturePython)
  n = 1
  ref = N_element
FEATURE [App::DocumentObjectGroupPython] O_element622  label="O_element : 395"  # scripted group (container) (typed FeaturePython)
  n = 2
  ref = O_element
FEATURE [App::DocumentObjectGroupPython] G4_VALINE  # scripted group (container) (typed FeaturePython)
  Dunit = g/cm3
  Dvalue = 1.23
  Group = -> [C_element712,H_element660,N_element319,O_element622]
  conduct = 2
  density = 1
  expand = 3
  formula = G4_VALINE
  name = G4_VALINE
  specific = 4
FEATURE [App::DocumentObjectGroupPython] H_element661  label="H_element : 0.285"  # scripted group (container) (typed FeaturePython)
  n = 0.009417
FEATURE [App::DocumentObjectGroupPython] C_element713  label="C_element : 0.1016"  # scripted group (container) (typed FeaturePython)
  n = 0.280555
FEATURE [App::DocumentObjectGroupPython] F_element094  label="F_element : 0.734"  # scripted group (container) (typed FeaturePython)
  n = 0.710028
FEATURE [App::DocumentObjectGroupPython] G4_VITON  # scripted group (container) (typed FeaturePython)
  Dunit = g/cm3
  Dvalue = 1.8
  Group = -> [H_element661,C_element713,F_element094]
  conduct = 2
  density = 1
  expand = 3
  formula = G4_VITON
  name = G4_VITON
  specific = 4
FEATURE [App::DocumentObjectGroupPython] H_element662  label="H_element : 427"  # scripted group (container) (typed FeaturePython)
  n = 2
  ref = H_element
FEATURE [App::DocumentObjectGroupPython] O_element623  label="O_element : 396"  # scripted group (container) (typed FeaturePython)
  n = 1
  ref = O_element
FEATURE [App::DocumentObjectGroupPython] G4_WATER  # scripted group (container) (typed FeaturePython)
  Dunit = g/cm3
  Dvalue = 1
  Group = -> [H_element662,O_element623]
  conduct = 2
  density = 1
  expand = 3
  formula = G4_WATER
  name = G4_WATER
  specific = 4
FEATURE [App::DocumentObjectGroupPython] H_element663  label="H_element : 428"  # scripted group (container) (typed FeaturePython)
  n = 2
  ref = H_element
FEATURE [App::DocumentObjectGroupPython] O_element624  label="O_element : 397"  # scripted group (container) (typed FeaturePython)
  n = 1
  ref = O_element
FEATURE [App::DocumentObjectGroupPython] G4_WATER_VAPOR  # scripted group (container) (typed FeaturePython)
  Dunit = g/cm3
  Dvalue = 0.000756182
  Group = -> [H_element663,O_element624]
  conduct = 2
  density = 1
  expand = 3
  formula = G4_WATER_VAPOR
  name = G4_WATER_VAPOR
  specific = 4
FEATURE [App::DocumentObjectGroupPython] C_element714  label="C_element : 468"  # scripted group (container) (typed FeaturePython)
  n = 8
  ref = C_element
FEATURE [App::DocumentObjectGroupPython] H_element664  label="H_element : 429"  # scripted group (container) (typed FeaturePython)
  n = 10
  ref = H_element
FEATURE [App::DocumentObjectGroupPython] G4_XYLENE  # scripted group (container) (typed FeaturePython)
  Dunit = g/cm3
  Dvalue = 0.87
  Group = -> [C_element714,H_element664]
  conduct = 2
  density = 1
  expand = 3
  formula = G4_XYLENE
  name = G4_XYLENE
  specific = 4
FEATURE [App::DocumentObjectGroupPython] C_element715  label="C_element : 469"  # scripted group (container) (typed FeaturePython)
  n = 1
  ref = C_element
FEATURE [App::DocumentObjectGroupPython] G4_GRAPHITE  # scripted group (container) (typed FeaturePython)
  Dunit = g/cm3
  Dvalue = 2.21
  Group = -> [C_element715]
  conduct = 2
  density = 1
  expand = 3
  formula = G4_GRAPHITE
  name = G4_GRAPHITE
  specific = 4
FEATURE [App::DocumentObjectGroupPython] NIST  # scripted group (container) (typed FeaturePython)
  Group = -> [G4_A_150_TISSUE,G4_ACETONE,G4_ACETYLENE,G4_ADENINE,G4_ADIPOSE_TISSUE_ICRP,G4_AIR,G4_ALANINE,G4_ALUMINUM_OXIDE,G4_AMBER,G4_AMMONIA,G4_ANILINE,G4_ANTHRACENE,G4_B_100_BONE,G4_BAKELITE,G4_BARIUM_FLUORIDE,G4_BARIUM_SULFATE,G4_BENZENE,G4_BERYLLIUM_OXIDE,G4_BGO,G4_BLOOD_ICRP,G4_BONE_COMPACT_ICRU,G4_BONE_CORTICAL_ICRP,G4_BORON_CARBIDE,G4_BORON_OXIDE,G4_BRAIN_ICRP,G4_BUTANE,G4_N_BUTYL_ALCOHOL,G4_C_552,+152 more]
FEATURE [App::DocumentObjectGroupPython] H_element665  label="H_element : 430"  # scripted group (container) (typed FeaturePython)
  n = 1
  ref = H_element
FEATURE [App::DocumentObjectGroupPython] G4_H  # scripted group (container) (typed FeaturePython)
  Dunit = g/cm3
  Dvalue = 8.3748e-05
  Group = -> [H_element665]
  conduct = 2
  density = 1
  expand = 3
  formula = H
  name = G4_H
  specific = 4
FEATURE [App::DocumentObjectGroupPython] He_element005  label="He_element : 004"  # scripted group (container) (typed FeaturePython)
  n = 1
  ref = He_element
FEATURE [App::DocumentObjectGroupPython] G4_He  # scripted group (container) (typed FeaturePython)
  Dunit = g/cm3
  Dvalue = 0.000166322
  Group = -> [He_element005]
  conduct = 2
  density = 1
  expand = 3
  formula = He
  name = G4_He
  specific = 4
FEATURE [App::DocumentObjectGroupPython] Li_element040  label="Li_element : 038"  # scripted group (container) (typed FeaturePython)
  n = 1
  ref = Li_element
FEATURE [App::DocumentObjectGroupPython] G4_Li  # scripted group (container) (typed FeaturePython)
  Dunit = g/cm3
  Dvalue = 0.534
  Group = -> [Li_element040]
  conduct = 2
  density = 1
  expand = 3
  formula = Li
  name = G4_Li
  specific = 4
FEATURE [App::DocumentObjectGroupPython] Be_element010  label="Be_element : 009"  # scripted group (container) (typed FeaturePython)
  n = 1
  ref = Be_element
FEATURE [App::DocumentObjectGroupPython] G4_Be  # scripted group (container) (typed FeaturePython)
  Dunit = g/cm3
  Dvalue = 1.848
  Group = -> [Be_element010]
  conduct = 2
  density = 1
  expand = 3
  formula = Be
  name = G4_Be
  specific = 4
FEATURE [App::DocumentObjectGroupPython] B_element035  label="B_element : 028"  # scripted group (container) (typed FeaturePython)
  n = 1
  ref = B_element
FEATURE [App::DocumentObjectGroupPython] G4_B  # scripted group (container) (typed FeaturePython)
  Dunit = g/cm3
  Dvalue = 2.37
  Group = -> [B_element035]
  conduct = 2
  density = 1
  expand = 3
  formula = B
  name = G4_B
  specific = 4
FEATURE [App::DocumentObjectGroupPython] C_element716  label="C_element : 470"  # scripted group (container) (typed FeaturePython)
  n = 1
  ref = C_element
FEATURE [App::DocumentObjectGroupPython] G4_C  # scripted group (container) (typed FeaturePython)
  Dunit = g/cm3
  Dvalue = 2
  Group = -> [C_element716]
  conduct = 2
  density = 1
  expand = 3
  formula = C
  name = G4_C
  specific = 4
FEATURE [App::DocumentObjectGroupPython] N_element320  label="N_element : 172"  # scripted group (container) (typed FeaturePython)
  n = 1
  ref = N_element
FEATURE [App::DocumentObjectGroupPython] G4_N  # scripted group (container) (typed FeaturePython)
  Dunit = g/cm3
  Dvalue = 0.0011652
  Group = -> [N_element320]
  conduct = 2
  density = 1
  expand = 3
  formula = N
  name = G4_N
  specific = 4
FEATURE [App::DocumentObjectGroupPython] O_element625  label="O_element : 398"  # scripted group (container) (typed FeaturePython)
  n = 1
  ref = O_element
FEATURE [App::DocumentObjectGroupPython] G4_O  # scripted group (container) (typed FeaturePython)
  Dunit = g/cm3
  Dvalue = 0.00133151
  Group = -> [O_element625]
  conduct = 2
  density = 1
  expand = 3
  formula = O
  name = G4_O
  specific = 4
FEATURE [App::DocumentObjectGroupPython] F_element095  label="F_element : 047"  # scripted group (container) (typed FeaturePython)
  n = 1
  ref = F_element
FEATURE [App::DocumentObjectGroupPython] G4_F  # scripted group (container) (typed FeaturePython)
  Dunit = g/cm3
  Dvalue = 0.00158029
  Group = -> [F_element095]
  conduct = 2
  density = 1
  expand = 3
  formula = F
  name = G4_F
  specific = 4
FEATURE [App::DocumentObjectGroupPython] Ne_element005  label="Ne_element : 004"  # scripted group (container) (typed FeaturePython)
  n = 1
  ref = Ne_element
FEATURE [App::DocumentObjectGroupPython] G4_Ne  # scripted group (container) (typed FeaturePython)
  Dunit = g/cm3
  Dvalue = 0.000838505
  Group = -> [Ne_element005]
  conduct = 2
  density = 1
  expand = 3
  formula = Ne
  name = G4_Ne
  specific = 4
FEATURE [App::DocumentObjectGroupPython] Na_element100  label="Na_element : 023"  # scripted group (container) (typed FeaturePython)
  n = 1
  ref = Na_element
FEATURE [App::DocumentObjectGroupPython] G4_Na  # scripted group (container) (typed FeaturePython)
  Dunit = g/cm3
  Dvalue = 0.971
  Group = -> [Na_element100]
  conduct = 2
  density = 1
  expand = 3
  formula = Na
  name = G4_Na
  specific = 4
FEATURE [App::DocumentObjectGroupPython] Mg_element055  label="Mg_element : 024"  # scripted group (container) (typed FeaturePython)
  n = 1
  ref = Mg_element
FEATURE [App::DocumentObjectGroupPython] G4_Mg  # scripted group (container) (typed FeaturePython)
  Dunit = g/cm3
  Dvalue = 1.74
  Group = -> [Mg_element055]
  conduct = 2
  density = 1
  expand = 3
  formula = Mg
  name = G4_Mg
  specific = 4
FEATURE [App::DocumentObjectGroupPython] Al_element020  label="Al_element : 008"  # scripted group (container) (typed FeaturePython)
  n = 1
  ref = Al_element
FEATURE [App::DocumentObjectGroupPython] G4_Al  # scripted group (container) (typed FeaturePython)
  Dunit = g/cm3
  Dvalue = 2.699
  Group = -> [Al_element020]
  conduct = 2
  density = 1
  expand = 3
  formula = Al
  name = G4_Al
  specific = 4
FEATURE [App::DocumentObjectGroupPython] Si_element035  label="Si_element : 009"  # scripted group (container) (typed FeaturePython)
  n = 1
  ref = Si_element
FEATURE [App::DocumentObjectGroupPython] G4_Si  # scripted group (container) (typed FeaturePython)
  Dunit = g/cm3
  Dvalue = 2.33
  Group = -> [Si_element035]
  conduct = 2
  density = 1
  expand = 3
  formula = Si
  name = G4_Si
  specific = 4
FEATURE [App::DocumentObjectGroupPython] P_element089  label="P_element : 033"  # scripted group (container) (typed FeaturePython)
  n = 1
  ref = P_element
FEATURE [App::DocumentObjectGroupPython] G4_P  # scripted group (container) (typed FeaturePython)
  Dunit = g/cm3
  Dvalue = 2.2
  Group = -> [P_element089]
  conduct = 2
  density = 1
  expand = 3
  formula = P
  name = G4_P
  specific = 4
FEATURE [App::DocumentObjectGroupPython] S_element115  label="S_element : 034"  # scripted group (container) (typed FeaturePython)
  n = 1
  ref = S_element
FEATURE [App::DocumentObjectGroupPython] G4_S  # scripted group (container) (typed FeaturePython)
  Dunit = g/cm3
  Dvalue = 2
  Group = -> [S_element115]
  conduct = 2
  density = 1
  expand = 3
  formula = S
  name = G4_S
  specific = 4
FEATURE [App::DocumentObjectGroupPython] Cl_element149  label="Cl_element : 075"  # scripted group (container) (typed FeaturePython)
  n = 1
  ref = Cl_element
FEATURE [App::DocumentObjectGroupPython] G4_Cl  # scripted group (container) (typed FeaturePython)
  Dunit = g/cm3
  Dvalue = 0.00299473
  Group = -> [Cl_element149]
  conduct = 2
  density = 1
  expand = 3
  formula = Cl
  name = G4_Cl
  specific = 4
FEATURE [App::DocumentObjectGroupPython] Ar_element010  label="Ar_element : 004"  # scripted group (container) (typed FeaturePython)
  n = 1
  ref = Ar_element
FEATURE [App::DocumentObjectGroupPython] G4_Ar  # scripted group (container) (typed FeaturePython)
  Dunit = g/cm3
  Dvalue = 0.00166201
  Group = -> [Ar_element010]
  conduct = 2
  density = 1
  expand = 3
  formula = Ar
  name = G4_Ar
  specific = 4
FEATURE [App::DocumentObjectGroupPython] K_element065  label="K_element : 013"  # scripted group (container) (typed FeaturePython)
  n = 1
  ref = K_element
FEATURE [App::DocumentObjectGroupPython] G4_K  # scripted group (container) (typed FeaturePython)
  Dunit = g/cm3
  Dvalue = 0.862
  Group = -> [K_element065]
  conduct = 2
  density = 1
  expand = 3
  formula = K
  name = G4_K
  specific = 4
FEATURE [App::DocumentObjectGroupPython] Ca_element070  label="Ca_element : 034"  # scripted group (container) (typed FeaturePython)
  n = 1
  ref = Ca_element
FEATURE [App::DocumentObjectGroupPython] G4_Ca  # scripted group (container) (typed FeaturePython)
  Dunit = g/cm3
  Dvalue = 1.55
  Group = -> [Ca_element070]
  conduct = 2
  density = 1
  expand = 3
  formula = Ca
  name = G4_Ca
  specific = 4
FEATURE [App::DocumentObjectGroupPython] Sc_element005  label="Sc_element : 004"  # scripted group (container) (typed FeaturePython)
  n = 1
  ref = Sc_element
FEATURE [App::DocumentObjectGroupPython] G4_Sc  # scripted group (container) (typed FeaturePython)
  Dunit = g/cm3
  Dvalue = 2.989
  Group = -> [Sc_element005]
  conduct = 2
  density = 1
  expand = 3
  formula = Sc
  name = G4_Sc
  specific = 4
FEATURE [App::DocumentObjectGroupPython] Ti_element020  label="Ti_element : 009"  # scripted group (container) (typed FeaturePython)
  n = 1
  ref = Ti_element
FEATURE [App::DocumentObjectGroupPython] G4_Ti  # scripted group (container) (typed FeaturePython)
  Dunit = g/cm3
  Dvalue = 4.54
  Group = -> [Ti_element020]
  conduct = 2
  density = 1
  expand = 3
  formula = Ti
  name = G4_Ti
  specific = 4
FEATURE [App::DocumentObjectGroupPython] V_element005  label="V_element : 004"  # scripted group (container) (typed FeaturePython)
  n = 1
  ref = V_element
FEATURE [App::DocumentObjectGroupPython] G4_V  # scripted group (container) (typed FeaturePython)
  Dunit = g/cm3
  Dvalue = 6.11
  Group = -> [V_element005]
  conduct = 2
  density = 1
  expand = 3
  formula = V
  name = G4_V
  specific = 4
FEATURE [App::DocumentObjectGroupPython] Cr_element009  label="Cr_element : 023"  # scripted group (container) (typed FeaturePython)
  n = 1
  ref = Cr_element
FEATURE [App::DocumentObjectGroupPython] G4_Cr  # scripted group (container) (typed FeaturePython)
  Dunit = g/cm3
  Dvalue = 7.18
  Group = -> [Cr_element009]
  conduct = 2
  density = 1
  expand = 3
  formula = Cr
  name = G4_Cr
  specific = 4
FEATURE [App::DocumentObjectGroupPython] Mn_element005  label="Mn_element : 004"  # scripted group (container) (typed FeaturePython)
  n = 1
  ref = Mn_element
FEATURE [App::DocumentObjectGroupPython] G4_Mn  # scripted group (container) (typed FeaturePython)
  Dunit = g/cm3
  Dvalue = 7.44
  Group = -> [Mn_element005]
  conduct = 2
  density = 1
  expand = 3
  formula = Mn
  name = G4_Mn
  specific = 4
FEATURE [App::DocumentObjectGroupPython] Fe_element039  label="Fe_element : 020"  # scripted group (container) (typed FeaturePython)
  n = 1
  ref = Fe_element
FEATURE [App::DocumentObjectGroupPython] G4_Fe  # scripted group (container) (typed FeaturePython)
  Dunit = g/cm3
  Dvalue = 7.874
  Group = -> [Fe_element039]
  conduct = 2
  density = 1
  expand = 3
  formula = Fe
  name = G4_Fe
  specific = 4
FEATURE [App::DocumentObjectGroupPython] Co_element005  label="Co_element : 004"  # scripted group (container) (typed FeaturePython)
  n = 1
  ref = Co_element
FEATURE [App::DocumentObjectGroupPython] G4_Co  # scripted group (container) (typed FeaturePython)
  Dunit = g/cm3
  Dvalue = 8.9
  Group = -> [Co_element005]
  conduct = 2
  density = 1
  expand = 3
  formula = Co
  name = G4_Co
  specific = 4
FEATURE [App::DocumentObjectGroupPython] Ni_element009  label="Ni_element : 013"  # scripted group (container) (typed FeaturePython)
  n = 1
  ref = Ni_element
FEATURE [App::DocumentObjectGroupPython] G4_Ni  # scripted group (container) (typed FeaturePython)
  Dunit = g/cm3
  Dvalue = 8.902
  Group = -> [Ni_element009]
  conduct = 2
  density = 1
  expand = 3
  formula = Ni
  name = G4_Ni
  specific = 4
FEATURE [App::DocumentObjectGroupPython] Cu_element013  label="Cu_element : 096"  # scripted group (container) (typed FeaturePython)
  n = 1
  ref = Cu_element
FEATURE [App::DocumentObjectGroupPython] G4_Cu  # scripted group (container) (typed FeaturePython)
  Dunit = g/cm3
  Dvalue = 8.96
  Group = -> [Cu_element013]
  conduct = 2
  density = 1
  expand = 3
  formula = Cu
  name = G4_Cu
  specific = 4
FEATURE [App::DocumentObjectGroupPython] Zn_element013  label="Zn_element : 042"  # scripted group (container) (typed FeaturePython)
  n = 1
  ref = Zn_element
FEATURE [App::DocumentObjectGroupPython] G4_Zn  # scripted group (container) (typed FeaturePython)
  Dunit = g/cm3
  Dvalue = 7.133
  Group = -> [Zn_element013]
  conduct = 2
  density = 1
  expand = 3
  formula = Zn
  name = G4_Zn
  specific = 4
FEATURE [App::DocumentObjectGroupPython] Ga_element010  label="Ga_element : 009"  # scripted group (container) (typed FeaturePython)
  n = 1
  ref = Ga_element
FEATURE [App::DocumentObjectGroupPython] G4_Ga  # scripted group (container) (typed FeaturePython)
  Dunit = g/cm3
  Dvalue = 5.904
  Group = -> [Ga_element010]
  conduct = 2
  density = 1
  expand = 3
  formula = Ga
  name = G4_Ga
  specific = 4
FEATURE [App::DocumentObjectGroupPython] Ge_element010  label="Ge_element : 009"  # scripted group (container) (typed FeaturePython)
  n = 1
  ref = Ge_element
FEATURE [App::DocumentObjectGroupPython] G4_Ge  # scripted group (container) (typed FeaturePython)
  Dunit = g/cm3
  Dvalue = 5.323
  Group = -> [Ge_element010]
  conduct = 2
  density = 1
  expand = 3
  formula = Ge
  name = G4_Ge
  specific = 4
FEATURE [App::DocumentObjectGroupPython] As_element015  label="As_element : 009"  # scripted group (container) (typed FeaturePython)
  n = 1
  ref = As_element
FEATURE [App::DocumentObjectGroupPython] G4_As  # scripted group (container) (typed FeaturePython)
  Dunit = g/cm3
  Dvalue = 5.73
  Group = -> [As_element015]
  conduct = 2
  density = 1
  expand = 3
  formula = As
  name = G4_As
  specific = 4
FEATURE [App::DocumentObjectGroupPython] Se_element005  label="Se_element : 004"  # scripted group (container) (typed FeaturePython)
  n = 1
  ref = Se_element
FEATURE [App::DocumentObjectGroupPython] G4_Se  # scripted group (container) (typed FeaturePython)
  Dunit = g/cm3
  Dvalue = 4.5
  Group = -> [Se_element005]
  conduct = 2
  density = 1
  expand = 3
  formula = Se
  name = G4_Se
  specific = 4
FEATURE [App::DocumentObjectGroupPython] Br_element035  label="Br_element : 019"  # scripted group (container) (typed FeaturePython)
  n = 1
  ref = Br_element
FEATURE [App::DocumentObjectGroupPython] G4_Br  # scripted group (container) (typed FeaturePython)
  Dunit = g/cm3
  Dvalue = 0.0070721
  Group = -> [Br_element035]
  conduct = 2
  density = 1
  expand = 3
  formula = Br
  name = G4_Br
  specific = 4
FEATURE [App::DocumentObjectGroupPython] Kr_element005  label="Kr_element : 004"  # scripted group (container) (typed FeaturePython)
  n = 1
  ref = Kr_element
FEATURE [App::DocumentObjectGroupPython] G4_Kr  # scripted group (container) (typed FeaturePython)
  Dunit = g/cm3
  Dvalue = 0.00347832
  Group = -> [Kr_element005]
  conduct = 2
  density = 1
  expand = 3
  formula = Kr
  name = G4_Kr
  specific = 4
FEATURE [App::DocumentObjectGroupPython] Rb_element005  label="Rb_element : 004"  # scripted group (container) (typed FeaturePython)
  n = 1
  ref = Rb_element
FEATURE [App::DocumentObjectGroupPython] G4_Rb  # scripted group (container) (typed FeaturePython)
  Dunit = g/cm3
  Dvalue = 1.532
  Group = -> [Rb_element005]
  conduct = 2
  density = 1
  expand = 3
  formula = Rb
  name = G4_Rb
  specific = 4
FEATURE [App::DocumentObjectGroupPython] Sr_element005  label="Sr_element : 004"  # scripted group (container) (typed FeaturePython)
  n = 1
  ref = Sr_element
FEATURE [App::DocumentObjectGroupPython] G4_Sr  # scripted group (container) (typed FeaturePython)
  Dunit = g/cm3
  Dvalue = 2.54
  Group = -> [Sr_element005]
  conduct = 2
  density = 1
  expand = 3
  formula = Sr
  name = G4_Sr
  specific = 4
FEATURE [App::DocumentObjectGroupPython] Y_element005  label="Y_element : 004"  # scripted group (container) (typed FeaturePython)
  n = 1
  ref = Y_element
FEATURE [App::DocumentObjectGroupPython] G4_Y  # scripted group (container) (typed FeaturePython)
  Dunit = g/cm3
  Dvalue = 4.469
  Group = -> [Y_element005]
  conduct = 2
  density = 1
  expand = 3
  formula = Y
  name = G4_Y
  specific = 4
FEATURE [App::DocumentObjectGroupPython] Zr_element005  label="Zr_element : 004"  # scripted group (container) (typed FeaturePython)
  n = 1
  ref = Zr_element
FEATURE [App::DocumentObjectGroupPython] G4_Zr  # scripted group (container) (typed FeaturePython)
  Dunit = g/cm3
  Dvalue = 6.506
  Group = -> [Zr_element005]
  conduct = 2
  density = 1
  expand = 3
  formula = Zr
  name = G4_Zr
  specific = 4
FEATURE [App::DocumentObjectGroupPython] Nb_element005  label="Nb_element : 004"  # scripted group (container) (typed FeaturePython)
  n = 1
  ref = Nb_element
FEATURE [App::DocumentObjectGroupPython] G4_Nb  # scripted group (container) (typed FeaturePython)
  Dunit = g/cm3
  Dvalue = 8.57
  Group = -> [Nb_element005]
  conduct = 2
  density = 1
  expand = 3
  formula = Nb
  name = G4_Nb
  specific = 4
FEATURE [App::DocumentObjectGroupPython] Mo_element005  label="Mo_element : 004"  # scripted group (container) (typed FeaturePython)
  n = 1
  ref = Mo_element
FEATURE [App::DocumentObjectGroupPython] G4_Mo  # scripted group (container) (typed FeaturePython)
  Dunit = g/cm3
  Dvalue = 10.22
  Group = -> [Mo_element005]
  conduct = 2
  density = 1
  expand = 3
  formula = Mo
  name = G4_Mo
  specific = 4
FEATURE [App::DocumentObjectGroupPython] Tc_element005  label="Tc_element : 004"  # scripted group (container) (typed FeaturePython)
  n = 1
  ref = Tc_element
FEATURE [App::DocumentObjectGroupPython] G4_Tc  # scripted group (container) (typed FeaturePython)
  Dunit = g/cm3
  Dvalue = 11.5
  Group = -> [Tc_element005]
  conduct = 2
  density = 1
  expand = 3
  formula = Tc
  name = G4_Tc
  specific = 4
FEATURE [App::DocumentObjectGroupPython] Ru_element005  label="Ru_element : 004"  # scripted group (container) (typed FeaturePython)
  n = 1
  ref = Ru_element
FEATURE [App::DocumentObjectGroupPython] G4_Ru  # scripted group (container) (typed FeaturePython)
  Dunit = g/cm3
  Dvalue = 12.41
  Group = -> [Ru_element005]
  conduct = 2
  density = 1
  expand = 3
  formula = Ru
  name = G4_Ru
  specific = 4
FEATURE [App::DocumentObjectGroupPython] Rh_element005  label="Rh_element : 004"  # scripted group (container) (typed FeaturePython)
  n = 1
  ref = Rh_element
FEATURE [App::DocumentObjectGroupPython] G4_Rh  # scripted group (container) (typed FeaturePython)
  Dunit = g/cm3
  Dvalue = 12.41
  Group = -> [Rh_element005]
  conduct = 2
  density = 1
  expand = 3
  formula = Rh
  name = G4_Rh
  specific = 4
FEATURE [App::DocumentObjectGroupPython] Pd_element005  label="Pd_element : 004"  # scripted group (container) (typed FeaturePython)
  n = 1
  ref = Pd_element
FEATURE [App::DocumentObjectGroupPython] G4_Pd  # scripted group (container) (typed FeaturePython)
  Dunit = g/cm3
  Dvalue = 12.02
  Group = -> [Pd_element005]
  conduct = 2
  density = 1
  expand = 3
  formula = Pd
  name = G4_Pd
  specific = 4
FEATURE [App::DocumentObjectGroupPython] Ag_element030  label="Ag_element : 019"  # scripted group (container) (typed FeaturePython)
  n = 1
  ref = Ag_element
FEATURE [App::DocumentObjectGroupPython] G4_Ag  # scripted group (container) (typed FeaturePython)
  Dunit = g/cm3
  Dvalue = 10.5
  Group = -> [Ag_element030]
  conduct = 2
  density = 1
  expand = 3
  formula = Ag
  name = G4_Ag
  specific = 4
FEATURE [App::DocumentObjectGroupPython] Cd_element015  label="Cd_element : 014"  # scripted group (container) (typed FeaturePython)
  n = 1
  ref = Cd_element
FEATURE [App::DocumentObjectGroupPython] G4_Cd  # scripted group (container) (typed FeaturePython)
  Dunit = g/cm3
  Dvalue = 8.65
  Group = -> [Cd_element015]
  conduct = 2
  density = 1
  expand = 3
  formula = Cd
  name = G4_Cd
  specific = 4
FEATURE [App::DocumentObjectGroupPython] In_element005  label="In_element : 004"  # scripted group (container) (typed FeaturePython)
  n = 1
  ref = In_element
FEATURE [App::DocumentObjectGroupPython] G4_In  # scripted group (container) (typed FeaturePython)
  Dunit = g/cm3
  Dvalue = 7.31
  Group = -> [In_element005]
  conduct = 2
  density = 1
  expand = 3
  formula = In
  name = G4_In
  specific = 4
FEATURE [App::DocumentObjectGroupPython] Sn_element005  label="Sn_element : 004"  # scripted group (container) (typed FeaturePython)
  n = 1
  ref = Sn_element
FEATURE [App::DocumentObjectGroupPython] G4_Sn  # scripted group (container) (typed FeaturePython)
  Dunit = g/cm3
  Dvalue = 7.31
  Group = -> [Sn_element005]
  conduct = 2
  density = 1
  expand = 3
  formula = Sn
  name = G4_Sn
  specific = 4
FEATURE [App::DocumentObjectGroupPython] Sb_element005  label="Sb_element : 004"  # scripted group (container) (typed FeaturePython)
  n = 1
  ref = Sb_element
FEATURE [App::DocumentObjectGroupPython] G4_Sb  # scripted group (container) (typed FeaturePython)
  Dunit = g/cm3
  Dvalue = 6.691
  Group = -> [Sb_element005]
  conduct = 2
  density = 1
  expand = 3
  formula = Sb
  name = G4_Sb
  specific = 4
FEATURE [App::DocumentObjectGroupPython] Te_element010  label="Te_element : 009"  # scripted group (container) (typed FeaturePython)
  n = 1
  ref = Te_element
FEATURE [App::DocumentObjectGroupPython] G4_Te  # scripted group (container) (typed FeaturePython)
  Dunit = g/cm3
  Dvalue = 6.24
  Group = -> [Te_element010]
  conduct = 2
  density = 1
  expand = 3
  formula = Te
  name = G4_Te
  specific = 4
FEATURE [App::DocumentObjectGroupPython] I_element050  label="I_element : 032"  # scripted group (container) (typed FeaturePython)
  n = 1
  ref = I_element
FEATURE [App::DocumentObjectGroupPython] G4_I  # scripted group (container) (typed FeaturePython)
  Dunit = g/cm3
  Dvalue = 4.93
  Group = -> [I_element050]
  conduct = 2
  density = 1
  expand = 3
  formula = I
  name = G4_I
  specific = 4
FEATURE [App::DocumentObjectGroupPython] Xe_element005  label="Xe_element : 004"  # scripted group (container) (typed FeaturePython)
  n = 1
  ref = Xe_element
FEATURE [App::DocumentObjectGroupPython] G4_Xe  # scripted group (container) (typed FeaturePython)
  Dunit = g/cm3
  Dvalue = 0.00548536
  Group = -> [Xe_element005]
  conduct = 2
  density = 1
  expand = 3
  formula = Xe
  name = G4_Xe
  specific = 4
FEATURE [App::DocumentObjectGroupPython] Cs_element015  label="Cs_element : 014"  # scripted group (container) (typed FeaturePython)
  n = 1
  ref = Cs_element
FEATURE [App::DocumentObjectGroupPython] G4_Cs  # scripted group (container) (typed FeaturePython)
  Dunit = g/cm3
  Dvalue = 1.873
  Group = -> [Cs_element015]
  conduct = 2
  density = 1
  expand = 3
  formula = Cs
  name = G4_Cs
  specific = 4
FEATURE [App::DocumentObjectGroupPython] Ba_element015  label="Ba_element : 014"  # scripted group (container) (typed FeaturePython)
  n = 1
  ref = Ba_element
FEATURE [App::DocumentObjectGroupPython] G4_Ba  # scripted group (container) (typed FeaturePython)
  Dunit = g/cm3
  Dvalue = 3.5
  Group = -> [Ba_element015]
  conduct = 2
  density = 1
  expand = 3
  formula = Ba
  name = G4_Ba
  specific = 4
FEATURE [App::DocumentObjectGroupPython] La_element015  label="La_element : 013"  # scripted group (container) (typed FeaturePython)
  n = 1
  ref = La_element
FEATURE [App::DocumentObjectGroupPython] G4_La  # scripted group (container) (typed FeaturePython)
  Dunit = g/cm3
  Dvalue = 6.154
  Group = -> [La_element015]
  conduct = 2
  density = 1
  expand = 3
  formula = La
  name = G4_La
  specific = 4
FEATURE [App::DocumentObjectGroupPython] Ce_element010  label="Ce_element : 004"  # scripted group (container) (typed FeaturePython)
  n = 1
  ref = Ce_element
FEATURE [App::DocumentObjectGroupPython] G4_Ce  # scripted group (container) (typed FeaturePython)
  Dunit = g/cm3
  Dvalue = 6.657
  Group = -> [Ce_element010]
  conduct = 2
  density = 1
  expand = 3
  formula = Ce
  name = G4_Ce
  specific = 4
FEATURE [App::DocumentObjectGroupPython] Pr_element005  label="Pr_element : 004"  # scripted group (container) (typed FeaturePython)
  n = 1
  ref = Pr_element
FEATURE [App::DocumentObjectGroupPython] G4_Pr  # scripted group (container) (typed FeaturePython)
  Dunit = g/cm3
  Dvalue = 6.71
  Group = -> [Pr_element005]
  conduct = 2
  density = 1
  expand = 3
  formula = Pr
  name = G4_Pr
  specific = 4
FEATURE [App::DocumentObjectGroupPython] Nd_element005  label="Nd_element : 004"  # scripted group (container) (typed FeaturePython)
  n = 1
  ref = Nd_element
FEATURE [App::DocumentObjectGroupPython] G4_Nd  # scripted group (container) (typed FeaturePython)
  Dunit = g/cm3
  Dvalue = 6.9
  Group = -> [Nd_element005]
  conduct = 2
  density = 1
  expand = 3
  formula = Nd
  name = G4_Nd
  specific = 4
FEATURE [App::DocumentObjectGroupPython] Pm_element005  label="Pm_element : 004"  # scripted group (container) (typed FeaturePython)
  n = 1
  ref = Pm_element
FEATURE [App::DocumentObjectGroupPython] G4_Pm  # scripted group (container) (typed FeaturePython)
  Dunit = g/cm3
  Dvalue = 7.22
  Group = -> [Pm_element005]
  conduct = 2
  density = 1
  expand = 3
  formula = Pm
  name = G4_Pm
  specific = 4
FEATURE [App::DocumentObjectGroupPython] Sm_element005  label="Sm_element : 004"  # scripted group (container) (typed FeaturePython)
  n = 1
  ref = Sm_element
FEATURE [App::DocumentObjectGroupPython] G4_Sm  # scripted group (container) (typed FeaturePython)
  Dunit = g/cm3
  Dvalue = 7.46
  Group = -> [Sm_element005]
  conduct = 2
  density = 1
  expand = 3
  formula = Sm
  name = G4_Sm
  specific = 4
FEATURE [App::DocumentObjectGroupPython] Eu_element005  label="Eu_element : 004"  # scripted group (container) (typed FeaturePython)
  n = 1
  ref = Eu_element
FEATURE [App::DocumentObjectGroupPython] G4_Eu  # scripted group (container) (typed FeaturePython)
  Dunit = g/cm3
  Dvalue = 5.243
  Group = -> [Eu_element005]
  conduct = 2
  density = 1
  expand = 3
  formula = Eu
  name = G4_Eu
  specific = 4
FEATURE [App::DocumentObjectGroupPython] Gd_element010  label="Gd_element : 008"  # scripted group (container) (typed FeaturePython)
  n = 1
  ref = Gd_element
FEATURE [App::DocumentObjectGroupPython] G4_Gd  # scripted group (container) (typed FeaturePython)
  Dunit = g/cm3
  Dvalue = 7.9004
  Group = -> [Gd_element010]
  conduct = 2
  density = 1
  expand = 3
  formula = Gd
  name = G4_Gd
  specific = 4
FEATURE [App::DocumentObjectGroupPython] Tb_element005  label="Tb_element : 004"  # scripted group (container) (typed FeaturePython)
  n = 1
  ref = Tb_element
FEATURE [App::DocumentObjectGroupPython] G4_Tb  # scripted group (container) (typed FeaturePython)
  Dunit = g/cm3
  Dvalue = 8.229
  Group = -> [Tb_element005]
  conduct = 2
  density = 1
  expand = 3
  formula = Tb
  name = G4_Tb
  specific = 4
FEATURE [App::DocumentObjectGroupPython] Dy_element005  label="Dy_element : 004"  # scripted group (container) (typed FeaturePython)
  n = 1
  ref = Dy_element
FEATURE [App::DocumentObjectGroupPython] G4_Dy  # scripted group (container) (typed FeaturePython)
  Dunit = g/cm3
  Dvalue = 8.55
  Group = -> [Dy_element005]
  conduct = 2
  density = 1
  expand = 3
  formula = Dy
  name = G4_Dy
  specific = 4
FEATURE [App::DocumentObjectGroupPython] Ho_element005  label="Ho_element : 004"  # scripted group (container) (typed FeaturePython)
  n = 1
  ref = Ho_element
FEATURE [App::DocumentObjectGroupPython] G4_Ho  # scripted group (container) (typed FeaturePython)
  Dunit = g/cm3
  Dvalue = 8.795
  Group = -> [Ho_element005]
  conduct = 2
  density = 1
  expand = 3
  formula = Ho
  name = G4_Ho
  specific = 4
FEATURE [App::DocumentObjectGroupPython] Er_element005  label="Er_element : 004"  # scripted group (container) (typed FeaturePython)
  n = 1
  ref = Er_element
FEATURE [App::DocumentObjectGroupPython] G4_Er  # scripted group (container) (typed FeaturePython)
  Dunit = g/cm3
  Dvalue = 9.066
  Group = -> [Er_element005]
  conduct = 2
  density = 1
  expand = 3
  formula = Er
  name = G4_Er
  specific = 4
FEATURE [App::DocumentObjectGroupPython] Tm_element005  label="Tm_element : 004"  # scripted group (container) (typed FeaturePython)
  n = 1
  ref = Tm_element
FEATURE [App::DocumentObjectGroupPython] G4_Tm  # scripted group (container) (typed FeaturePython)
  Dunit = g/cm3
  Dvalue = 9.321
  Group = -> [Tm_element005]
  conduct = 2
  density = 1
  expand = 3
  formula = Tm
  name = G4_Tm
  specific = 4
FEATURE [App::DocumentObjectGroupPython] Yb_element005  label="Yb_element : 004"  # scripted group (container) (typed FeaturePython)
  n = 1
  ref = Yb_element
FEATURE [App::DocumentObjectGroupPython] G4_Yb  # scripted group (container) (typed FeaturePython)
  Dunit = g/cm3
  Dvalue = 6.73
  Group = -> [Yb_element005]
  conduct = 2
  density = 1
  expand = 3
  formula = Yb
  name = G4_Yb
  specific = 4
FEATURE [App::DocumentObjectGroupPython] Lu_element005  label="Lu_element : 004"  # scripted group (container) (typed FeaturePython)
  n = 1
  ref = Lu_element
FEATURE [App::DocumentObjectGroupPython] G4_Lu  # scripted group (container) (typed FeaturePython)
  Dunit = g/cm3
  Dvalue = 9.84
  Group = -> [Lu_element005]
  conduct = 2
  density = 1
  expand = 3
  formula = Lu
  name = G4_Lu
  specific = 4
FEATURE [App::DocumentObjectGroupPython] Hf_element005  label="Hf_element : 004"  # scripted group (container) (typed FeaturePython)
  n = 1
  ref = Hf_element
FEATURE [App::DocumentObjectGroupPython] G4_Hf  # scripted group (container) (typed FeaturePython)
  Dunit = g/cm3
  Dvalue = 13.31
  Group = -> [Hf_element005]
  conduct = 2
  density = 1
  expand = 3
  formula = Hf
  name = G4_Hf
  specific = 4
FEATURE [App::DocumentObjectGroupPython] Ta_element005  label="Ta_element : 004"  # scripted group (container) (typed FeaturePython)
  n = 1
  ref = Ta_element
FEATURE [App::DocumentObjectGroupPython] G4_Ta  # scripted group (container) (typed FeaturePython)
  Dunit = g/cm3
  Dvalue = 16.654
  Group = -> [Ta_element005]
  conduct = 2
  density = 1
  expand = 3
  formula = Ta
  name = G4_Ta
  specific = 4
FEATURE [App::DocumentObjectGroupPython] W_element024  label="W_element : 023"  # scripted group (container) (typed FeaturePython)
  n = 1
  ref = W_element
FEATURE [App::DocumentObjectGroupPython] G4_W  # scripted group (container) (typed FeaturePython)
  Dunit = g/cm3
  Dvalue = 19.3
  Group = -> [W_element024]
  conduct = 2
  density = 1
  expand = 3
  formula = W
  name = G4_W
  specific = 4
FEATURE [App::DocumentObjectGroupPython] Re_element005  label="Re_element : 004"  # scripted group (container) (typed FeaturePython)
  n = 1
  ref = Re_element
FEATURE [App::DocumentObjectGroupPython] G4_Re  # scripted group (container) (typed FeaturePython)
  Dunit = g/cm3
  Dvalue = 21.02
  Group = -> [Re_element005]
  conduct = 2
  density = 1
  expand = 3
  formula = Re
  name = G4_Re
  specific = 4
FEATURE [App::DocumentObjectGroupPython] Os_element005  label="Os_element : 004"  # scripted group (container) (typed FeaturePython)
  n = 1
  ref = Os_element
FEATURE [App::DocumentObjectGroupPython] G4_Os  # scripted group (container) (typed FeaturePython)
  Dunit = g/cm3
  Dvalue = 22.57
  Group = -> [Os_element005]
  conduct = 2
  density = 1
  expand = 3
  formula = Os
  name = G4_Os
  specific = 4
FEATURE [App::DocumentObjectGroupPython] Ir_element005  label="Ir_element : 004"  # scripted group (container) (typed FeaturePython)
  n = 1
  ref = Ir_element
FEATURE [App::DocumentObjectGroupPython] G4_Ir  # scripted group (container) (typed FeaturePython)
  Dunit = g/cm3
  Dvalue = 22.42
  Group = -> [Ir_element005]
  conduct = 2
  density = 1
  expand = 3
  formula = Ir
  name = G4_Ir
  specific = 4
FEATURE [App::DocumentObjectGroupPython] Pt_element005  label="Pt_element : 004"  # scripted group (container) (typed FeaturePython)
  n = 1
  ref = Pt_element
FEATURE [App::DocumentObjectGroupPython] G4_Pt  # scripted group (container) (typed FeaturePython)
  Dunit = g/cm3
  Dvalue = 21.45
  Group = -> [Pt_element005]
  conduct = 2
  density = 1
  expand = 3
  formula = Pt
  name = G4_Pt
  specific = 4
FEATURE [App::DocumentObjectGroupPython] Au_element005  label="Au_element : 004"  # scripted group (container) (typed FeaturePython)
  n = 1
  ref = Au_element
FEATURE [App::DocumentObjectGroupPython] G4_Au  # scripted group (container) (typed FeaturePython)
  Dunit = g/cm3
  Dvalue = 19.32
  Group = -> [Au_element005]
  conduct = 2
  density = 1
  expand = 3
  formula = Au
  name = G4_Au
  specific = 4
FEATURE [App::DocumentObjectGroupPython] Hg_element010  label="Hg_element : 009"  # scripted group (container) (typed FeaturePython)
  n = 1
  ref = Hg_element
FEATURE [App::DocumentObjectGroupPython] G4_Hg  # scripted group (container) (typed FeaturePython)
  Dunit = g/cm3
  Dvalue = 13.546
  Group = -> [Hg_element010]
  conduct = 2
  density = 1
  expand = 3
  formula = Hg
  name = G4_Hg
  specific = 4
FEATURE [App::DocumentObjectGroupPython] Tl_element010  label="Tl_element : 009"  # scripted group (container) (typed FeaturePython)
  n = 1
  ref = Tl_element
FEATURE [App::DocumentObjectGroupPython] G4_Tl  # scripted group (container) (typed FeaturePython)
  Dunit = g/cm3
  Dvalue = 11.72
  Group = -> [Tl_element010]
  conduct = 2
  density = 1
  expand = 3
  formula = Tl
  name = G4_Tl
  specific = 4
FEATURE [App::DocumentObjectGroupPython] Pb_element027  label="Pb_element : 012"  # scripted group (container) (typed FeaturePython)
  n = 1
  ref = Pb_element
FEATURE [App::DocumentObjectGroupPython] G4_Pb  # scripted group (container) (typed FeaturePython)
  Dunit = g/cm3
  Dvalue = 11.35
  Group = -> [Pb_element027]
  conduct = 2
  density = 1
  expand = 3
  formula = Pb
  name = G4_Pb
  specific = 4
FEATURE [App::DocumentObjectGroupPython] Bi_element010  label="Bi_element : 010"  # scripted group (container) (typed FeaturePython)
  n = 1
  ref = Bi_element
FEATURE [App::DocumentObjectGroupPython] G4_Bi  # scripted group (container) (typed FeaturePython)
  Dunit = g/cm3
  Dvalue = 9.747
  Group = -> [Bi_element010]
  conduct = 2
  density = 1
  expand = 3
  formula = Bi
  name = G4_Bi
  specific = 4
FEATURE [App::DocumentObjectGroupPython] Po_element005  label="Po_element : 004"  # scripted group (container) (typed FeaturePython)
  n = 1
  ref = Po_element
FEATURE [App::DocumentObjectGroupPython] G4_Po  # scripted group (container) (typed FeaturePython)
  Dunit = g/cm3
  Dvalue = 9.32
  Group = -> [Po_element005]
  conduct = 2
  density = 1
  expand = 3
  formula = Po
  name = G4_Po
  specific = 4
FEATURE [App::DocumentObjectGroupPython] At_element005  label="At_element : 004"  # scripted group (container) (typed FeaturePython)
  n = 1
  ref = At_element
FEATURE [App::DocumentObjectGroupPython] G4_At  # scripted group (container) (typed FeaturePython)
  Dunit = g/cm3
  Dvalue = 9.32
  Group = -> [At_element005]
  conduct = 2
  density = 1
  expand = 3
  formula = At
  name = G4_At
  specific = 4
FEATURE [App::DocumentObjectGroupPython] Rn_element005  label="Rn_element : 004"  # scripted group (container) (typed FeaturePython)
  n = 1
  ref = Rn_element
FEATURE [App::DocumentObjectGroupPython] G4_Rn  # scripted group (container) (typed FeaturePython)
  Dunit = g/cm3
  Dvalue = 0.00900662
  Group = -> [Rn_element005]
  conduct = 2
  density = 1
  expand = 3
  formula = Rn
  name = G4_Rn
  specific = 4
FEATURE [App::DocumentObjectGroupPython] Fr_element005  label="Fr_element : 004"  # scripted group (container) (typed FeaturePython)
  n = 1
  ref = Fr_element
FEATURE [App::DocumentObjectGroupPython] G4_Fr  # scripted group (container) (typed FeaturePython)
  Dunit = g/cm3
  Dvalue = 1
  Group = -> [Fr_element005]
  conduct = 2
  density = 1
  expand = 3
  formula = Fr
  name = G4_Fr
  specific = 4
FEATURE [App::DocumentObjectGroupPython] Ra_element005  label="Ra_element : 004"  # scripted group (container) (typed FeaturePython)
  n = 1
  ref = Ra_element
FEATURE [App::DocumentObjectGroupPython] G4_Ra  # scripted group (container) (typed FeaturePython)
  Dunit = g/cm3
  Dvalue = 5
  Group = -> [Ra_element005]
  conduct = 2
  density = 1
  expand = 3
  formula = Ra
  name = G4_Ra
  specific = 4
FEATURE [App::DocumentObjectGroupPython] Ac_element005  label="Ac_element : 004"  # scripted group (container) (typed FeaturePython)
  n = 1
  ref = Ac_element
FEATURE [App::DocumentObjectGroupPython] G4_Ac  # scripted group (container) (typed FeaturePython)
  Dunit = g/cm3
  Dvalue = 10.07
  Group = -> [Ac_element005]
  conduct = 2
  density = 1
  expand = 3
  formula = Ac
  name = G4_Ac
  specific = 4
FEATURE [App::DocumentObjectGroupPython] Th_element005  label="Th_element : 004"  # scripted group (container) (typed FeaturePython)
  n = 1
  ref = Th_element
FEATURE [App::DocumentObjectGroupPython] G4_Th  # scripted group (container) (typed FeaturePython)
  Dunit = g/cm3
  Dvalue = 11.72
  Group = -> [Th_element005]
  conduct = 2
  density = 1
  expand = 3
  formula = Th
  name = G4_Th
  specific = 4
FEATURE [App::DocumentObjectGroupPython] Pa_element005  label="Pa_element : 004"  # scripted group (container) (typed FeaturePython)
  n = 1
  ref = Pa_element
FEATURE [App::DocumentObjectGroupPython] G4_Pa  # scripted group (container) (typed FeaturePython)
  Dunit = g/cm3
  Dvalue = 15.37
  Group = -> [Pa_element005]
  conduct = 2
  density = 1
  expand = 3
  formula = Pa
  name = G4_Pa
  specific = 4
FEATURE [App::DocumentObjectGroupPython] U_element020  label="U_element : 019"  # scripted group (container) (typed FeaturePython)
  n = 1
  ref = U_element
FEATURE [App::DocumentObjectGroupPython] G4_U  # scripted group (container) (typed FeaturePython)
  Dunit = g/cm3
  Dvalue = 18.95
  Group = -> [U_element020]
  conduct = 2
  density = 1
  expand = 3
  formula = U
  name = G4_U
  specific = 4
FEATURE [App::DocumentObjectGroupPython] Np_element005  label="Np_element : 004"  # scripted group (container) (typed FeaturePython)
  n = 1
  ref = Np_element
FEATURE [App::DocumentObjectGroupPython] G4_Np  # scripted group (container) (typed FeaturePython)
  Dunit = g/cm3
  Dvalue = 20.25
  Group = -> [Np_element005]
  conduct = 2
  density = 1
  expand = 3
  formula = Np
  name = G4_Np
  specific = 4
FEATURE [App::DocumentObjectGroupPython] Pu_element010  label="Pu_element : 009"  # scripted group (container) (typed FeaturePython)
  n = 1
  ref = Pu_element
FEATURE [App::DocumentObjectGroupPython] G4_Pu  # scripted group (container) (typed FeaturePython)
  Dunit = g/cm3
  Dvalue = 19.84
  Group = -> [Pu_element010]
  conduct = 2
  density = 1
  expand = 3
  formula = Pu
  name = G4_Pu
  specific = 4
FEATURE [App::DocumentObjectGroupPython] Am_element005  label="Am_element : 004"  # scripted group (container) (typed FeaturePython)
  n = 1
  ref = Am_element
FEATURE [App::DocumentObjectGroupPython] G4_Am  # scripted group (container) (typed FeaturePython)
  Dunit = g/cm3
  Dvalue = 13.67
  Group = -> [Am_element005]
  conduct = 2
  density = 1
  expand = 3
  formula = Am
  name = G4_Am
  specific = 4
FEATURE [App::DocumentObjectGroupPython] Cm_element005  label="Cm_element : 004"  # scripted group (container) (typed FeaturePython)
  n = 1
  ref = Cm_element
FEATURE [App::DocumentObjectGroupPython] G4_Cm  # scripted group (container) (typed FeaturePython)
  Dunit = g/cm3
  Dvalue = 13.51
  Group = -> [Cm_element005]
  conduct = 2
  density = 1
  expand = 3
  formula = Cm
  name = G4_Cm
  specific = 4
FEATURE [App::DocumentObjectGroupPython] Bk_element005  label="Bk_element : 004"  # scripted group (container) (typed FeaturePython)
  n = 1
  ref = Bk_element
FEATURE [App::DocumentObjectGroupPython] G4_Bk  # scripted group (container) (typed FeaturePython)
  Dunit = g/cm3
  Dvalue = 14
  Group = -> [Bk_element005]
  conduct = 2
  density = 1
  expand = 3
  formula = Bk
  name = G4_Bk
  specific = 4
FEATURE [App::DocumentObjectGroupPython] Cf_element005  label="Cf_element : 004"  # scripted group (container) (typed FeaturePython)
  n = 1
  ref = Cf_element
FEATURE [App::DocumentObjectGroupPython] G4_Cf  # scripted group (container) (typed FeaturePython)
  Dunit = g/cm3
  Dvalue = 10
  Group = -> [Cf_element005]
  conduct = 2
  density = 1
  expand = 3
  formula = Cf
  name = G4_Cf
  specific = 4
FEATURE [App::DocumentObjectGroupPython] Element  # scripted group (container) (typed FeaturePython)
  Group = -> [G4_H,G4_He,G4_Li,G4_Be,G4_B,G4_C,G4_N,G4_O,G4_F,G4_Ne,G4_Na,G4_Mg,G4_Al,G4_Si,G4_P,G4_S,G4_Cl,G4_Ar,G4_K,G4_Ca,G4_Sc,G4_Ti,G4_V,G4_Cr,G4_Mn,G4_Fe,G4_Co,G4_Ni,G4_Cu,G4_Zn,G4_Ga,G4_Ge,G4_As,G4_Se,G4_Br,G4_Kr,G4_Rb,G4_Sr,G4_Y,G4_Zr,G4_Nb,G4_Mo,G4_Tc,G4_Ru,G4_Rh,G4_Pd,G4_Ag,G4_Cd,G4_In,G4_Sn,G4_Sb,G4_Te,G4_I,G4_Xe,G4_Cs,G4_Ba,G4_La,G4_Ce,G4_Pr,G4_Nd,G4_Pm,G4_Sm,G4_Eu,G4_Gd,G4_Tb,G4_Dy,G4_Ho,G4_Er,+30 more]
FEATURE [App::DocumentObjectGroupPython] H_element666  label="H_element : 431"  # scripted group (container) (typed FeaturePython)
  n = 2
  ref = H_element
FEATURE [App::DocumentObjectGroupPython] G4_lH2  # scripted group (container) (typed FeaturePython)
  Dunit = g/cm3
  Dvalue = 0.0708
  Group = -> [H_element666]
  conduct = 2
  density = 1
  expand = 3
  formula = G4_lH2
  name = G4_lH2
  specific = 4
FEATURE [App::DocumentObjectGroupPython] N_element321  label="N_element : 173"  # scripted group (container) (typed FeaturePython)
  n = 2
  ref = N_element
FEATURE [App::DocumentObjectGroupPython] G4_lN2  # scripted group (container) (typed FeaturePython)
  Dunit = g/cm3
  Dvalue = 0.807
  Group = -> [N_element321]
  conduct = 2
  density = 1
  expand = 3
  formula = G4_lN2
  name = G4_lN2
  specific = 4
FEATURE [App::DocumentObjectGroupPython] O_element626  label="O_element : 399"  # scripted group (container) (typed FeaturePython)
  n = 2
  ref = O_element
FEATURE [App::DocumentObjectGroupPython] G4_lO2  # scripted group (container) (typed FeaturePython)
  Dunit = g/cm3
  Dvalue = 1.141
  Group = -> [O_element626]
  conduct = 2
  density = 1
  expand = 3
  formula = G4_lO2
  name = G4_lO2
  specific = 4
FEATURE [App::DocumentObjectGroupPython] Ar003  label="Ar : 004"  # scripted group (container) (typed FeaturePython)
  n = 1
  ref = Ar
FEATURE [App::DocumentObjectGroupPython] G4_lAr  # scripted group (container) (typed FeaturePython)
  Dunit = g/cm3
  Dvalue = 1.396
  Group = -> [Ar003]
  conduct = 2
  density = 1
  expand = 3
  formula = G4_lAr
  name = G4_lAr
  specific = 4
FEATURE [App::DocumentObjectGroupPython] Br003  label="Br : 004"  # scripted group (container) (typed FeaturePython)
  n = 1
  ref = Br
FEATURE [App::DocumentObjectGroupPython] G4_lBr  # scripted group (container) (typed FeaturePython)
  Dunit = g/cm3
  Dvalue = 3.1028
  Group = -> [Br003]
  conduct = 2
  density = 1
  expand = 3
  formula = G4_lBr
  name = G4_lBr
  specific = 4
FEATURE [App::DocumentObjectGroupPython] Kr003  label="Kr : 004"  # scripted group (container) (typed FeaturePython)
  n = 1
  ref = Kr
FEATURE [App::DocumentObjectGroupPython] G4_lKr  # scripted group (container) (typed FeaturePython)
  Dunit = g/cm3
  Dvalue = 2.418
  Group = -> [Kr003]
  conduct = 2
  density = 1
  expand = 3
  formula = G4_lKr
  name = G4_lKr
  specific = 4
FEATURE [App::DocumentObjectGroupPython] Xe003  label="Xe : 004"  # scripted group (container) (typed FeaturePython)
  n = 1
  ref = Xe
FEATURE [App::DocumentObjectGroupPython] G4_lXe  # scripted group (container) (typed FeaturePython)
  Dunit = g/cm3
  Dvalue = 2.953
  Group = -> [Xe003]
  conduct = 2
  density = 1
  expand = 3
  formula = G4_lXe
  name = G4_lXe
  specific = 4
FEATURE [App::DocumentObjectGroupPython] O_element627  label="O_element : 400"  # scripted group (container) (typed FeaturePython)
  n = 4
  ref = O_element
FEATURE [App::DocumentObjectGroupPython] Pb_element028  label="Pb_element : 013"  # scripted group (container) (typed FeaturePython)
  n = 1
  ref = Pb_element
FEATURE [App::DocumentObjectGroupPython] W_element025  label="W_element : 024"  # scripted group (container) (typed FeaturePython)
  n = 1
  ref = W_element
FEATURE [App::DocumentObjectGroupPython] G4_PbWO4  # scripted group (container) (typed FeaturePython)
  Dunit = g/cm3
  Dvalue = 8.28
  Group = -> [O_element627,Pb_element028,W_element025]
  conduct = 2
  density = 1
  expand = 3
  formula = G4_PbWO4
  name = G4_PbWO4
  specific = 4
FEATURE [App::DocumentObjectGroupPython] alactic003  label="alactic : 004"  # scripted group (container) (typed FeaturePython)
  n = 1
  ref = alactic
FEATURE [App::DocumentObjectGroupPython] G4_Galactic  # scripted group (container) (typed FeaturePython)
  Dunit = g/cm3
  Dvalue = 0
  Group = -> [alactic003]
  conduct = 2
  density = 1
  expand = 3
  formula = G4_Galactic
  name = G4_Galactic
  specific = 4
FEATURE [App::DocumentObjectGroupPython] RAPHITE_POROUS003  label="RAPHITE_POROUS : 004"  # scripted group (container) (typed FeaturePython)
  n = 1
  ref = RAPHITE_POROUS
FEATURE [App::DocumentObjectGroupPython] G4_GRAPHITE_POROUS  # scripted group (container) (typed FeaturePython)
  Dunit = g/cm3
  Dvalue = 1.7
  Group = -> [RAPHITE_POROUS003]
  conduct = 2
  density = 1
  expand = 3
  formula = G4_GRAPHITE_POROUS
  name = G4_GRAPHITE_POROUS
  specific = 4
FEATURE [App::DocumentObjectGroupPython] H_element667  label="H_element : 0.286"  # scripted group (container) (typed FeaturePython)
  n = 0.080538
FEATURE [App::DocumentObjectGroupPython] C_element717  label="C_element : 0.1017"  # scripted group (container) (typed FeaturePython)
  n = 0.599848
FEATURE [App::DocumentObjectGroupPython] O_element628  label="O_element : 0.1007"  # scripted group (container) (typed FeaturePython)
  n = 0.319614
FEATURE [App::DocumentObjectGroupPython] G4_LUCITE  # scripted group (container) (typed FeaturePython)
  Dunit = g/cm3
  Dvalue = 1.19
  Group = -> [H_element667,C_element717,O_element628]
  conduct = 2
  density = 1
  expand = 3
  formula = G4_LUCITE
  name = G4_LUCITE
  specific = 4
FEATURE [App::DocumentObjectGroupPython] Cu_element014  label="Cu_element : 097"  # scripted group (container) (typed FeaturePython)
  n = 62
  ref = Cu_element
FEATURE [App::DocumentObjectGroupPython] Zn_element014  label="Zn_element : 043"  # scripted group (container) (typed FeaturePython)
  n = 35
  ref = Zn_element
FEATURE [App::DocumentObjectGroupPython] Pb_element029  label="Pb_element : 014"  # scripted group (container) (typed FeaturePython)
  n = 3
  ref = Pb_element
FEATURE [App::DocumentObjectGroupPython] G4_BRASS  # scripted group (container) (typed FeaturePython)
  Dunit = g/cm3
  Dvalue = 8.52
  Group = -> [Cu_element014,Zn_element014,Pb_element029]
  conduct = 2
  density = 1
  expand = 3
  formula = G4_BRASS
  name = G4_BRASS
  specific = 4
FEATURE [App::DocumentObjectGroupPython] Cu_element015  label="Cu_element : 098"  # scripted group (container) (typed FeaturePython)
  n = 89
  ref = Cu_element
FEATURE [App::DocumentObjectGroupPython] Zn_element015  label="Zn_element : 044"  # scripted group (container) (typed FeaturePython)
  n = 9
  ref = Zn_element
FEATURE [App::DocumentObjectGroupPython] Pb_element030  label="Pb_element : 015"  # scripted group (container) (typed FeaturePython)
  n = 2
  ref = Pb_element
FEATURE [App::DocumentObjectGroupPython] G4_BRONZE  # scripted group (container) (typed FeaturePython)
  Dunit = g/cm3
  Dvalue = 8.82
  Group = -> [Cu_element015,Zn_element015,Pb_element030]
  conduct = 2
  density = 1
  expand = 3
  formula = G4_BRONZE
  name = G4_BRONZE
  specific = 4
FEATURE [App::DocumentObjectGroupPython] Fe_element040  label="Fe_element : 021"  # scripted group (container) (typed FeaturePython)
  n = 74
  ref = Fe_element
FEATURE [App::DocumentObjectGroupPython] Cr_element010  label="Cr_element : 024"  # scripted group (container) (typed FeaturePython)
  n = 18
  ref = Cr_element
FEATURE [App::DocumentObjectGroupPython] Ni_element010  label="Ni_element : 014"  # scripted group (container) (typed FeaturePython)
  n = 8
  ref = Ni_element
FEATURE [App::DocumentObjectGroupPython] G4_STAINLESS_STEEL  label="G4_STAINLESS-STEEL"  # scripted group (container) (typed FeaturePython)
  Dunit = g/cm3
  Dvalue = 8
  Group = -> [Fe_element040,Cr_element010,Ni_element010]
  conduct = 2
  density = 1
  expand = 3
  formula = G4_STAINLESS-STEEL
  name = G4_STAINLESS-STEEL
  specific = 4
FEATURE [App::DocumentObjectGroupPython] H_element668  label="H_element : 432"  # scripted group (container) (typed FeaturePython)
  n = 18
  ref = H_element
FEATURE [App::DocumentObjectGroupPython] C_element718  label="C_element : 471"  # scripted group (container) (typed FeaturePython)
  n = 12
  ref = C_element
FEATURE [App::DocumentObjectGroupPython] O_element629  label="O_element : 401"  # scripted group (container) (typed FeaturePython)
  n = 7
  ref = O_element
FEATURE [App::DocumentObjectGroupPython] G4_CR39  # scripted group (container) (typed FeaturePython)
  Dunit = g/cm3
  Dvalue = 1.32
  Group = -> [H_element668,C_element718,O_element629]
  conduct = 2
  density = 1
  expand = 3
  formula = G4_CR39
  name = G4_CR39
  specific = 4
FEATURE [App::DocumentObjectGroupPython] H_element669  label="H_element : 433"  # scripted group (container) (typed FeaturePython)
  n = 38
  ref = H_element
FEATURE [App::DocumentObjectGroupPython] C_element719  label="C_element : 472"  # scripted group (container) (typed FeaturePython)
  n = 18
  ref = C_element
FEATURE [App::DocumentObjectGroupPython] O_element630  label="O_element : 402"  # scripted group (container) (typed FeaturePython)
  n = 1
  ref = O_element
FEATURE [App::DocumentObjectGroupPython] G4_OCTADECANOL  # scripted group (container) (typed FeaturePython)
  Dunit = g/cm3
  Dvalue = 0.812
  Group = -> [H_element669,C_element719,O_element630]
  conduct = 2
  density = 1
  expand = 3
  formula = G4_OCTADECANOL
  name = G4_OCTADECANOL
  specific = 4
FEATURE [App::DocumentObjectGroupPython] HEP  # scripted group (container) (typed FeaturePython)
  Group = -> [G4_lH2,G4_lN2,G4_lO2,G4_lAr,G4_lBr,G4_lKr,G4_lXe,G4_PbWO4,G4_Galactic,G4_GRAPHITE_POROUS,G4_LUCITE,G4_BRASS,G4_BRONZE,G4_STAINLESS_STEEL,G4_CR39,G4_OCTADECANOL]
FEATURE [App::DocumentObjectGroupPython] C_element720  label="C_element : 473"  # scripted group (container) (typed FeaturePython)
  n = 14
  ref = C_element
FEATURE [App::DocumentObjectGroupPython] H_element670  label="H_element : 434"  # scripted group (container) (typed FeaturePython)
  n = 10
  ref = H_element
FEATURE [App::DocumentObjectGroupPython] O_element631  label="O_element : 403"  # scripted group (container) (typed FeaturePython)
  n = 2
  ref = O_element
FEATURE [App::DocumentObjectGroupPython] N_element322  label="N_element : 174"  # scripted group (container) (typed FeaturePython)
  n = 2
  ref = N_element
FEATURE [App::DocumentObjectGroupPython] G4_KEVLAR  # scripted group (container) (typed FeaturePython)
  Dunit = g/cm3
  Dvalue = 1.44
  Group = -> [C_element720,H_element670,O_element631,N_element322]
  conduct = 2
  density = 1
  expand = 3
  formula = G4_KEVLAR
  name = G4_KEVLAR
  specific = 4
FEATURE [App::DocumentObjectGroupPython] C_element721  label="C_element : 474"  # scripted group (container) (typed FeaturePython)
  n = 10
  ref = C_element
FEATURE [App::DocumentObjectGroupPython] H_element671  label="H_element : 435"  # scripted group (container) (typed FeaturePython)
  n = 8
  ref = H_element
FEATURE [App::DocumentObjectGroupPython] O_element632  label="O_element : 404"  # scripted group (container) (typed FeaturePython)
  n = 4
  ref = O_element
FEATURE [App::DocumentObjectGroupPython] G4_DACRON  # scripted group (container) (typed FeaturePython)
  Dunit = g/cm3
  Dvalue = 1.4
  Group = -> [C_element721,H_element671,O_element632]
  conduct = 2
  density = 1
  expand = 3
  formula = G4_DACRON
  name = G4_DACRON
  specific = 4
FEATURE [App::DocumentObjectGroupPython] C_element722  label="C_element : 475"  # scripted group (container) (typed FeaturePython)
  n = 4
  ref = C_element
FEATURE [App::DocumentObjectGroupPython] H_element672  label="H_element : 436"  # scripted group (container) (typed FeaturePython)
  n = 5
  ref = H_element
FEATURE [App::DocumentObjectGroupPython] Cl_element150  label="Cl_element : 076"  # scripted group (container) (typed FeaturePython)
  n = 1
  ref = Cl_element
FEATURE [App::DocumentObjectGroupPython] G4_NEOPRENE  # scripted group (container) (typed FeaturePython)
  Dunit = g/cm3
  Dvalue = 1.23
  Group = -> [C_element722,H_element672,Cl_element150]
  conduct = 2
  density = 1
  expand = 3
  formula = G4_NEOPRENE
  name = G4_NEOPRENE
  specific = 4
FEATURE [App::DocumentObjectGroupPython] Space  # scripted group (container) (typed FeaturePython)
  Group = -> [G4_KEVLAR,G4_DACRON,G4_NEOPRENE]
FEATURE [App::DocumentObjectGroupPython] H_element673  label="H_element : 437"  # scripted group (container) (typed FeaturePython)
  n = 5
  ref = H_element
FEATURE [App::DocumentObjectGroupPython] C_element723  label="C_element : 476"  # scripted group (container) (typed FeaturePython)
  n = 4
  ref = C_element
FEATURE [App::DocumentObjectGroupPython] N_element323  label="N_element : 175"  # scripted group (container) (typed FeaturePython)
  n = 3
  ref = N_element
FEATURE [App::DocumentObjectGroupPython] O_element633  label="O_element : 405"  # scripted group (container) (typed FeaturePython)
  n = 1
  ref = O_element
FEATURE [App::DocumentObjectGroupPython] G4_CYTOSINE  # scripted group (container) (typed FeaturePython)
  Dunit = g/cm3
  Dvalue = 1.55
  Group = -> [H_element673,C_element723,N_element323,O_element633]
  conduct = 2
  density = 1
  expand = 3
  formula = G4_CYTOSINE
  name = G4_CYTOSINE
  specific = 4
FEATURE [App::DocumentObjectGroupPython] H_element674  label="H_element : 438"  # scripted group (container) (typed FeaturePython)
  n = 6
  ref = H_element
FEATURE [App::DocumentObjectGroupPython] C_element724  label="C_element : 477"  # scripted group (container) (typed FeaturePython)
  n = 5
  ref = C_element
FEATURE [App::DocumentObjectGroupPython] N_element324  label="N_element : 176"  # scripted group (container) (typed FeaturePython)
  n = 2
  ref = N_element
FEATURE [App::DocumentObjectGroupPython] O_element634  label="O_element : 406"  # scripted group (container) (typed FeaturePython)
  n = 2
  ref = O_element
FEATURE [App::DocumentObjectGroupPython] G4_THYMINE  # scripted group (container) (typed FeaturePython)
  Dunit = g/cm3
  Dvalue = 1.23
  Group = -> [H_element674,C_element724,N_element324,O_element634]
  conduct = 2
  density = 1
  expand = 3
  formula = G4_THYMINE
  name = G4_THYMINE
  specific = 4
FEATURE [App::DocumentObjectGroupPython] H_element675  label="H_element : 439"  # scripted group (container) (typed FeaturePython)
  n = 4
  ref = H_element
FEATURE [App::DocumentObjectGroupPython] C_element725  label="C_element : 478"  # scripted group (container) (typed FeaturePython)
  n = 4
  ref = C_element
FEATURE [App::DocumentObjectGroupPython] N_element325  label="N_element : 177"  # scripted group (container) (typed FeaturePython)
  n = 2
  ref = N_element
FEATURE [App::DocumentObjectGroupPython] O_element635  label="O_element : 407"  # scripted group (container) (typed FeaturePython)
  n = 2
  ref = O_element
FEATURE [App::DocumentObjectGroupPython] G4_URACIL  # scripted group (container) (typed FeaturePython)
  Dunit = g/cm3
  Dvalue = 1.32
  Group = -> [H_element675,C_element725,N_element325,O_element635]
  conduct = 2
  density = 1
  expand = 3
  formula = G4_URACIL
  name = G4_URACIL
  specific = 4
FEATURE [App::DocumentObjectGroupPython] H_element676  label="H_element : 440"  # scripted group (container) (typed FeaturePython)
  n = 4
  ref = H_element
FEATURE [App::DocumentObjectGroupPython] C_element726  label="C_element : 479"  # scripted group (container) (typed FeaturePython)
  n = 5
  ref = C_element
FEATURE [App::DocumentObjectGroupPython] N_element326  label="N_element : 178"  # scripted group (container) (typed FeaturePython)
  n = 5
  ref = N_element
FEATURE [App::DocumentObjectGroupPython] G4_DNA_ADENINE  # scripted group (container) (typed FeaturePython)
  Dunit = g/cm3
  Dvalue = 1
  Group = -> [H_element676,C_element726,N_element326]
  conduct = 2
  density = 1
  expand = 3
  formula = G4_DNA_ADENINE
  name = G4_DNA_ADENINE
  specific = 4
FEATURE [App::DocumentObjectGroupPython] H_element677  label="H_element : 441"  # scripted group (container) (typed FeaturePython)
  n = 4
  ref = H_element
FEATURE [App::DocumentObjectGroupPython] C_element727  label="C_element : 480"  # scripted group (container) (typed FeaturePython)
  n = 5
  ref = C_element
FEATURE [App::DocumentObjectGroupPython] N_element327  label="N_element : 179"  # scripted group (container) (typed FeaturePython)
  n = 5
  ref = N_element
FEATURE [App::DocumentObjectGroupPython] O_element636  label="O_element : 408"  # scripted group (container) (typed FeaturePython)
  n = 1
  ref = O_element
FEATURE [App::DocumentObjectGroupPython] G4_DNA_GUANINE  # scripted group (container) (typed FeaturePython)
  Dunit = g/cm3
  Dvalue = 1
  Group = -> [H_element677,C_element727,N_element327,O_element636]
  conduct = 2
  density = 1
  expand = 3
  formula = G4_DNA_GUANINE
  name = G4_DNA_GUANINE
  specific = 4
FEATURE [App::DocumentObjectGroupPython] H_element678  label="H_element : 442"  # scripted group (container) (typed FeaturePython)
  n = 4
  ref = H_element
FEATURE [App::DocumentObjectGroupPython] C_element728  label="C_element : 481"  # scripted group (container) (typed FeaturePython)
  n = 4
  ref = C_element
FEATURE [App::DocumentObjectGroupPython] N_element328  label="N_element : 180"  # scripted group (container) (typed FeaturePython)
  n = 3
  ref = N_element
FEATURE [App::DocumentObjectGroupPython] O_element637  label="O_element : 409"  # scripted group (container) (typed FeaturePython)
  n = 1
  ref = O_element
FEATURE [App::DocumentObjectGroupPython] G4_DNA_CYTOSINE  # scripted group (container) (typed FeaturePython)
  Dunit = g/cm3
  Dvalue = 1
  Group = -> [H_element678,C_element728,N_element328,O_element637]
  conduct = 2
  density = 1
  expand = 3
  formula = G4_DNA_CYTOSINE
  name = G4_DNA_CYTOSINE
  specific = 4
FEATURE [App::DocumentObjectGroupPython] H_element679  label="H_element : 443"  # scripted group (container) (typed FeaturePython)
  n = 5
  ref = H_element
FEATURE [App::DocumentObjectGroupPython] C_element729  label="C_element : 482"  # scripted group (container) (typed FeaturePython)
  n = 5
  ref = C_element
FEATURE [App::DocumentObjectGroupPython] N_element329  label="N_element : 181"  # scripted group (container) (typed FeaturePython)
  n = 2
  ref = N_element
FEATURE [App::DocumentObjectGroupPython] O_element638  label="O_element : 410"  # scripted group (container) (typed FeaturePython)
  n = 2
  ref = O_element
FEATURE [App::DocumentObjectGroupPython] G4_DNA_THYMINE  # scripted group (container) (typed FeaturePython)
  Dunit = g/cm3
  Dvalue = 1
  Group = -> [H_element679,C_element729,N_element329,O_element638]
  conduct = 2
  density = 1
  expand = 3
  formula = G4_DNA_THYMINE
  name = G4_DNA_THYMINE
  specific = 4
FEATURE [App::DocumentObjectGroupPython] H_element680  label="H_element : 444"  # scripted group (container) (typed FeaturePython)
  n = 3
  ref = H_element
FEATURE [App::DocumentObjectGroupPython] C_element730  label="C_element : 483"  # scripted group (container) (typed FeaturePython)
  n = 4
  ref = C_element
FEATURE [App::DocumentObjectGroupPython] N_element330  label="N_element : 182"  # scripted group (container) (typed FeaturePython)
  n = 2
  ref = N_element
FEATURE [App::DocumentObjectGroupPython] O_element639  label="O_element : 411"  # scripted group (container) (typed FeaturePython)
  n = 2
  ref = O_element
FEATURE [App::DocumentObjectGroupPython] G4_DNA_URACIL  # scripted group (container) (typed FeaturePython)
  Dunit = g/cm3
  Dvalue = 1
  Group = -> [H_element680,C_element730,N_element330,O_element639]
  conduct = 2
  density = 1
  expand = 3
  formula = G4_DNA_URACIL
  name = G4_DNA_URACIL
  specific = 4
FEATURE [App::DocumentObjectGroupPython] H_element681  label="H_element : 445"  # scripted group (container) (typed FeaturePython)
  n = 10
  ref = H_element
FEATURE [App::DocumentObjectGroupPython] C_element731  label="C_element : 484"  # scripted group (container) (typed FeaturePython)
  n = 10
  ref = C_element
FEATURE [App::DocumentObjectGroupPython] N_element331  label="N_element : 183"  # scripted group (container) (typed FeaturePython)
  n = 5
  ref = N_element
FEATURE [App::DocumentObjectGroupPython] O_element640  label="O_element : 412"  # scripted group (container) (typed FeaturePython)
  n = 4
  ref = O_element
FEATURE [App::DocumentObjectGroupPython] G4_DNA_ADENOSINE  # scripted group (container) (typed FeaturePython)
  Dunit = g/cm3
  Dvalue = 1
  Group = -> [H_element681,C_element731,N_element331,O_element640]
  conduct = 2
  density = 1
  expand = 3
  formula = G4_DNA_ADENOSINE
  name = G4_DNA_ADENOSINE
  specific = 4
FEATURE [App::DocumentObjectGroupPython] H_element682  label="H_element : 446"  # scripted group (container) (typed FeaturePython)
  n = 10
  ref = H_element
FEATURE [App::DocumentObjectGroupPython] C_element732  label="C_element : 485"  # scripted group (container) (typed FeaturePython)
  n = 10
  ref = C_element
FEATURE [App::DocumentObjectGroupPython] N_element332  label="N_element : 184"  # scripted group (container) (typed FeaturePython)
  n = 5
  ref = N_element
FEATURE [App::DocumentObjectGroupPython] O_element641  label="O_element : 413"  # scripted group (container) (typed FeaturePython)
  n = 5
  ref = O_element
FEATURE [App::DocumentObjectGroupPython] G4_DNA_GUANOSINE  # scripted group (container) (typed FeaturePython)
  Dunit = g/cm3
  Dvalue = 1
  Group = -> [H_element682,C_element732,N_element332,O_element641]
  conduct = 2
  density = 1
  expand = 3
  formula = G4_DNA_GUANOSINE
  name = G4_DNA_GUANOSINE
  specific = 4
FEATURE [App::DocumentObjectGroupPython] H_element683  label="H_element : 447"  # scripted group (container) (typed FeaturePython)
  n = 10
  ref = H_element
FEATURE [App::DocumentObjectGroupPython] C_element733  label="C_element : 486"  # scripted group (container) (typed FeaturePython)
  n = 9
  ref = C_element
FEATURE [App::DocumentObjectGroupPython] N_element333  label="N_element : 185"  # scripted group (container) (typed FeaturePython)
  n = 3
  ref = N_element
FEATURE [App::DocumentObjectGroupPython] O_element642  label="O_element : 414"  # scripted group (container) (typed FeaturePython)
  n = 5
  ref = O_element
FEATURE [App::DocumentObjectGroupPython] G4_DNA_CYTIDINE  # scripted group (container) (typed FeaturePython)
  Dunit = g/cm3
  Dvalue = 1
  Group = -> [H_element683,C_element733,N_element333,O_element642]
  conduct = 2
  density = 1
  expand = 3
  formula = G4_DNA_CYTIDINE
  name = G4_DNA_CYTIDINE
  specific = 4
FEATURE [App::DocumentObjectGroupPython] H_element684  label="H_element : 448"  # scripted group (container) (typed FeaturePython)
  n = 9
  ref = H_element
FEATURE [App::DocumentObjectGroupPython] C_element734  label="C_element : 487"  # scripted group (container) (typed FeaturePython)
  n = 9
  ref = C_element
FEATURE [App::DocumentObjectGroupPython] N_element334  label="N_element : 186"  # scripted group (container) (typed FeaturePython)
  n = 2
  ref = N_element
FEATURE [App::DocumentObjectGroupPython] O_element643  label="O_element : 415"  # scripted group (container) (typed FeaturePython)
  n = 6
  ref = O_element
FEATURE [App::DocumentObjectGroupPython] G4_DNA_URIDINE  # scripted group (container) (typed FeaturePython)
  Dunit = g/cm3
  Dvalue = 1
  Group = -> [H_element684,C_element734,N_element334,O_element643]
  conduct = 2
  density = 1
  expand = 3
  formula = G4_DNA_URIDINE
  name = G4_DNA_URIDINE
  specific = 4
FEATURE [App::DocumentObjectGroupPython] H_element685  label="H_element : 449"  # scripted group (container) (typed FeaturePython)
  n = 11
  ref = H_element
FEATURE [App::DocumentObjectGroupPython] C_element735  label="C_element : 488"  # scripted group (container) (typed FeaturePython)
  n = 10
  ref = C_element
FEATURE [App::DocumentObjectGroupPython] N_element335  label="N_element : 187"  # scripted group (container) (typed FeaturePython)
  n = 2
  ref = N_element
FEATURE [App::DocumentObjectGroupPython] O_element644  label="O_element : 416"  # scripted group (container) (typed FeaturePython)
  n = 6
  ref = O_element
FEATURE [App::DocumentObjectGroupPython] G4_DNA_METHYLURIDINE  # scripted group (container) (typed FeaturePython)
  Dunit = g/cm3
  Dvalue = 1
  Group = -> [H_element685,C_element735,N_element335,O_element644]
  conduct = 2
  density = 1
  expand = 3
  formula = G4_DNA_METHYLURIDINE
  name = G4_DNA_METHYLURIDINE
  specific = 4
FEATURE [App::DocumentObjectGroupPython] P_element090  label="P_element : 034"  # scripted group (container) (typed FeaturePython)
  n = 1
  ref = P_element
FEATURE [App::DocumentObjectGroupPython] O_element645  label="O_element : 417"  # scripted group (container) (typed FeaturePython)
  n = 3
  ref = O_element
FEATURE [App::DocumentObjectGroupPython] G4_DNA_MONOPHOSPHATE  # scripted group (container) (typed FeaturePython)
  Dunit = g/cm3
  Dvalue = 1
  Group = -> [P_element090,O_element645]
  conduct = 2
  density = 1
  expand = 3
  formula = G4_DNA_MONOPHOSPHATE
  name = G4_DNA_MONOPHOSPHATE
  specific = 4
FEATURE [App::DocumentObjectGroupPython] H_element686  label="H_element : 450"  # scripted group (container) (typed FeaturePython)
  n = 10
  ref = H_element
FEATURE [App::DocumentObjectGroupPython] C_element736  label="C_element : 489"  # scripted group (container) (typed FeaturePython)
  n = 10
  ref = C_element
FEATURE [App::DocumentObjectGroupPython] N_element336  label="N_element : 188"  # scripted group (container) (typed FeaturePython)
  n = 5
  ref = N_element
FEATURE [App::DocumentObjectGroupPython] O_element646  label="O_element : 418"  # scripted group (container) (typed FeaturePython)
  n = 7
  ref = O_element
FEATURE [App::DocumentObjectGroupPython] P_element091  label="P_element : 035"  # scripted group (container) (typed FeaturePython)
  n = 1
  ref = P_element
FEATURE [App::DocumentObjectGroupPython] G4_DNA_A  # scripted group (container) (typed FeaturePython)
  Dunit = g/cm3
  Dvalue = 1
  Group = -> [H_element686,C_element736,N_element336,O_element646,P_element091]
  conduct = 2
  density = 1
  expand = 3
  formula = G4_DNA_A
  name = G4_DNA_A
  specific = 4
FEATURE [App::DocumentObjectGroupPython] H_element687  label="H_element : 451"  # scripted group (container) (typed FeaturePython)
  n = 10
  ref = H_element
FEATURE [App::DocumentObjectGroupPython] C_element737  label="C_element : 490"  # scripted group (container) (typed FeaturePython)
  n = 10
  ref = C_element
FEATURE [App::DocumentObjectGroupPython] N_element337  label="N_element : 189"  # scripted group (container) (typed FeaturePython)
  n = 5
  ref = N_element
FEATURE [App::DocumentObjectGroupPython] O_element647  label="O_element : 419"  # scripted group (container) (typed FeaturePython)
  n = 8
  ref = O_element
FEATURE [App::DocumentObjectGroupPython] P_element092  label="P_element : 036"  # scripted group (container) (typed FeaturePython)
  n = 1
  ref = P_element
FEATURE [App::DocumentObjectGroupPython] G4_DNA_G  # scripted group (container) (typed FeaturePython)
  Dunit = g/cm3
  Dvalue = 1
  Group = -> [H_element687,C_element737,N_element337,O_element647,P_element092]
  conduct = 2
  density = 1
  expand = 3
  formula = G4_DNA_G
  name = G4_DNA_G
  specific = 4
FEATURE [App::DocumentObjectGroupPython] H_element688  label="H_element : 452"  # scripted group (container) (typed FeaturePython)
  n = 10
  ref = H_element
FEATURE [App::DocumentObjectGroupPython] C_element738  label="C_element : 491"  # scripted group (container) (typed FeaturePython)
  n = 9
  ref = C_element
FEATURE [App::DocumentObjectGroupPython] N_element338  label="N_element : 190"  # scripted group (container) (typed FeaturePython)
  n = 3
  ref = N_element
FEATURE [App::DocumentObjectGroupPython] O_element648  label="O_element : 420"  # scripted group (container) (typed FeaturePython)
  n = 8
  ref = O_element
FEATURE [App::DocumentObjectGroupPython] P_element093  label="P_element : 037"  # scripted group (container) (typed FeaturePython)
  n = 1
  ref = P_element
FEATURE [App::DocumentObjectGroupPython] G4_DNA_C  # scripted group (container) (typed FeaturePython)
  Dunit = g/cm3
  Dvalue = 1
  Group = -> [H_element688,C_element738,N_element338,O_element648,P_element093]
  conduct = 2
  density = 1
  expand = 3
  formula = G4_DNA_C
  name = G4_DNA_C
  specific = 4
FEATURE [App::DocumentObjectGroupPython] H_element689  label="H_element : 453"  # scripted group (container) (typed FeaturePython)
  n = 9
  ref = H_element
FEATURE [App::DocumentObjectGroupPython] C_element739  label="C_element : 492"  # scripted group (container) (typed FeaturePython)
  n = 9
  ref = C_element
FEATURE [App::DocumentObjectGroupPython] N_element339  label="N_element : 191"  # scripted group (container) (typed FeaturePython)
  n = 2
  ref = N_element
FEATURE [App::DocumentObjectGroupPython] O_element649  label="O_element : 421"  # scripted group (container) (typed FeaturePython)
  n = 9
  ref = O_element
FEATURE [App::DocumentObjectGroupPython] P_element094  label="P_element : 038"  # scripted group (container) (typed FeaturePython)
  n = 1
  ref = P_element
FEATURE [App::DocumentObjectGroupPython] G4_DNA_U  # scripted group (container) (typed FeaturePython)
  Dunit = g/cm3
  Dvalue = 1
  Group = -> [H_element689,C_element739,N_element339,O_element649,P_element094]
  conduct = 2
  density = 1
  expand = 3
  formula = G4_DNA_U
  name = G4_DNA_U
  specific = 4
FEATURE [App::DocumentObjectGroupPython] H_element690  label="H_element : 454"  # scripted group (container) (typed FeaturePython)
  n = 11
  ref = H_element
FEATURE [App::DocumentObjectGroupPython] C_element740  label="C_element : 493"  # scripted group (container) (typed FeaturePython)
  n = 10
  ref = C_element
FEATURE [App::DocumentObjectGroupPython] N_element340  label="N_element : 192"  # scripted group (container) (typed FeaturePython)
  n = 2
  ref = N_element
FEATURE [App::DocumentObjectGroupPython] O_element650  label="O_element : 422"  # scripted group (container) (typed FeaturePython)
  n = 9
  ref = O_element
FEATURE [App::DocumentObjectGroupPython] P_element095  label="P_element : 039"  # scripted group (container) (typed FeaturePython)
  n = 1
  ref = P_element
FEATURE [App::DocumentObjectGroupPython] G4_DNA_MU  # scripted group (container) (typed FeaturePython)
  Dunit = g/cm3
  Dvalue = 1
  Group = -> [H_element690,C_element740,N_element340,O_element650,P_element095]
  conduct = 2
  density = 1
  expand = 3
  formula = G4_DNA_MU
  name = G4_DNA_MU
  specific = 4
FEATURE [App::DocumentObjectGroupPython] BioChemical  # scripted group (container) (typed FeaturePython)
  Group = -> [G4_CYTOSINE,G4_THYMINE,G4_URACIL,G4_DNA_ADENINE,G4_DNA_GUANINE,G4_DNA_CYTOSINE,G4_DNA_THYMINE,G4_DNA_URACIL,G4_DNA_ADENOSINE,G4_DNA_GUANOSINE,G4_DNA_CYTIDINE,G4_DNA_URIDINE,G4_DNA_METHYLURIDINE,G4_DNA_MONOPHOSPHATE,G4_DNA_A,G4_DNA_G,G4_DNA_C,G4_DNA_U,G4_DNA_MU]
FEATURE [App::DocumentObjectGroupPython] G4Materials  # scripted group (container) (typed FeaturePython)
  Group = -> [NIST,Element,HEP,Space,BioChemical]
FEATURE [App::DocumentObjectGroupPython] Geant4  # scripted group (container) (typed FeaturePython)
  Group = -> [G4Isotopes,G4Elements,G4Materials]
FEATURE [App::DocumentObjectGroupPython] Materials  # scripted group (container) (typed FeaturePython)
  Group = -> [Geant4]
